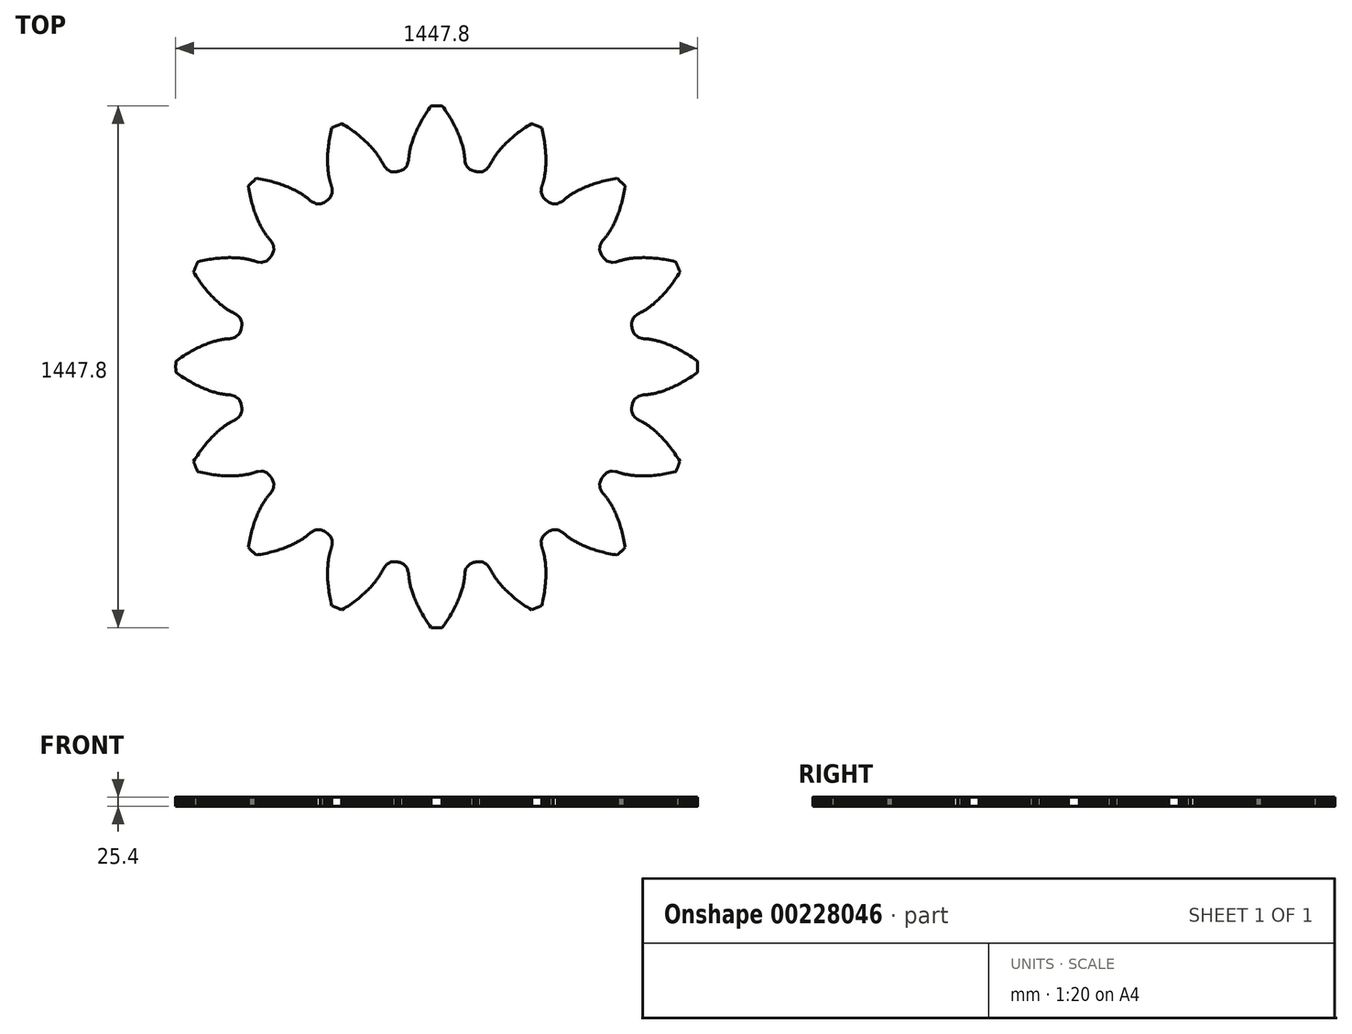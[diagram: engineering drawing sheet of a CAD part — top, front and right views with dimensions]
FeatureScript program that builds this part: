
annotation { "Feature Type Name" : "Feature", "Feature Type Description" : "" }
export const myFeature = defineFeature(function(context is Context, id is Id, definition is map)
    precondition{}
    {
        {
            var Q0;
            Q0=qCreatedBy(makeId("Top.planeOp"),FACE);
            var sketch = newSketch(context, id + "F0", { "sketchPlane" : qUnion([Q0])});
            skLineSegment(sketch, "E0", {"start": v(-103.28, 542.7) * mm, "end": v(-102.33, 543.03) * mm});
            skLineSegment(sketch, "E1", {"start": v(-102.33, 543.03) * mm, "end": v(-92.47, 547.21) * mm});
            skLineSegment(sketch, "E2", {"start": v(-92.47, 547.21) * mm, "end": v(-91.6, 547.71) * mm});
            skLineSegment(sketch, "E3", {"start": v(-91.6, 547.71) * mm, "end": v(-90.77, 548.41) * mm});
            skLineSegment(sketch, "E4", {"start": v(-90.77, 548.41) * mm, "end": v(-83.6, 556.27) * mm});
            skLineSegment(sketch, "E5", {"start": v(-83.6, 556.27) * mm, "end": v(-82.92, 557.1) * mm});
            skLineSegment(sketch, "E6", {"start": v(-82.92, 557.1) * mm, "end": v(-82.3, 558.13) * mm});
            skLineSegment(sketch, "E7", {"start": v(-82.3, 558.13) * mm, "end": v(-81.75, 559.35) * mm});
            skLineSegment(sketch, "E8", {"start": v(-81.75, 559.35) * mm, "end": v(-81.27, 560.76) * mm});
            skLineSegment(sketch, "E9", {"start": v(-81.27, 560.76) * mm, "end": v(-78.74, 569.29) * mm});
            skLineSegment(sketch, "E10", {"start": v(-78.74, 569.29) * mm, "end": v(-78.38, 570.57) * mm});
            skLineSegment(sketch, "E11", {"start": v(-78.38, 570.57) * mm, "end": v(-78.1, 572.03) * mm});
            skLineSegment(sketch, "E12", {"start": v(-78.1, 572.03) * mm, "end": v(-77.89, 573.68) * mm});
            skLineSegment(sketch, "E13", {"start": v(-77.89, 573.68) * mm, "end": v(-77.77, 575.5) * mm});
            skLineSegment(sketch, "E14", {"start": v(-77.77, 575.5) * mm, "end": v(-77.76, 575.78) * mm});
            skLineSegment(sketch, "E15", {"start": v(-77.76, 575.78) * mm, "end": v(-77.7, 577.35) * mm});
            skLineSegment(sketch, "E16", {"start": v(-77.7, 577.35) * mm, "end": v(-77.6, 579.06) * mm});
            skLineSegment(sketch, "E17", {"start": v(-77.6, 579.06) * mm, "end": v(-77.46, 580.9) * mm});
            skLineSegment(sketch, "E18", {"start": v(-77.46, 580.9) * mm, "end": v(-77.29, 582.87) * mm});
            skLineSegment(sketch, "E19", {"start": v(-77.29, 582.87) * mm, "end": v(-77.07, 584.98) * mm});
            skLineSegment(sketch, "E20", {"start": v(-77.07, 584.98) * mm, "end": v(-76.8, 587.21) * mm});
            skLineSegment(sketch, "E21", {"start": v(-76.8, 587.21) * mm, "end": v(-76.48, 589.59) * mm});
            skLineSegment(sketch, "E22", {"start": v(-76.48, 589.59) * mm, "end": v(-76.1, 592.09) * mm});
            skLineSegment(sketch, "E23", {"start": v(-76.1, 592.09) * mm, "end": v(-75.66, 594.72) * mm});
            skLineSegment(sketch, "E24", {"start": v(-75.66, 594.72) * mm, "end": v(-75.16, 597.47) * mm});
            skLineSegment(sketch, "E25", {"start": v(-75.16, 597.47) * mm, "end": v(-74.59, 600.36) * mm});
            skLineSegment(sketch, "E26", {"start": v(-74.59, 600.36) * mm, "end": v(-73.94, 603.37) * mm});
            skLineSegment(sketch, "E27", {"start": v(-73.94, 603.37) * mm, "end": v(-73.22, 606.5) * mm});
            skLineSegment(sketch, "E28", {"start": v(-73.22, 606.5) * mm, "end": v(-72.41, 609.75) * mm});
            skLineSegment(sketch, "E29", {"start": v(-72.41, 609.75) * mm, "end": v(-71.52, 613.12) * mm});
            skLineSegment(sketch, "E30", {"start": v(-71.52, 613.12) * mm, "end": v(-70.54, 616.61) * mm});
            skLineSegment(sketch, "E31", {"start": v(-70.54, 616.61) * mm, "end": v(-69.47, 620.22) * mm});
            skLineSegment(sketch, "E32", {"start": v(-69.47, 620.22) * mm, "end": v(-68.3, 623.94) * mm});
            skLineSegment(sketch, "E33", {"start": v(-68.3, 623.94) * mm, "end": v(-67.03, 627.77) * mm});
            skLineSegment(sketch, "E34", {"start": v(-67.03, 627.77) * mm, "end": v(-65.66, 631.71) * mm});
            skLineSegment(sketch, "E35", {"start": v(-65.66, 631.71) * mm, "end": v(-64.18, 635.76) * mm});
            skLineSegment(sketch, "E36", {"start": v(-64.18, 635.76) * mm, "end": v(-62.59, 639.91) * mm});
            skLineSegment(sketch, "E37", {"start": v(-62.59, 639.91) * mm, "end": v(-60.88, 644.16) * mm});
            skLineSegment(sketch, "E38", {"start": v(-60.88, 644.16) * mm, "end": v(-59.05, 648.52) * mm});
            skLineSegment(sketch, "E39", {"start": v(-59.05, 648.52) * mm, "end": v(-57.1, 652.97) * mm});
            skLineSegment(sketch, "E40", {"start": v(-57.1, 652.97) * mm, "end": v(-55.03, 657.51) * mm});
            skLineSegment(sketch, "E41", {"start": v(-55.03, 657.51) * mm, "end": v(-52.83, 662.15) * mm});
            skLineSegment(sketch, "E42", {"start": v(-52.83, 662.15) * mm, "end": v(-50.5, 666.87) * mm});
            skLineSegment(sketch, "E43", {"start": v(-50.5, 666.87) * mm, "end": v(-48.03, 671.68) * mm});
            skLineSegment(sketch, "E44", {"start": v(-48.03, 671.68) * mm, "end": v(-45.42, 676.57) * mm});
            skLineSegment(sketch, "E45", {"start": v(-45.42, 676.57) * mm, "end": v(-42.67, 681.54) * mm});
            skLineSegment(sketch, "E46", {"start": v(-42.67, 681.54) * mm, "end": v(-39.77, 686.59) * mm});
            skLineSegment(sketch, "E47", {"start": v(-39.77, 686.59) * mm, "end": v(-36.73, 691.7) * mm});
            skLineSegment(sketch, "E48", {"start": v(-36.73, 691.7) * mm, "end": v(-33.54, 696.9) * mm});
            skLineSegment(sketch, "E49", {"start": v(-33.54, 696.9) * mm, "end": v(-30.2, 702.14) * mm});
            skLineSegment(sketch, "E50", {"start": v(-30.2, 702.14) * mm, "end": v(-26.7, 707.46) * mm});
            skLineSegment(sketch, "E51", {"start": v(-26.7, 707.46) * mm, "end": v(-23.03, 712.83) * mm});
            skLineSegment(sketch, "E52", {"start": v(-23.03, 712.83) * mm, "end": v(-19.2, 718.26) * mm});
            skLineSegment(sketch, "E53", {"start": v(-19.2, 718.26) * mm, "end": v(-15.22, 723.74) * mm});
            skLineSegment(sketch, "E54", {"start": v(103.28, 542.7) * mm, "end": v(102.33, 543.03) * mm});
            skLineSegment(sketch, "E55", {"start": v(102.33, 543.03) * mm, "end": v(92.47, 547.21) * mm});
            skLineSegment(sketch, "E56", {"start": v(92.47, 547.21) * mm, "end": v(91.6, 547.71) * mm});
            skLineSegment(sketch, "E57", {"start": v(91.6, 547.71) * mm, "end": v(90.77, 548.41) * mm});
            skLineSegment(sketch, "E58", {"start": v(90.77, 548.41) * mm, "end": v(83.6, 556.27) * mm});
            skLineSegment(sketch, "E59", {"start": v(83.6, 556.27) * mm, "end": v(82.92, 557.1) * mm});
            skLineSegment(sketch, "E60", {"start": v(82.92, 557.1) * mm, "end": v(82.3, 558.13) * mm});
            skLineSegment(sketch, "E61", {"start": v(82.3, 558.13) * mm, "end": v(81.75, 559.35) * mm});
            skLineSegment(sketch, "E62", {"start": v(81.75, 559.35) * mm, "end": v(81.27, 560.76) * mm});
            skLineSegment(sketch, "E63", {"start": v(81.27, 560.76) * mm, "end": v(78.74, 569.29) * mm});
            skLineSegment(sketch, "E64", {"start": v(78.74, 569.29) * mm, "end": v(78.38, 570.57) * mm});
            skLineSegment(sketch, "E65", {"start": v(78.38, 570.57) * mm, "end": v(78.1, 572.03) * mm});
            skLineSegment(sketch, "E66", {"start": v(78.1, 572.03) * mm, "end": v(77.89, 573.68) * mm});
            skLineSegment(sketch, "E67", {"start": v(77.89, 573.68) * mm, "end": v(77.77, 575.5) * mm});
            skLineSegment(sketch, "E68", {"start": v(77.77, 575.5) * mm, "end": v(77.76, 575.78) * mm});
            skLineSegment(sketch, "E69", {"start": v(77.76, 575.78) * mm, "end": v(77.7, 577.35) * mm});
            skLineSegment(sketch, "E70", {"start": v(77.7, 577.35) * mm, "end": v(77.6, 579.06) * mm});
            skLineSegment(sketch, "E71", {"start": v(77.6, 579.06) * mm, "end": v(77.46, 580.9) * mm});
            skLineSegment(sketch, "E72", {"start": v(77.46, 580.9) * mm, "end": v(77.29, 582.87) * mm});
            skLineSegment(sketch, "E73", {"start": v(77.29, 582.87) * mm, "end": v(77.07, 584.98) * mm});
            skLineSegment(sketch, "E74", {"start": v(77.07, 584.98) * mm, "end": v(76.8, 587.21) * mm});
            skLineSegment(sketch, "E75", {"start": v(76.8, 587.21) * mm, "end": v(76.48, 589.59) * mm});
            skLineSegment(sketch, "E76", {"start": v(76.48, 589.59) * mm, "end": v(76.1, 592.09) * mm});
            skLineSegment(sketch, "E77", {"start": v(76.1, 592.09) * mm, "end": v(75.66, 594.72) * mm});
            skLineSegment(sketch, "E78", {"start": v(75.66, 594.72) * mm, "end": v(75.16, 597.47) * mm});
            skLineSegment(sketch, "E79", {"start": v(75.16, 597.47) * mm, "end": v(74.59, 600.36) * mm});
            skLineSegment(sketch, "E80", {"start": v(74.59, 600.36) * mm, "end": v(73.94, 603.37) * mm});
            skLineSegment(sketch, "E81", {"start": v(73.94, 603.37) * mm, "end": v(73.22, 606.5) * mm});
            skLineSegment(sketch, "E82", {"start": v(73.22, 606.5) * mm, "end": v(72.41, 609.75) * mm});
            skLineSegment(sketch, "E83", {"start": v(72.41, 609.75) * mm, "end": v(71.52, 613.12) * mm});
            skLineSegment(sketch, "E84", {"start": v(71.52, 613.12) * mm, "end": v(70.54, 616.61) * mm});
            skLineSegment(sketch, "E85", {"start": v(70.54, 616.61) * mm, "end": v(69.47, 620.22) * mm});
            skLineSegment(sketch, "E86", {"start": v(69.47, 620.22) * mm, "end": v(68.3, 623.94) * mm});
            skLineSegment(sketch, "E87", {"start": v(68.3, 623.94) * mm, "end": v(67.03, 627.77) * mm});
            skLineSegment(sketch, "E88", {"start": v(67.03, 627.77) * mm, "end": v(65.66, 631.71) * mm});
            skLineSegment(sketch, "E89", {"start": v(65.66, 631.71) * mm, "end": v(64.18, 635.76) * mm});
            skLineSegment(sketch, "E90", {"start": v(64.18, 635.76) * mm, "end": v(62.59, 639.91) * mm});
            skLineSegment(sketch, "E91", {"start": v(62.59, 639.91) * mm, "end": v(60.88, 644.16) * mm});
            skLineSegment(sketch, "E92", {"start": v(60.88, 644.16) * mm, "end": v(59.05, 648.52) * mm});
            skLineSegment(sketch, "E93", {"start": v(59.05, 648.52) * mm, "end": v(57.1, 652.97) * mm});
            skLineSegment(sketch, "E94", {"start": v(57.1, 652.97) * mm, "end": v(55.03, 657.51) * mm});
            skLineSegment(sketch, "E95", {"start": v(55.03, 657.51) * mm, "end": v(52.83, 662.15) * mm});
            skLineSegment(sketch, "E96", {"start": v(52.83, 662.15) * mm, "end": v(50.5, 666.87) * mm});
            skLineSegment(sketch, "E97", {"start": v(50.5, 666.87) * mm, "end": v(48.03, 671.68) * mm});
            skLineSegment(sketch, "E98", {"start": v(48.03, 671.68) * mm, "end": v(45.42, 676.57) * mm});
            skLineSegment(sketch, "E99", {"start": v(45.42, 676.57) * mm, "end": v(42.67, 681.54) * mm});
            skLineSegment(sketch, "E100", {"start": v(42.67, 681.54) * mm, "end": v(39.77, 686.59) * mm});
            skLineSegment(sketch, "E101", {"start": v(39.77, 686.59) * mm, "end": v(36.73, 691.7) * mm});
            skLineSegment(sketch, "E102", {"start": v(36.73, 691.7) * mm, "end": v(33.54, 696.9) * mm});
            skLineSegment(sketch, "E103", {"start": v(33.54, 696.9) * mm, "end": v(30.2, 702.14) * mm});
            skLineSegment(sketch, "E104", {"start": v(30.2, 702.14) * mm, "end": v(26.7, 707.46) * mm});
            skLineSegment(sketch, "E105", {"start": v(26.7, 707.46) * mm, "end": v(23.03, 712.83) * mm});
            skLineSegment(sketch, "E106", {"start": v(23.03, 712.83) * mm, "end": v(19.2, 718.26) * mm});
            skLineSegment(sketch, "E107", {"start": v(19.2, 718.26) * mm, "end": v(15.22, 723.74) * mm});
            skArc(sketch, "E108", {"start": v(15.22, 723.74) * mm, "mid": v(0, 723.9) * mm, "end": v(-15.22, 723.74) * mm});
            skLineSegment(sketch, "E109", {"start": v(112.27, 540.92) * mm, "end": v(113.27, 540.85) * mm});
            skLineSegment(sketch, "E110", {"start": v(113.27, 540.85) * mm, "end": v(123.98, 540.94) * mm});
            skLineSegment(sketch, "E111", {"start": v(123.98, 540.94) * mm, "end": v(124.98, 541.07) * mm});
            skLineSegment(sketch, "E112", {"start": v(124.98, 541.07) * mm, "end": v(126, 541.4) * mm});
            skLineSegment(sketch, "E113", {"start": v(126, 541.4) * mm, "end": v(135.64, 545.92) * mm});
            skLineSegment(sketch, "E114", {"start": v(135.64, 545.92) * mm, "end": v(136.59, 546.43) * mm});
            skLineSegment(sketch, "E115", {"start": v(136.59, 546.43) * mm, "end": v(137.55, 547.15) * mm});
            skLineSegment(sketch, "E116", {"start": v(137.55, 547.15) * mm, "end": v(138.53, 548.06) * mm});
            skLineSegment(sketch, "E117", {"start": v(138.53, 548.06) * mm, "end": v(139.5, 549.18) * mm});
            skLineSegment(sketch, "E118", {"start": v(139.5, 549.18) * mm, "end": v(145.11, 556.09) * mm});
            skLineSegment(sketch, "E119", {"start": v(145.11, 556.09) * mm, "end": v(145.93, 557.13) * mm});
            skLineSegment(sketch, "E120", {"start": v(145.93, 557.13) * mm, "end": v(146.76, 558.38) * mm});
            skLineSegment(sketch, "E121", {"start": v(146.76, 558.38) * mm, "end": v(147.58, 559.82) * mm});
            skLineSegment(sketch, "E122", {"start": v(147.58, 559.82) * mm, "end": v(148.4, 561.46) * mm});
            skLineSegment(sketch, "E123", {"start": v(148.4, 561.46) * mm, "end": v(148.5, 561.7) * mm});
            skLineSegment(sketch, "E124", {"start": v(148.5, 561.7) * mm, "end": v(149.17, 563.13) * mm});
            skLineSegment(sketch, "E125", {"start": v(149.17, 563.13) * mm, "end": v(149.9, 564.67) * mm});
            skLineSegment(sketch, "E126", {"start": v(149.9, 564.67) * mm, "end": v(150.74, 566.32) * mm});
            skLineSegment(sketch, "E127", {"start": v(150.74, 566.32) * mm, "end": v(151.65, 568.08) * mm});
            skLineSegment(sketch, "E128", {"start": v(151.65, 568.08) * mm, "end": v(152.66, 569.94) * mm});
            skLineSegment(sketch, "E129", {"start": v(152.66, 569.94) * mm, "end": v(153.76, 571.9) * mm});
            skLineSegment(sketch, "E130", {"start": v(153.76, 571.9) * mm, "end": v(154.97, 573.97) * mm});
            skLineSegment(sketch, "E131", {"start": v(154.97, 573.97) * mm, "end": v(156.27, 576.14) * mm});
            skLineSegment(sketch, "E132", {"start": v(156.27, 576.14) * mm, "end": v(157.68, 578.4) * mm});
            skLineSegment(sketch, "E133", {"start": v(157.68, 578.4) * mm, "end": v(159.2, 580.76) * mm});
            skLineSegment(sketch, "E134", {"start": v(159.2, 580.76) * mm, "end": v(160.84, 583.2) * mm});
            skLineSegment(sketch, "E135", {"start": v(160.84, 583.2) * mm, "end": v(162.59, 585.73) * mm});
            skLineSegment(sketch, "E136", {"start": v(162.59, 585.73) * mm, "end": v(164.45, 588.35) * mm});
            skLineSegment(sketch, "E137", {"start": v(164.45, 588.35) * mm, "end": v(166.44, 591.05) * mm});
            skLineSegment(sketch, "E138", {"start": v(166.44, 591.05) * mm, "end": v(168.55, 593.82) * mm});
            skLineSegment(sketch, "E139", {"start": v(168.55, 593.82) * mm, "end": v(170.8, 596.67) * mm});
            skLineSegment(sketch, "E140", {"start": v(170.8, 596.67) * mm, "end": v(173.16, 599.6) * mm});
            skLineSegment(sketch, "E141", {"start": v(173.16, 599.6) * mm, "end": v(175.67, 602.58) * mm});
            skLineSegment(sketch, "E142", {"start": v(175.67, 602.58) * mm, "end": v(178.3, 605.64) * mm});
            skLineSegment(sketch, "E143", {"start": v(178.3, 605.64) * mm, "end": v(181.08, 608.75) * mm});
            skLineSegment(sketch, "E144", {"start": v(181.08, 608.75) * mm, "end": v(184, 611.92) * mm});
            skLineSegment(sketch, "E145", {"start": v(184, 611.92) * mm, "end": v(187.06, 615.15) * mm});
            skLineSegment(sketch, "E146", {"start": v(187.06, 615.15) * mm, "end": v(190.26, 618.43) * mm});
            skLineSegment(sketch, "E147", {"start": v(190.26, 618.43) * mm, "end": v(193.62, 621.75) * mm});
            skLineSegment(sketch, "E148", {"start": v(193.62, 621.75) * mm, "end": v(197.12, 625.12) * mm});
            skLineSegment(sketch, "E149", {"start": v(197.12, 625.12) * mm, "end": v(200.77, 628.52) * mm});
            skLineSegment(sketch, "E150", {"start": v(200.77, 628.52) * mm, "end": v(204.58, 631.96) * mm});
            skLineSegment(sketch, "E151", {"start": v(204.58, 631.96) * mm, "end": v(208.55, 635.43) * mm});
            skLineSegment(sketch, "E152", {"start": v(208.55, 635.43) * mm, "end": v(212.67, 638.93) * mm});
            skLineSegment(sketch, "E153", {"start": v(212.67, 638.93) * mm, "end": v(216.95, 642.45) * mm});
            skLineSegment(sketch, "E154", {"start": v(216.95, 642.45) * mm, "end": v(221.4, 646) * mm});
            skLineSegment(sketch, "E155", {"start": v(221.4, 646) * mm, "end": v(226, 649.54) * mm});
            skLineSegment(sketch, "E156", {"start": v(226, 649.54) * mm, "end": v(230.77, 653.1) * mm});
            skLineSegment(sketch, "E157", {"start": v(230.77, 653.1) * mm, "end": v(235.7, 656.68) * mm});
            skLineSegment(sketch, "E158", {"start": v(235.7, 656.68) * mm, "end": v(240.8, 660.25) * mm});
            skLineSegment(sketch, "E159", {"start": v(240.8, 660.25) * mm, "end": v(246.07, 663.82) * mm});
            skLineSegment(sketch, "E160", {"start": v(246.07, 663.82) * mm, "end": v(251.51, 667.38) * mm});
            skLineSegment(sketch, "E161", {"start": v(251.51, 667.38) * mm, "end": v(257.12, 670.93) * mm});
            skLineSegment(sketch, "E162", {"start": v(257.12, 670.93) * mm, "end": v(262.9, 674.47) * mm});
            skLineSegment(sketch, "E163", {"start": v(303.1, 461.87) * mm, "end": v(302.34, 462.53) * mm});
            skLineSegment(sketch, "E164", {"start": v(302.34, 462.53) * mm, "end": v(294.84, 470.17) * mm});
            skLineSegment(sketch, "E165", {"start": v(294.84, 470.17) * mm, "end": v(294.22, 470.97) * mm});
            skLineSegment(sketch, "E166", {"start": v(294.22, 470.97) * mm, "end": v(293.73, 471.93) * mm});
            skLineSegment(sketch, "E167", {"start": v(293.73, 471.93) * mm, "end": v(290.1, 481.93) * mm});
            skLineSegment(sketch, "E168", {"start": v(290.1, 481.93) * mm, "end": v(289.8, 482.97) * mm});
            skLineSegment(sketch, "E169", {"start": v(289.8, 482.97) * mm, "end": v(289.63, 484.15) * mm});
            skLineSegment(sketch, "E170", {"start": v(289.63, 484.15) * mm, "end": v(289.59, 485.49) * mm});
            skLineSegment(sketch, "E171", {"start": v(289.59, 485.49) * mm, "end": v(289.68, 486.97) * mm});
            skLineSegment(sketch, "E172", {"start": v(289.68, 486.97) * mm, "end": v(290.6, 495.82) * mm});
            skLineSegment(sketch, "E173", {"start": v(290.6, 495.82) * mm, "end": v(290.76, 497.14) * mm});
            skLineSegment(sketch, "E174", {"start": v(290.76, 497.14) * mm, "end": v(291.06, 498.6) * mm});
            skLineSegment(sketch, "E175", {"start": v(291.06, 498.6) * mm, "end": v(291.5, 500.2) * mm});
            skLineSegment(sketch, "E176", {"start": v(291.5, 500.2) * mm, "end": v(292.08, 501.94) * mm});
            skLineSegment(sketch, "E177", {"start": v(292.08, 501.94) * mm, "end": v(292.18, 502.2) * mm});
            skLineSegment(sketch, "E178", {"start": v(292.18, 502.2) * mm, "end": v(292.72, 503.67) * mm});
            skLineSegment(sketch, "E179", {"start": v(292.72, 503.67) * mm, "end": v(293.28, 505.28) * mm});
            skLineSegment(sketch, "E180", {"start": v(293.28, 505.28) * mm, "end": v(293.86, 507.03) * mm});
            skLineSegment(sketch, "E181", {"start": v(293.86, 507.03) * mm, "end": v(294.46, 508.92) * mm});
            skLineSegment(sketch, "E182", {"start": v(294.46, 508.92) * mm, "end": v(295.06, 510.95) * mm});
            skLineSegment(sketch, "E183", {"start": v(295.06, 510.95) * mm, "end": v(295.67, 513.13) * mm});
            skLineSegment(sketch, "E184", {"start": v(295.67, 513.13) * mm, "end": v(296.28, 515.44) * mm});
            skLineSegment(sketch, "E185", {"start": v(296.28, 515.44) * mm, "end": v(296.9, 517.9) * mm});
            skLineSegment(sketch, "E186", {"start": v(296.9, 517.9) * mm, "end": v(297.5, 520.5) * mm});
            skLineSegment(sketch, "E187", {"start": v(297.5, 520.5) * mm, "end": v(298.08, 523.23) * mm});
            skLineSegment(sketch, "E188", {"start": v(298.08, 523.23) * mm, "end": v(298.66, 526.11) * mm});
            skLineSegment(sketch, "E189", {"start": v(298.66, 526.11) * mm, "end": v(299.21, 529.14) * mm});
            skLineSegment(sketch, "E190", {"start": v(299.21, 529.14) * mm, "end": v(299.74, 532.31) * mm});
            skLineSegment(sketch, "E191", {"start": v(299.74, 532.31) * mm, "end": v(300.24, 535.62) * mm});
            skLineSegment(sketch, "E192", {"start": v(300.24, 535.62) * mm, "end": v(300.71, 539.08) * mm});
            skLineSegment(sketch, "E193", {"start": v(300.71, 539.08) * mm, "end": v(301.14, 542.68) * mm});
            skLineSegment(sketch, "E194", {"start": v(301.14, 542.68) * mm, "end": v(301.53, 546.42) * mm});
            skLineSegment(sketch, "E195", {"start": v(301.53, 546.42) * mm, "end": v(301.88, 550.3) * mm});
            skLineSegment(sketch, "E196", {"start": v(301.88, 550.3) * mm, "end": v(302.17, 554.33) * mm});
            skLineSegment(sketch, "E197", {"start": v(302.17, 554.33) * mm, "end": v(302.4, 558.5) * mm});
            skLineSegment(sketch, "E198", {"start": v(302.4, 558.5) * mm, "end": v(302.59, 562.8) * mm});
            skLineSegment(sketch, "E199", {"start": v(302.59, 562.8) * mm, "end": v(302.7, 567.25) * mm});
            skLineSegment(sketch, "E200", {"start": v(302.7, 567.25) * mm, "end": v(302.76, 571.83) * mm});
            skLineSegment(sketch, "E201", {"start": v(302.76, 571.83) * mm, "end": v(302.74, 576.55) * mm});
            skLineSegment(sketch, "E202", {"start": v(302.74, 576.55) * mm, "end": v(302.64, 581.41) * mm});
            skLineSegment(sketch, "E203", {"start": v(302.64, 581.41) * mm, "end": v(302.46, 586.4) * mm});
            skLineSegment(sketch, "E204", {"start": v(302.46, 586.4) * mm, "end": v(302.2, 591.53) * mm});
            skLineSegment(sketch, "E205", {"start": v(302.2, 591.53) * mm, "end": v(301.85, 596.78) * mm});
            skLineSegment(sketch, "E206", {"start": v(301.85, 596.78) * mm, "end": v(301.41, 602.17) * mm});
            skLineSegment(sketch, "E207", {"start": v(301.41, 602.17) * mm, "end": v(300.87, 607.69) * mm});
            skLineSegment(sketch, "E208", {"start": v(300.87, 607.69) * mm, "end": v(300.24, 613.33) * mm});
            skLineSegment(sketch, "E209", {"start": v(300.24, 613.33) * mm, "end": v(299.5, 619.1) * mm});
            skLineSegment(sketch, "E210", {"start": v(299.5, 619.1) * mm, "end": v(298.64, 625) * mm});
            skLineSegment(sketch, "E211", {"start": v(298.64, 625) * mm, "end": v(297.67, 631) * mm});
            skLineSegment(sketch, "E212", {"start": v(297.67, 631) * mm, "end": v(296.6, 637.14) * mm});
            skLineSegment(sketch, "E213", {"start": v(296.6, 637.14) * mm, "end": v(295.4, 643.4) * mm});
            skLineSegment(sketch, "E214", {"start": v(295.4, 643.4) * mm, "end": v(294.06, 649.76) * mm});
            skLineSegment(sketch, "E215", {"start": v(294.06, 649.76) * mm, "end": v(292.6, 656.23) * mm});
            skLineSegment(sketch, "E216", {"start": v(292.6, 656.23) * mm, "end": v(291.02, 662.82) * mm});
            skArc(sketch, "E217", {"start": v(291.02, 662.82) * mm, "mid": v(277.02, 668.8) * mm, "end": v(262.9, 674.47) * mm});
            skLineSegment(sketch, "E218", {"start": v(310.72, 456.78) * mm, "end": v(311.62, 456.33) * mm});
            skLineSegment(sketch, "E219", {"start": v(311.62, 456.33) * mm, "end": v(321.55, 452.32) * mm});
            skLineSegment(sketch, "E220", {"start": v(321.55, 452.32) * mm, "end": v(322.53, 452.06) * mm});
            skLineSegment(sketch, "E221", {"start": v(322.53, 452.06) * mm, "end": v(323.6, 451.97) * mm});
            skLineSegment(sketch, "E222", {"start": v(323.6, 451.97) * mm, "end": v(334.23, 452.45) * mm});
            skLineSegment(sketch, "E223", {"start": v(334.23, 452.45) * mm, "end": v(335.3, 452.57) * mm});
            skLineSegment(sketch, "E224", {"start": v(335.3, 452.57) * mm, "end": v(336.46, 452.86) * mm});
            skLineSegment(sketch, "E225", {"start": v(336.46, 452.86) * mm, "end": v(337.71, 453.33) * mm});
            skLineSegment(sketch, "E226", {"start": v(337.71, 453.33) * mm, "end": v(339.05, 453.99) * mm});
            skLineSegment(sketch, "E227", {"start": v(339.05, 453.99) * mm, "end": v(346.87, 458.22) * mm});
            skLineSegment(sketch, "E228", {"start": v(346.87, 458.22) * mm, "end": v(348.03, 458.88) * mm});
            skLineSegment(sketch, "E229", {"start": v(348.03, 458.88) * mm, "end": v(349.27, 459.71) * mm});
            skLineSegment(sketch, "E230", {"start": v(349.27, 459.71) * mm, "end": v(350.58, 460.73) * mm});
            skLineSegment(sketch, "E231", {"start": v(350.58, 460.73) * mm, "end": v(351.96, 461.94) * mm});
            skLineSegment(sketch, "E232", {"start": v(351.96, 461.94) * mm, "end": v(352.16, 462.12) * mm});
            skLineSegment(sketch, "E233", {"start": v(352.16, 462.12) * mm, "end": v(353.31, 463.18) * mm});
            skLineSegment(sketch, "E234", {"start": v(353.31, 463.18) * mm, "end": v(354.59, 464.32) * mm});
            skLineSegment(sketch, "E235", {"start": v(354.59, 464.32) * mm, "end": v(355.98, 465.53) * mm});
            skLineSegment(sketch, "E236", {"start": v(355.98, 465.53) * mm, "end": v(357.5, 466.8) * mm});
            skLineSegment(sketch, "E237", {"start": v(357.5, 466.8) * mm, "end": v(359.15, 468.13) * mm});
            skLineSegment(sketch, "E238", {"start": v(359.15, 468.13) * mm, "end": v(360.92, 469.53) * mm});
            skLineSegment(sketch, "E239", {"start": v(360.92, 469.53) * mm, "end": v(362.82, 470.98) * mm});
            skLineSegment(sketch, "E240", {"start": v(362.82, 470.98) * mm, "end": v(364.86, 472.48) * mm});
            skLineSegment(sketch, "E241", {"start": v(364.86, 472.48) * mm, "end": v(367.03, 474.03) * mm});
            skLineSegment(sketch, "E242", {"start": v(367.03, 474.03) * mm, "end": v(369.33, 475.62) * mm});
            skLineSegment(sketch, "E243", {"start": v(369.33, 475.62) * mm, "end": v(371.78, 477.26) * mm});
            skLineSegment(sketch, "E244", {"start": v(371.78, 477.26) * mm, "end": v(374.36, 478.93) * mm});
            skLineSegment(sketch, "E245", {"start": v(374.36, 478.93) * mm, "end": v(377.09, 480.63) * mm});
            skLineSegment(sketch, "E246", {"start": v(377.09, 480.63) * mm, "end": v(379.95, 482.36) * mm});
            skLineSegment(sketch, "E247", {"start": v(379.95, 482.36) * mm, "end": v(382.97, 484.12) * mm});
            skLineSegment(sketch, "E248", {"start": v(382.97, 484.12) * mm, "end": v(386.13, 485.9) * mm});
            skLineSegment(sketch, "E249", {"start": v(386.13, 485.9) * mm, "end": v(389.44, 487.69) * mm});
            skLineSegment(sketch, "E250", {"start": v(389.44, 487.69) * mm, "end": v(392.9, 489.49) * mm});
            skLineSegment(sketch, "E251", {"start": v(392.9, 489.49) * mm, "end": v(396.5, 491.3) * mm});
            skLineSegment(sketch, "E252", {"start": v(396.5, 491.3) * mm, "end": v(400.26, 493.12) * mm});
            skLineSegment(sketch, "E253", {"start": v(400.26, 493.12) * mm, "end": v(404.17, 494.93) * mm});
            skLineSegment(sketch, "E254", {"start": v(404.17, 494.93) * mm, "end": v(408.23, 496.74) * mm});
            skLineSegment(sketch, "E255", {"start": v(408.23, 496.74) * mm, "end": v(412.44, 498.54) * mm});
            skLineSegment(sketch, "E256", {"start": v(412.44, 498.54) * mm, "end": v(416.81, 500.33) * mm});
            skLineSegment(sketch, "E257", {"start": v(416.81, 500.33) * mm, "end": v(421.34, 502.1) * mm});
            skLineSegment(sketch, "E258", {"start": v(421.34, 502.1) * mm, "end": v(426.02, 503.85) * mm});
            skLineSegment(sketch, "E259", {"start": v(426.02, 503.85) * mm, "end": v(430.85, 505.57) * mm});
            skLineSegment(sketch, "E260", {"start": v(430.85, 505.57) * mm, "end": v(435.84, 507.26) * mm});
            skLineSegment(sketch, "E261", {"start": v(435.84, 507.26) * mm, "end": v(440.99, 508.9) * mm});
            skLineSegment(sketch, "E262", {"start": v(440.99, 508.9) * mm, "end": v(446.3, 510.52) * mm});
            skLineSegment(sketch, "E263", {"start": v(446.3, 510.52) * mm, "end": v(451.75, 512.1) * mm});
            skLineSegment(sketch, "E264", {"start": v(451.75, 512.1) * mm, "end": v(457.37, 513.61) * mm});
            skLineSegment(sketch, "E265", {"start": v(457.37, 513.61) * mm, "end": v(463.14, 515.08) * mm});
            skLineSegment(sketch, "E266", {"start": v(463.14, 515.08) * mm, "end": v(469.06, 516.5) * mm});
            skLineSegment(sketch, "E267", {"start": v(469.06, 516.5) * mm, "end": v(475.14, 517.84) * mm});
            skLineSegment(sketch, "E268", {"start": v(475.14, 517.84) * mm, "end": v(481.38, 519.12) * mm});
            skLineSegment(sketch, "E269", {"start": v(481.38, 519.12) * mm, "end": v(487.76, 520.33) * mm});
            skLineSegment(sketch, "E270", {"start": v(487.76, 520.33) * mm, "end": v(494.3, 521.47) * mm});
            skLineSegment(sketch, "E271", {"start": v(494.3, 521.47) * mm, "end": v(501, 522.52) * mm});
            skLineSegment(sketch, "E272", {"start": v(456.78, 310.72) * mm, "end": v(456.33, 311.62) * mm});
            skLineSegment(sketch, "E273", {"start": v(456.33, 311.62) * mm, "end": v(452.32, 321.55) * mm});
            skLineSegment(sketch, "E274", {"start": v(452.32, 321.55) * mm, "end": v(452.06, 322.53) * mm});
            skLineSegment(sketch, "E275", {"start": v(452.06, 322.53) * mm, "end": v(451.97, 323.6) * mm});
            skLineSegment(sketch, "E276", {"start": v(451.97, 323.6) * mm, "end": v(452.45, 334.23) * mm});
            skLineSegment(sketch, "E277", {"start": v(452.45, 334.23) * mm, "end": v(452.57, 335.3) * mm});
            skLineSegment(sketch, "E278", {"start": v(452.57, 335.3) * mm, "end": v(452.86, 336.46) * mm});
            skLineSegment(sketch, "E279", {"start": v(452.86, 336.46) * mm, "end": v(453.33, 337.71) * mm});
            skLineSegment(sketch, "E280", {"start": v(453.33, 337.71) * mm, "end": v(453.99, 339.05) * mm});
            skLineSegment(sketch, "E281", {"start": v(453.99, 339.05) * mm, "end": v(458.22, 346.87) * mm});
            skLineSegment(sketch, "E282", {"start": v(458.22, 346.87) * mm, "end": v(458.88, 348.03) * mm});
            skLineSegment(sketch, "E283", {"start": v(458.88, 348.03) * mm, "end": v(459.71, 349.27) * mm});
            skLineSegment(sketch, "E284", {"start": v(459.71, 349.27) * mm, "end": v(460.73, 350.58) * mm});
            skLineSegment(sketch, "E285", {"start": v(460.73, 350.58) * mm, "end": v(461.94, 351.96) * mm});
            skLineSegment(sketch, "E286", {"start": v(461.94, 351.96) * mm, "end": v(462.12, 352.16) * mm});
            skLineSegment(sketch, "E287", {"start": v(462.12, 352.16) * mm, "end": v(463.18, 353.31) * mm});
            skLineSegment(sketch, "E288", {"start": v(463.18, 353.31) * mm, "end": v(464.32, 354.59) * mm});
            skLineSegment(sketch, "E289", {"start": v(464.32, 354.59) * mm, "end": v(465.53, 355.98) * mm});
            skLineSegment(sketch, "E290", {"start": v(465.53, 355.98) * mm, "end": v(466.8, 357.5) * mm});
            skLineSegment(sketch, "E291", {"start": v(466.8, 357.5) * mm, "end": v(468.13, 359.15) * mm});
            skLineSegment(sketch, "E292", {"start": v(468.13, 359.15) * mm, "end": v(469.53, 360.92) * mm});
            skLineSegment(sketch, "E293", {"start": v(469.53, 360.92) * mm, "end": v(470.98, 362.82) * mm});
            skLineSegment(sketch, "E294", {"start": v(470.98, 362.82) * mm, "end": v(472.48, 364.86) * mm});
            skLineSegment(sketch, "E295", {"start": v(472.48, 364.86) * mm, "end": v(474.03, 367.03) * mm});
            skLineSegment(sketch, "E296", {"start": v(474.03, 367.03) * mm, "end": v(475.62, 369.33) * mm});
            skLineSegment(sketch, "E297", {"start": v(475.62, 369.33) * mm, "end": v(477.26, 371.78) * mm});
            skLineSegment(sketch, "E298", {"start": v(477.26, 371.78) * mm, "end": v(478.93, 374.36) * mm});
            skLineSegment(sketch, "E299", {"start": v(478.93, 374.36) * mm, "end": v(480.63, 377.09) * mm});
            skLineSegment(sketch, "E300", {"start": v(480.63, 377.09) * mm, "end": v(482.36, 379.95) * mm});
            skLineSegment(sketch, "E301", {"start": v(482.36, 379.95) * mm, "end": v(484.12, 382.97) * mm});
            skLineSegment(sketch, "E302", {"start": v(484.12, 382.97) * mm, "end": v(485.9, 386.13) * mm});
            skLineSegment(sketch, "E303", {"start": v(485.9, 386.13) * mm, "end": v(487.69, 389.44) * mm});
            skLineSegment(sketch, "E304", {"start": v(487.69, 389.44) * mm, "end": v(489.49, 392.9) * mm});
            skLineSegment(sketch, "E305", {"start": v(489.49, 392.9) * mm, "end": v(491.3, 396.5) * mm});
            skLineSegment(sketch, "E306", {"start": v(491.3, 396.5) * mm, "end": v(493.12, 400.26) * mm});
            skLineSegment(sketch, "E307", {"start": v(493.12, 400.26) * mm, "end": v(494.93, 404.17) * mm});
            skLineSegment(sketch, "E308", {"start": v(494.93, 404.17) * mm, "end": v(496.74, 408.23) * mm});
            skLineSegment(sketch, "E309", {"start": v(496.74, 408.23) * mm, "end": v(498.54, 412.44) * mm});
            skLineSegment(sketch, "E310", {"start": v(498.54, 412.44) * mm, "end": v(500.33, 416.81) * mm});
            skLineSegment(sketch, "E311", {"start": v(500.33, 416.81) * mm, "end": v(502.1, 421.34) * mm});
            skLineSegment(sketch, "E312", {"start": v(502.1, 421.34) * mm, "end": v(503.85, 426.02) * mm});
            skLineSegment(sketch, "E313", {"start": v(503.85, 426.02) * mm, "end": v(505.57, 430.85) * mm});
            skLineSegment(sketch, "E314", {"start": v(505.57, 430.85) * mm, "end": v(507.26, 435.84) * mm});
            skLineSegment(sketch, "E315", {"start": v(507.26, 435.84) * mm, "end": v(508.9, 440.99) * mm});
            skLineSegment(sketch, "E316", {"start": v(508.9, 440.99) * mm, "end": v(510.52, 446.3) * mm});
            skLineSegment(sketch, "E317", {"start": v(510.52, 446.3) * mm, "end": v(512.1, 451.75) * mm});
            skLineSegment(sketch, "E318", {"start": v(512.1, 451.75) * mm, "end": v(513.61, 457.37) * mm});
            skLineSegment(sketch, "E319", {"start": v(513.61, 457.37) * mm, "end": v(515.08, 463.14) * mm});
            skLineSegment(sketch, "E320", {"start": v(515.08, 463.14) * mm, "end": v(516.5, 469.06) * mm});
            skLineSegment(sketch, "E321", {"start": v(516.5, 469.06) * mm, "end": v(517.84, 475.14) * mm});
            skLineSegment(sketch, "E322", {"start": v(517.84, 475.14) * mm, "end": v(519.12, 481.38) * mm});
            skLineSegment(sketch, "E323", {"start": v(519.12, 481.38) * mm, "end": v(520.33, 487.76) * mm});
            skLineSegment(sketch, "E324", {"start": v(520.33, 487.76) * mm, "end": v(521.47, 494.3) * mm});
            skLineSegment(sketch, "E325", {"start": v(521.47, 494.3) * mm, "end": v(522.52, 501) * mm});
            skArc(sketch, "E326", {"start": v(522.52, 501) * mm, "mid": v(511.87, 511.87) * mm, "end": v(501, 522.52) * mm});
            skLineSegment(sketch, "E327", {"start": v(461.87, 303.1) * mm, "end": v(462.53, 302.34) * mm});
            skLineSegment(sketch, "E328", {"start": v(462.53, 302.34) * mm, "end": v(470.17, 294.84) * mm});
            skLineSegment(sketch, "E329", {"start": v(470.17, 294.84) * mm, "end": v(470.97, 294.22) * mm});
            skLineSegment(sketch, "E330", {"start": v(470.97, 294.22) * mm, "end": v(471.93, 293.73) * mm});
            skLineSegment(sketch, "E331", {"start": v(471.93, 293.73) * mm, "end": v(481.93, 290.1) * mm});
            skLineSegment(sketch, "E332", {"start": v(481.93, 290.1) * mm, "end": v(482.97, 289.8) * mm});
            skLineSegment(sketch, "E333", {"start": v(482.97, 289.8) * mm, "end": v(484.15, 289.63) * mm});
            skLineSegment(sketch, "E334", {"start": v(484.15, 289.63) * mm, "end": v(485.49, 289.59) * mm});
            skLineSegment(sketch, "E335", {"start": v(485.49, 289.59) * mm, "end": v(486.97, 289.68) * mm});
            skLineSegment(sketch, "E336", {"start": v(486.97, 289.68) * mm, "end": v(495.82, 290.6) * mm});
            skLineSegment(sketch, "E337", {"start": v(495.82, 290.6) * mm, "end": v(497.14, 290.76) * mm});
            skLineSegment(sketch, "E338", {"start": v(497.14, 290.76) * mm, "end": v(498.6, 291.06) * mm});
            skLineSegment(sketch, "E339", {"start": v(498.6, 291.06) * mm, "end": v(500.2, 291.5) * mm});
            skLineSegment(sketch, "E340", {"start": v(500.2, 291.5) * mm, "end": v(501.94, 292.08) * mm});
            skLineSegment(sketch, "E341", {"start": v(501.94, 292.08) * mm, "end": v(502.2, 292.18) * mm});
            skLineSegment(sketch, "E342", {"start": v(502.2, 292.18) * mm, "end": v(503.67, 292.72) * mm});
            skLineSegment(sketch, "E343", {"start": v(503.67, 292.72) * mm, "end": v(505.28, 293.28) * mm});
            skLineSegment(sketch, "E344", {"start": v(505.28, 293.28) * mm, "end": v(507.03, 293.86) * mm});
            skLineSegment(sketch, "E345", {"start": v(507.03, 293.86) * mm, "end": v(508.92, 294.46) * mm});
            skLineSegment(sketch, "E346", {"start": v(508.92, 294.46) * mm, "end": v(510.95, 295.06) * mm});
            skLineSegment(sketch, "E347", {"start": v(510.95, 295.06) * mm, "end": v(513.13, 295.67) * mm});
            skLineSegment(sketch, "E348", {"start": v(513.13, 295.67) * mm, "end": v(515.44, 296.28) * mm});
            skLineSegment(sketch, "E349", {"start": v(515.44, 296.28) * mm, "end": v(517.9, 296.9) * mm});
            skLineSegment(sketch, "E350", {"start": v(517.9, 296.9) * mm, "end": v(520.5, 297.5) * mm});
            skLineSegment(sketch, "E351", {"start": v(520.5, 297.5) * mm, "end": v(523.23, 298.08) * mm});
            skLineSegment(sketch, "E352", {"start": v(523.23, 298.08) * mm, "end": v(526.11, 298.66) * mm});
            skLineSegment(sketch, "E353", {"start": v(526.11, 298.66) * mm, "end": v(529.14, 299.21) * mm});
            skLineSegment(sketch, "E354", {"start": v(529.14, 299.21) * mm, "end": v(532.31, 299.74) * mm});
            skLineSegment(sketch, "E355", {"start": v(532.31, 299.74) * mm, "end": v(535.62, 300.24) * mm});
            skLineSegment(sketch, "E356", {"start": v(535.62, 300.24) * mm, "end": v(539.08, 300.71) * mm});
            skLineSegment(sketch, "E357", {"start": v(539.08, 300.71) * mm, "end": v(542.68, 301.14) * mm});
            skLineSegment(sketch, "E358", {"start": v(542.68, 301.14) * mm, "end": v(546.42, 301.53) * mm});
            skLineSegment(sketch, "E359", {"start": v(546.42, 301.53) * mm, "end": v(550.3, 301.88) * mm});
            skLineSegment(sketch, "E360", {"start": v(550.3, 301.88) * mm, "end": v(554.33, 302.17) * mm});
            skLineSegment(sketch, "E361", {"start": v(554.33, 302.17) * mm, "end": v(558.5, 302.4) * mm});
            skLineSegment(sketch, "E362", {"start": v(558.5, 302.4) * mm, "end": v(562.8, 302.59) * mm});
            skLineSegment(sketch, "E363", {"start": v(562.8, 302.59) * mm, "end": v(567.25, 302.7) * mm});
            skLineSegment(sketch, "E364", {"start": v(567.25, 302.7) * mm, "end": v(571.83, 302.76) * mm});
            skLineSegment(sketch, "E365", {"start": v(571.83, 302.76) * mm, "end": v(576.55, 302.74) * mm});
            skLineSegment(sketch, "E366", {"start": v(576.55, 302.74) * mm, "end": v(581.41, 302.64) * mm});
            skLineSegment(sketch, "E367", {"start": v(581.41, 302.64) * mm, "end": v(586.4, 302.46) * mm});
            skLineSegment(sketch, "E368", {"start": v(586.4, 302.46) * mm, "end": v(591.53, 302.2) * mm});
            skLineSegment(sketch, "E369", {"start": v(591.53, 302.2) * mm, "end": v(596.78, 301.85) * mm});
            skLineSegment(sketch, "E370", {"start": v(596.78, 301.85) * mm, "end": v(602.17, 301.41) * mm});
            skLineSegment(sketch, "E371", {"start": v(602.17, 301.41) * mm, "end": v(607.69, 300.87) * mm});
            skLineSegment(sketch, "E372", {"start": v(607.69, 300.87) * mm, "end": v(613.33, 300.24) * mm});
            skLineSegment(sketch, "E373", {"start": v(613.33, 300.24) * mm, "end": v(619.1, 299.5) * mm});
            skLineSegment(sketch, "E374", {"start": v(619.1, 299.5) * mm, "end": v(625, 298.64) * mm});
            skLineSegment(sketch, "E375", {"start": v(625, 298.64) * mm, "end": v(631, 297.67) * mm});
            skLineSegment(sketch, "E376", {"start": v(631, 297.67) * mm, "end": v(637.14, 296.6) * mm});
            skLineSegment(sketch, "E377", {"start": v(637.14, 296.6) * mm, "end": v(643.4, 295.4) * mm});
            skLineSegment(sketch, "E378", {"start": v(643.4, 295.4) * mm, "end": v(649.76, 294.06) * mm});
            skLineSegment(sketch, "E379", {"start": v(649.76, 294.06) * mm, "end": v(656.23, 292.6) * mm});
            skLineSegment(sketch, "E380", {"start": v(656.23, 292.6) * mm, "end": v(662.82, 291.02) * mm});
            skLineSegment(sketch, "E381", {"start": v(540.92, 112.27) * mm, "end": v(540.85, 113.27) * mm});
            skLineSegment(sketch, "E382", {"start": v(540.85, 113.27) * mm, "end": v(540.94, 123.98) * mm});
            skLineSegment(sketch, "E383", {"start": v(540.94, 123.98) * mm, "end": v(541.07, 124.98) * mm});
            skLineSegment(sketch, "E384", {"start": v(541.07, 124.98) * mm, "end": v(541.4, 126) * mm});
            skLineSegment(sketch, "E385", {"start": v(541.4, 126) * mm, "end": v(545.92, 135.64) * mm});
            skLineSegment(sketch, "E386", {"start": v(545.92, 135.64) * mm, "end": v(546.43, 136.59) * mm});
            skLineSegment(sketch, "E387", {"start": v(546.43, 136.59) * mm, "end": v(547.15, 137.55) * mm});
            skLineSegment(sketch, "E388", {"start": v(547.15, 137.55) * mm, "end": v(548.06, 138.53) * mm});
            skLineSegment(sketch, "E389", {"start": v(548.06, 138.53) * mm, "end": v(549.18, 139.5) * mm});
            skLineSegment(sketch, "E390", {"start": v(549.18, 139.5) * mm, "end": v(556.09, 145.11) * mm});
            skLineSegment(sketch, "E391", {"start": v(556.09, 145.11) * mm, "end": v(557.13, 145.93) * mm});
            skLineSegment(sketch, "E392", {"start": v(557.13, 145.93) * mm, "end": v(558.38, 146.76) * mm});
            skLineSegment(sketch, "E393", {"start": v(558.38, 146.76) * mm, "end": v(559.82, 147.58) * mm});
            skLineSegment(sketch, "E394", {"start": v(559.82, 147.58) * mm, "end": v(561.46, 148.4) * mm});
            skLineSegment(sketch, "E395", {"start": v(561.46, 148.4) * mm, "end": v(561.7, 148.5) * mm});
            skLineSegment(sketch, "E396", {"start": v(561.7, 148.5) * mm, "end": v(563.13, 149.17) * mm});
            skLineSegment(sketch, "E397", {"start": v(563.13, 149.17) * mm, "end": v(564.67, 149.9) * mm});
            skLineSegment(sketch, "E398", {"start": v(564.67, 149.9) * mm, "end": v(566.32, 150.74) * mm});
            skLineSegment(sketch, "E399", {"start": v(566.32, 150.74) * mm, "end": v(568.08, 151.65) * mm});
            skLineSegment(sketch, "E400", {"start": v(568.08, 151.65) * mm, "end": v(569.94, 152.66) * mm});
            skLineSegment(sketch, "E401", {"start": v(569.94, 152.66) * mm, "end": v(571.9, 153.76) * mm});
            skLineSegment(sketch, "E402", {"start": v(571.9, 153.76) * mm, "end": v(573.97, 154.97) * mm});
            skLineSegment(sketch, "E403", {"start": v(573.97, 154.97) * mm, "end": v(576.14, 156.27) * mm});
            skLineSegment(sketch, "E404", {"start": v(576.14, 156.27) * mm, "end": v(578.4, 157.68) * mm});
            skLineSegment(sketch, "E405", {"start": v(578.4, 157.68) * mm, "end": v(580.76, 159.2) * mm});
            skLineSegment(sketch, "E406", {"start": v(580.76, 159.2) * mm, "end": v(583.2, 160.84) * mm});
            skLineSegment(sketch, "E407", {"start": v(583.2, 160.84) * mm, "end": v(585.73, 162.59) * mm});
            skLineSegment(sketch, "E408", {"start": v(585.73, 162.59) * mm, "end": v(588.35, 164.45) * mm});
            skLineSegment(sketch, "E409", {"start": v(588.35, 164.45) * mm, "end": v(591.05, 166.44) * mm});
            skLineSegment(sketch, "E410", {"start": v(591.05, 166.44) * mm, "end": v(593.82, 168.55) * mm});
            skLineSegment(sketch, "E411", {"start": v(593.82, 168.55) * mm, "end": v(596.67, 170.8) * mm});
            skLineSegment(sketch, "E412", {"start": v(596.67, 170.8) * mm, "end": v(599.6, 173.16) * mm});
            skLineSegment(sketch, "E413", {"start": v(599.6, 173.16) * mm, "end": v(602.58, 175.67) * mm});
            skLineSegment(sketch, "E414", {"start": v(602.58, 175.67) * mm, "end": v(605.64, 178.3) * mm});
            skLineSegment(sketch, "E415", {"start": v(605.64, 178.3) * mm, "end": v(608.75, 181.08) * mm});
            skLineSegment(sketch, "E416", {"start": v(608.75, 181.08) * mm, "end": v(611.92, 184) * mm});
            skLineSegment(sketch, "E417", {"start": v(611.92, 184) * mm, "end": v(615.15, 187.06) * mm});
            skLineSegment(sketch, "E418", {"start": v(615.15, 187.06) * mm, "end": v(618.43, 190.26) * mm});
            skLineSegment(sketch, "E419", {"start": v(618.43, 190.26) * mm, "end": v(621.75, 193.62) * mm});
            skLineSegment(sketch, "E420", {"start": v(621.75, 193.62) * mm, "end": v(625.12, 197.12) * mm});
            skLineSegment(sketch, "E421", {"start": v(625.12, 197.12) * mm, "end": v(628.52, 200.77) * mm});
            skLineSegment(sketch, "E422", {"start": v(628.52, 200.77) * mm, "end": v(631.96, 204.58) * mm});
            skLineSegment(sketch, "E423", {"start": v(631.96, 204.58) * mm, "end": v(635.43, 208.55) * mm});
            skLineSegment(sketch, "E424", {"start": v(635.43, 208.55) * mm, "end": v(638.93, 212.67) * mm});
            skLineSegment(sketch, "E425", {"start": v(638.93, 212.67) * mm, "end": v(642.45, 216.95) * mm});
            skLineSegment(sketch, "E426", {"start": v(642.45, 216.95) * mm, "end": v(646, 221.4) * mm});
            skLineSegment(sketch, "E427", {"start": v(646, 221.4) * mm, "end": v(649.54, 226) * mm});
            skLineSegment(sketch, "E428", {"start": v(649.54, 226) * mm, "end": v(653.1, 230.77) * mm});
            skLineSegment(sketch, "E429", {"start": v(653.1, 230.77) * mm, "end": v(656.68, 235.7) * mm});
            skLineSegment(sketch, "E430", {"start": v(656.68, 235.7) * mm, "end": v(660.25, 240.8) * mm});
            skLineSegment(sketch, "E431", {"start": v(660.25, 240.8) * mm, "end": v(663.82, 246.07) * mm});
            skLineSegment(sketch, "E432", {"start": v(663.82, 246.07) * mm, "end": v(667.38, 251.51) * mm});
            skLineSegment(sketch, "E433", {"start": v(667.38, 251.51) * mm, "end": v(670.93, 257.12) * mm});
            skLineSegment(sketch, "E434", {"start": v(670.93, 257.12) * mm, "end": v(674.47, 262.9) * mm});
            skArc(sketch, "E435", {"start": v(674.47, 262.9) * mm, "mid": v(668.8, 277.02) * mm, "end": v(662.82, 291.02) * mm});
            skLineSegment(sketch, "E436", {"start": v(542.7, 103.28) * mm, "end": v(543.03, 102.33) * mm});
            skLineSegment(sketch, "E437", {"start": v(543.03, 102.33) * mm, "end": v(547.21, 92.47) * mm});
            skLineSegment(sketch, "E438", {"start": v(547.21, 92.47) * mm, "end": v(547.71, 91.6) * mm});
            skLineSegment(sketch, "E439", {"start": v(547.71, 91.6) * mm, "end": v(548.41, 90.77) * mm});
            skLineSegment(sketch, "E440", {"start": v(548.41, 90.77) * mm, "end": v(556.27, 83.6) * mm});
            skLineSegment(sketch, "E441", {"start": v(556.27, 83.6) * mm, "end": v(557.1, 82.92) * mm});
            skLineSegment(sketch, "E442", {"start": v(557.1, 82.92) * mm, "end": v(558.13, 82.3) * mm});
            skLineSegment(sketch, "E443", {"start": v(558.13, 82.3) * mm, "end": v(559.35, 81.75) * mm});
            skLineSegment(sketch, "E444", {"start": v(559.35, 81.75) * mm, "end": v(560.76, 81.27) * mm});
            skLineSegment(sketch, "E445", {"start": v(560.76, 81.27) * mm, "end": v(569.29, 78.74) * mm});
            skLineSegment(sketch, "E446", {"start": v(569.29, 78.74) * mm, "end": v(570.57, 78.38) * mm});
            skLineSegment(sketch, "E447", {"start": v(570.57, 78.38) * mm, "end": v(572.03, 78.1) * mm});
            skLineSegment(sketch, "E448", {"start": v(572.03, 78.1) * mm, "end": v(573.68, 77.89) * mm});
            skLineSegment(sketch, "E449", {"start": v(573.68, 77.89) * mm, "end": v(575.5, 77.77) * mm});
            skLineSegment(sketch, "E450", {"start": v(575.5, 77.77) * mm, "end": v(575.78, 77.76) * mm});
            skLineSegment(sketch, "E451", {"start": v(575.78, 77.76) * mm, "end": v(577.35, 77.7) * mm});
            skLineSegment(sketch, "E452", {"start": v(577.35, 77.7) * mm, "end": v(579.06, 77.6) * mm});
            skLineSegment(sketch, "E453", {"start": v(579.06, 77.6) * mm, "end": v(580.9, 77.46) * mm});
            skLineSegment(sketch, "E454", {"start": v(580.9, 77.46) * mm, "end": v(582.87, 77.29) * mm});
            skLineSegment(sketch, "E455", {"start": v(582.87, 77.29) * mm, "end": v(584.98, 77.07) * mm});
            skLineSegment(sketch, "E456", {"start": v(584.98, 77.07) * mm, "end": v(587.21, 76.8) * mm});
            skLineSegment(sketch, "E457", {"start": v(587.21, 76.8) * mm, "end": v(589.59, 76.48) * mm});
            skLineSegment(sketch, "E458", {"start": v(589.59, 76.48) * mm, "end": v(592.09, 76.1) * mm});
            skLineSegment(sketch, "E459", {"start": v(592.09, 76.1) * mm, "end": v(594.72, 75.66) * mm});
            skLineSegment(sketch, "E460", {"start": v(594.72, 75.66) * mm, "end": v(597.47, 75.16) * mm});
            skLineSegment(sketch, "E461", {"start": v(597.47, 75.16) * mm, "end": v(600.36, 74.59) * mm});
            skLineSegment(sketch, "E462", {"start": v(600.36, 74.59) * mm, "end": v(603.37, 73.94) * mm});
            skLineSegment(sketch, "E463", {"start": v(603.37, 73.94) * mm, "end": v(606.5, 73.22) * mm});
            skLineSegment(sketch, "E464", {"start": v(606.5, 73.22) * mm, "end": v(609.75, 72.41) * mm});
            skLineSegment(sketch, "E465", {"start": v(609.75, 72.41) * mm, "end": v(613.12, 71.52) * mm});
            skLineSegment(sketch, "E466", {"start": v(613.12, 71.52) * mm, "end": v(616.61, 70.54) * mm});
            skLineSegment(sketch, "E467", {"start": v(616.61, 70.54) * mm, "end": v(620.22, 69.47) * mm});
            skLineSegment(sketch, "E468", {"start": v(620.22, 69.47) * mm, "end": v(623.94, 68.3) * mm});
            skLineSegment(sketch, "E469", {"start": v(623.94, 68.3) * mm, "end": v(627.77, 67.03) * mm});
            skLineSegment(sketch, "E470", {"start": v(627.77, 67.03) * mm, "end": v(631.71, 65.66) * mm});
            skLineSegment(sketch, "E471", {"start": v(631.71, 65.66) * mm, "end": v(635.76, 64.18) * mm});
            skLineSegment(sketch, "E472", {"start": v(635.76, 64.18) * mm, "end": v(639.91, 62.59) * mm});
            skLineSegment(sketch, "E473", {"start": v(639.91, 62.59) * mm, "end": v(644.16, 60.88) * mm});
            skLineSegment(sketch, "E474", {"start": v(644.16, 60.88) * mm, "end": v(648.52, 59.05) * mm});
            skLineSegment(sketch, "E475", {"start": v(648.52, 59.05) * mm, "end": v(652.97, 57.1) * mm});
            skLineSegment(sketch, "E476", {"start": v(652.97, 57.1) * mm, "end": v(657.51, 55.03) * mm});
            skLineSegment(sketch, "E477", {"start": v(657.51, 55.03) * mm, "end": v(662.15, 52.83) * mm});
            skLineSegment(sketch, "E478", {"start": v(662.15, 52.83) * mm, "end": v(666.87, 50.5) * mm});
            skLineSegment(sketch, "E479", {"start": v(666.87, 50.5) * mm, "end": v(671.68, 48.03) * mm});
            skLineSegment(sketch, "E480", {"start": v(671.68, 48.03) * mm, "end": v(676.57, 45.42) * mm});
            skLineSegment(sketch, "E481", {"start": v(676.57, 45.42) * mm, "end": v(681.54, 42.67) * mm});
            skLineSegment(sketch, "E482", {"start": v(681.54, 42.67) * mm, "end": v(686.59, 39.77) * mm});
            skLineSegment(sketch, "E483", {"start": v(686.59, 39.77) * mm, "end": v(691.7, 36.73) * mm});
            skLineSegment(sketch, "E484", {"start": v(691.7, 36.73) * mm, "end": v(696.9, 33.54) * mm});
            skLineSegment(sketch, "E485", {"start": v(696.9, 33.54) * mm, "end": v(702.14, 30.2) * mm});
            skLineSegment(sketch, "E486", {"start": v(702.14, 30.2) * mm, "end": v(707.46, 26.7) * mm});
            skLineSegment(sketch, "E487", {"start": v(707.46, 26.7) * mm, "end": v(712.83, 23.03) * mm});
            skLineSegment(sketch, "E488", {"start": v(712.83, 23.03) * mm, "end": v(718.26, 19.2) * mm});
            skLineSegment(sketch, "E489", {"start": v(718.26, 19.2) * mm, "end": v(723.74, 15.22) * mm});
            skLineSegment(sketch, "E490", {"start": v(542.7, -103.28) * mm, "end": v(543.03, -102.33) * mm});
            skLineSegment(sketch, "E491", {"start": v(543.03, -102.33) * mm, "end": v(547.21, -92.47) * mm});
            skLineSegment(sketch, "E492", {"start": v(547.21, -92.47) * mm, "end": v(547.71, -91.6) * mm});
            skLineSegment(sketch, "E493", {"start": v(547.71, -91.6) * mm, "end": v(548.41, -90.77) * mm});
            skLineSegment(sketch, "E494", {"start": v(548.41, -90.77) * mm, "end": v(556.27, -83.6) * mm});
            skLineSegment(sketch, "E495", {"start": v(556.27, -83.6) * mm, "end": v(557.1, -82.92) * mm});
            skLineSegment(sketch, "E496", {"start": v(557.1, -82.92) * mm, "end": v(558.13, -82.3) * mm});
            skLineSegment(sketch, "E497", {"start": v(558.13, -82.3) * mm, "end": v(559.35, -81.75) * mm});
            skLineSegment(sketch, "E498", {"start": v(559.35, -81.75) * mm, "end": v(560.76, -81.27) * mm});
            skLineSegment(sketch, "E499", {"start": v(560.76, -81.27) * mm, "end": v(569.29, -78.74) * mm});
            skLineSegment(sketch, "E500", {"start": v(569.29, -78.74) * mm, "end": v(570.57, -78.38) * mm});
            skLineSegment(sketch, "E501", {"start": v(570.57, -78.38) * mm, "end": v(572.03, -78.1) * mm});
            skLineSegment(sketch, "E502", {"start": v(572.03, -78.1) * mm, "end": v(573.68, -77.89) * mm});
            skLineSegment(sketch, "E503", {"start": v(573.68, -77.89) * mm, "end": v(575.5, -77.77) * mm});
            skLineSegment(sketch, "E504", {"start": v(575.5, -77.77) * mm, "end": v(575.78, -77.76) * mm});
            skLineSegment(sketch, "E505", {"start": v(575.78, -77.76) * mm, "end": v(577.35, -77.7) * mm});
            skLineSegment(sketch, "E506", {"start": v(577.35, -77.7) * mm, "end": v(579.06, -77.6) * mm});
            skLineSegment(sketch, "E507", {"start": v(579.06, -77.6) * mm, "end": v(580.9, -77.46) * mm});
            skLineSegment(sketch, "E508", {"start": v(580.9, -77.46) * mm, "end": v(582.87, -77.29) * mm});
            skLineSegment(sketch, "E509", {"start": v(582.87, -77.29) * mm, "end": v(584.98, -77.07) * mm});
            skLineSegment(sketch, "E510", {"start": v(584.98, -77.07) * mm, "end": v(587.21, -76.8) * mm});
            skLineSegment(sketch, "E511", {"start": v(587.21, -76.8) * mm, "end": v(589.59, -76.48) * mm});
            skLineSegment(sketch, "E512", {"start": v(589.59, -76.48) * mm, "end": v(592.09, -76.1) * mm});
            skLineSegment(sketch, "E513", {"start": v(592.09, -76.1) * mm, "end": v(594.72, -75.66) * mm});
            skLineSegment(sketch, "E514", {"start": v(594.72, -75.66) * mm, "end": v(597.47, -75.16) * mm});
            skLineSegment(sketch, "E515", {"start": v(597.47, -75.16) * mm, "end": v(600.36, -74.59) * mm});
            skLineSegment(sketch, "E516", {"start": v(600.36, -74.59) * mm, "end": v(603.37, -73.94) * mm});
            skLineSegment(sketch, "E517", {"start": v(603.37, -73.94) * mm, "end": v(606.5, -73.22) * mm});
            skLineSegment(sketch, "E518", {"start": v(606.5, -73.22) * mm, "end": v(609.75, -72.41) * mm});
            skLineSegment(sketch, "E519", {"start": v(609.75, -72.41) * mm, "end": v(613.12, -71.52) * mm});
            skLineSegment(sketch, "E520", {"start": v(613.12, -71.52) * mm, "end": v(616.61, -70.54) * mm});
            skLineSegment(sketch, "E521", {"start": v(616.61, -70.54) * mm, "end": v(620.22, -69.47) * mm});
            skLineSegment(sketch, "E522", {"start": v(620.22, -69.47) * mm, "end": v(623.94, -68.3) * mm});
            skLineSegment(sketch, "E523", {"start": v(623.94, -68.3) * mm, "end": v(627.77, -67.03) * mm});
            skLineSegment(sketch, "E524", {"start": v(627.77, -67.03) * mm, "end": v(631.71, -65.66) * mm});
            skLineSegment(sketch, "E525", {"start": v(631.71, -65.66) * mm, "end": v(635.76, -64.18) * mm});
            skLineSegment(sketch, "E526", {"start": v(635.76, -64.18) * mm, "end": v(639.91, -62.59) * mm});
            skLineSegment(sketch, "E527", {"start": v(639.91, -62.59) * mm, "end": v(644.16, -60.88) * mm});
            skLineSegment(sketch, "E528", {"start": v(644.16, -60.88) * mm, "end": v(648.52, -59.05) * mm});
            skLineSegment(sketch, "E529", {"start": v(648.52, -59.05) * mm, "end": v(652.97, -57.1) * mm});
            skLineSegment(sketch, "E530", {"start": v(652.97, -57.1) * mm, "end": v(657.51, -55.03) * mm});
            skLineSegment(sketch, "E531", {"start": v(657.51, -55.03) * mm, "end": v(662.15, -52.83) * mm});
            skLineSegment(sketch, "E532", {"start": v(662.15, -52.83) * mm, "end": v(666.87, -50.5) * mm});
            skLineSegment(sketch, "E533", {"start": v(666.87, -50.5) * mm, "end": v(671.68, -48.03) * mm});
            skLineSegment(sketch, "E534", {"start": v(671.68, -48.03) * mm, "end": v(676.57, -45.42) * mm});
            skLineSegment(sketch, "E535", {"start": v(676.57, -45.42) * mm, "end": v(681.54, -42.67) * mm});
            skLineSegment(sketch, "E536", {"start": v(681.54, -42.67) * mm, "end": v(686.59, -39.77) * mm});
            skLineSegment(sketch, "E537", {"start": v(686.59, -39.77) * mm, "end": v(691.7, -36.73) * mm});
            skLineSegment(sketch, "E538", {"start": v(691.7, -36.73) * mm, "end": v(696.9, -33.54) * mm});
            skLineSegment(sketch, "E539", {"start": v(696.9, -33.54) * mm, "end": v(702.14, -30.2) * mm});
            skLineSegment(sketch, "E540", {"start": v(702.14, -30.2) * mm, "end": v(707.46, -26.7) * mm});
            skLineSegment(sketch, "E541", {"start": v(707.46, -26.7) * mm, "end": v(712.83, -23.03) * mm});
            skLineSegment(sketch, "E542", {"start": v(712.83, -23.03) * mm, "end": v(718.26, -19.2) * mm});
            skLineSegment(sketch, "E543", {"start": v(718.26, -19.2) * mm, "end": v(723.74, -15.22) * mm});
            skArc(sketch, "E544", {"start": v(723.74, -15.22) * mm, "mid": v(723.9, 0) * mm, "end": v(723.74, 15.22) * mm});
            skLineSegment(sketch, "E545", {"start": v(540.92, -112.27) * mm, "end": v(540.85, -113.27) * mm});
            skLineSegment(sketch, "E546", {"start": v(540.85, -113.27) * mm, "end": v(540.94, -123.98) * mm});
            skLineSegment(sketch, "E547", {"start": v(540.94, -123.98) * mm, "end": v(541.07, -124.98) * mm});
            skLineSegment(sketch, "E548", {"start": v(541.07, -124.98) * mm, "end": v(541.4, -126) * mm});
            skLineSegment(sketch, "E549", {"start": v(541.4, -126) * mm, "end": v(545.92, -135.64) * mm});
            skLineSegment(sketch, "E550", {"start": v(545.92, -135.64) * mm, "end": v(546.43, -136.59) * mm});
            skLineSegment(sketch, "E551", {"start": v(546.43, -136.59) * mm, "end": v(547.15, -137.55) * mm});
            skLineSegment(sketch, "E552", {"start": v(547.15, -137.55) * mm, "end": v(548.06, -138.53) * mm});
            skLineSegment(sketch, "E553", {"start": v(548.06, -138.53) * mm, "end": v(549.18, -139.5) * mm});
            skLineSegment(sketch, "E554", {"start": v(549.18, -139.5) * mm, "end": v(556.09, -145.11) * mm});
            skLineSegment(sketch, "E555", {"start": v(556.09, -145.11) * mm, "end": v(557.13, -145.93) * mm});
            skLineSegment(sketch, "E556", {"start": v(557.13, -145.93) * mm, "end": v(558.38, -146.76) * mm});
            skLineSegment(sketch, "E557", {"start": v(558.38, -146.76) * mm, "end": v(559.82, -147.58) * mm});
            skLineSegment(sketch, "E558", {"start": v(559.82, -147.58) * mm, "end": v(561.46, -148.4) * mm});
            skLineSegment(sketch, "E559", {"start": v(561.46, -148.4) * mm, "end": v(561.7, -148.5) * mm});
            skLineSegment(sketch, "E560", {"start": v(561.7, -148.5) * mm, "end": v(563.13, -149.17) * mm});
            skLineSegment(sketch, "E561", {"start": v(563.13, -149.17) * mm, "end": v(564.67, -149.9) * mm});
            skLineSegment(sketch, "E562", {"start": v(564.67, -149.9) * mm, "end": v(566.32, -150.74) * mm});
            skLineSegment(sketch, "E563", {"start": v(566.32, -150.74) * mm, "end": v(568.08, -151.65) * mm});
            skLineSegment(sketch, "E564", {"start": v(568.08, -151.65) * mm, "end": v(569.94, -152.66) * mm});
            skLineSegment(sketch, "E565", {"start": v(569.94, -152.66) * mm, "end": v(571.9, -153.76) * mm});
            skLineSegment(sketch, "E566", {"start": v(571.9, -153.76) * mm, "end": v(573.97, -154.97) * mm});
            skLineSegment(sketch, "E567", {"start": v(573.97, -154.97) * mm, "end": v(576.14, -156.27) * mm});
            skLineSegment(sketch, "E568", {"start": v(576.14, -156.27) * mm, "end": v(578.4, -157.68) * mm});
            skLineSegment(sketch, "E569", {"start": v(578.4, -157.68) * mm, "end": v(580.76, -159.2) * mm});
            skLineSegment(sketch, "E570", {"start": v(580.76, -159.2) * mm, "end": v(583.2, -160.84) * mm});
            skLineSegment(sketch, "E571", {"start": v(583.2, -160.84) * mm, "end": v(585.73, -162.59) * mm});
            skLineSegment(sketch, "E572", {"start": v(585.73, -162.59) * mm, "end": v(588.35, -164.45) * mm});
            skLineSegment(sketch, "E573", {"start": v(588.35, -164.45) * mm, "end": v(591.05, -166.44) * mm});
            skLineSegment(sketch, "E574", {"start": v(591.05, -166.44) * mm, "end": v(593.82, -168.55) * mm});
            skLineSegment(sketch, "E575", {"start": v(593.82, -168.55) * mm, "end": v(596.67, -170.8) * mm});
            skLineSegment(sketch, "E576", {"start": v(596.67, -170.8) * mm, "end": v(599.6, -173.16) * mm});
            skLineSegment(sketch, "E577", {"start": v(599.6, -173.16) * mm, "end": v(602.58, -175.67) * mm});
            skLineSegment(sketch, "E578", {"start": v(602.58, -175.67) * mm, "end": v(605.64, -178.3) * mm});
            skLineSegment(sketch, "E579", {"start": v(605.64, -178.3) * mm, "end": v(608.75, -181.08) * mm});
            skLineSegment(sketch, "E580", {"start": v(608.75, -181.08) * mm, "end": v(611.92, -184) * mm});
            skLineSegment(sketch, "E581", {"start": v(611.92, -184) * mm, "end": v(615.15, -187.06) * mm});
            skLineSegment(sketch, "E582", {"start": v(615.15, -187.06) * mm, "end": v(618.43, -190.26) * mm});
            skLineSegment(sketch, "E583", {"start": v(618.43, -190.26) * mm, "end": v(621.75, -193.62) * mm});
            skLineSegment(sketch, "E584", {"start": v(621.75, -193.62) * mm, "end": v(625.12, -197.12) * mm});
            skLineSegment(sketch, "E585", {"start": v(625.12, -197.12) * mm, "end": v(628.52, -200.77) * mm});
            skLineSegment(sketch, "E586", {"start": v(628.52, -200.77) * mm, "end": v(631.96, -204.58) * mm});
            skLineSegment(sketch, "E587", {"start": v(631.96, -204.58) * mm, "end": v(635.43, -208.55) * mm});
            skLineSegment(sketch, "E588", {"start": v(635.43, -208.55) * mm, "end": v(638.93, -212.67) * mm});
            skLineSegment(sketch, "E589", {"start": v(638.93, -212.67) * mm, "end": v(642.45, -216.95) * mm});
            skLineSegment(sketch, "E590", {"start": v(642.45, -216.95) * mm, "end": v(646, -221.4) * mm});
            skLineSegment(sketch, "E591", {"start": v(646, -221.4) * mm, "end": v(649.54, -226) * mm});
            skLineSegment(sketch, "E592", {"start": v(649.54, -226) * mm, "end": v(653.1, -230.77) * mm});
            skLineSegment(sketch, "E593", {"start": v(653.1, -230.77) * mm, "end": v(656.68, -235.7) * mm});
            skLineSegment(sketch, "E594", {"start": v(656.68, -235.7) * mm, "end": v(660.25, -240.8) * mm});
            skLineSegment(sketch, "E595", {"start": v(660.25, -240.8) * mm, "end": v(663.82, -246.07) * mm});
            skLineSegment(sketch, "E596", {"start": v(663.82, -246.07) * mm, "end": v(667.38, -251.51) * mm});
            skLineSegment(sketch, "E597", {"start": v(667.38, -251.51) * mm, "end": v(670.93, -257.12) * mm});
            skLineSegment(sketch, "E598", {"start": v(670.93, -257.12) * mm, "end": v(674.47, -262.9) * mm});
            skLineSegment(sketch, "E599", {"start": v(461.87, -303.1) * mm, "end": v(462.53, -302.34) * mm});
            skLineSegment(sketch, "E600", {"start": v(462.53, -302.34) * mm, "end": v(470.17, -294.84) * mm});
            skLineSegment(sketch, "E601", {"start": v(470.17, -294.84) * mm, "end": v(470.97, -294.22) * mm});
            skLineSegment(sketch, "E602", {"start": v(470.97, -294.22) * mm, "end": v(471.93, -293.73) * mm});
            skLineSegment(sketch, "E603", {"start": v(471.93, -293.73) * mm, "end": v(481.93, -290.1) * mm});
            skLineSegment(sketch, "E604", {"start": v(481.93, -290.1) * mm, "end": v(482.97, -289.8) * mm});
            skLineSegment(sketch, "E605", {"start": v(482.97, -289.8) * mm, "end": v(484.15, -289.63) * mm});
            skLineSegment(sketch, "E606", {"start": v(484.15, -289.63) * mm, "end": v(485.49, -289.59) * mm});
            skLineSegment(sketch, "E607", {"start": v(485.49, -289.59) * mm, "end": v(486.97, -289.68) * mm});
            skLineSegment(sketch, "E608", {"start": v(486.97, -289.68) * mm, "end": v(495.82, -290.6) * mm});
            skLineSegment(sketch, "E609", {"start": v(495.82, -290.6) * mm, "end": v(497.14, -290.76) * mm});
            skLineSegment(sketch, "E610", {"start": v(497.14, -290.76) * mm, "end": v(498.6, -291.06) * mm});
            skLineSegment(sketch, "E611", {"start": v(498.6, -291.06) * mm, "end": v(500.2, -291.5) * mm});
            skLineSegment(sketch, "E612", {"start": v(500.2, -291.5) * mm, "end": v(501.94, -292.08) * mm});
            skLineSegment(sketch, "E613", {"start": v(501.94, -292.08) * mm, "end": v(502.2, -292.18) * mm});
            skLineSegment(sketch, "E614", {"start": v(502.2, -292.18) * mm, "end": v(503.67, -292.72) * mm});
            skLineSegment(sketch, "E615", {"start": v(503.67, -292.72) * mm, "end": v(505.28, -293.28) * mm});
            skLineSegment(sketch, "E616", {"start": v(505.28, -293.28) * mm, "end": v(507.03, -293.86) * mm});
            skLineSegment(sketch, "E617", {"start": v(507.03, -293.86) * mm, "end": v(508.92, -294.46) * mm});
            skLineSegment(sketch, "E618", {"start": v(508.92, -294.46) * mm, "end": v(510.95, -295.06) * mm});
            skLineSegment(sketch, "E619", {"start": v(510.95, -295.06) * mm, "end": v(513.13, -295.67) * mm});
            skLineSegment(sketch, "E620", {"start": v(513.13, -295.67) * mm, "end": v(515.44, -296.28) * mm});
            skLineSegment(sketch, "E621", {"start": v(515.44, -296.28) * mm, "end": v(517.9, -296.9) * mm});
            skLineSegment(sketch, "E622", {"start": v(517.9, -296.9) * mm, "end": v(520.5, -297.5) * mm});
            skLineSegment(sketch, "E623", {"start": v(520.5, -297.5) * mm, "end": v(523.23, -298.08) * mm});
            skLineSegment(sketch, "E624", {"start": v(523.23, -298.08) * mm, "end": v(526.11, -298.66) * mm});
            skLineSegment(sketch, "E625", {"start": v(526.11, -298.66) * mm, "end": v(529.14, -299.21) * mm});
            skLineSegment(sketch, "E626", {"start": v(529.14, -299.21) * mm, "end": v(532.31, -299.74) * mm});
            skLineSegment(sketch, "E627", {"start": v(532.31, -299.74) * mm, "end": v(535.62, -300.24) * mm});
            skLineSegment(sketch, "E628", {"start": v(535.62, -300.24) * mm, "end": v(539.08, -300.71) * mm});
            skLineSegment(sketch, "E629", {"start": v(539.08, -300.71) * mm, "end": v(542.68, -301.14) * mm});
            skLineSegment(sketch, "E630", {"start": v(542.68, -301.14) * mm, "end": v(546.42, -301.53) * mm});
            skLineSegment(sketch, "E631", {"start": v(546.42, -301.53) * mm, "end": v(550.3, -301.88) * mm});
            skLineSegment(sketch, "E632", {"start": v(550.3, -301.88) * mm, "end": v(554.33, -302.17) * mm});
            skLineSegment(sketch, "E633", {"start": v(554.33, -302.17) * mm, "end": v(558.5, -302.4) * mm});
            skLineSegment(sketch, "E634", {"start": v(558.5, -302.4) * mm, "end": v(562.8, -302.59) * mm});
            skLineSegment(sketch, "E635", {"start": v(562.8, -302.59) * mm, "end": v(567.25, -302.7) * mm});
            skLineSegment(sketch, "E636", {"start": v(567.25, -302.7) * mm, "end": v(571.83, -302.76) * mm});
            skLineSegment(sketch, "E637", {"start": v(571.83, -302.76) * mm, "end": v(576.55, -302.74) * mm});
            skLineSegment(sketch, "E638", {"start": v(576.55, -302.74) * mm, "end": v(581.41, -302.64) * mm});
            skLineSegment(sketch, "E639", {"start": v(581.41, -302.64) * mm, "end": v(586.4, -302.46) * mm});
            skLineSegment(sketch, "E640", {"start": v(586.4, -302.46) * mm, "end": v(591.53, -302.2) * mm});
            skLineSegment(sketch, "E641", {"start": v(591.53, -302.2) * mm, "end": v(596.78, -301.85) * mm});
            skLineSegment(sketch, "E642", {"start": v(596.78, -301.85) * mm, "end": v(602.17, -301.41) * mm});
            skLineSegment(sketch, "E643", {"start": v(602.17, -301.41) * mm, "end": v(607.69, -300.87) * mm});
            skLineSegment(sketch, "E644", {"start": v(607.69, -300.87) * mm, "end": v(613.33, -300.24) * mm});
            skLineSegment(sketch, "E645", {"start": v(613.33, -300.24) * mm, "end": v(619.1, -299.5) * mm});
            skLineSegment(sketch, "E646", {"start": v(619.1, -299.5) * mm, "end": v(625, -298.64) * mm});
            skLineSegment(sketch, "E647", {"start": v(625, -298.64) * mm, "end": v(631, -297.67) * mm});
            skLineSegment(sketch, "E648", {"start": v(631, -297.67) * mm, "end": v(637.14, -296.6) * mm});
            skLineSegment(sketch, "E649", {"start": v(637.14, -296.6) * mm, "end": v(643.4, -295.4) * mm});
            skLineSegment(sketch, "E650", {"start": v(643.4, -295.4) * mm, "end": v(649.76, -294.06) * mm});
            skLineSegment(sketch, "E651", {"start": v(649.76, -294.06) * mm, "end": v(656.23, -292.6) * mm});
            skLineSegment(sketch, "E652", {"start": v(656.23, -292.6) * mm, "end": v(662.82, -291.02) * mm});
            skArc(sketch, "E653", {"start": v(662.82, -291.02) * mm, "mid": v(668.8, -277.02) * mm, "end": v(674.47, -262.9) * mm});
            skLineSegment(sketch, "E654", {"start": v(456.78, -310.72) * mm, "end": v(456.33, -311.62) * mm});
            skLineSegment(sketch, "E655", {"start": v(456.33, -311.62) * mm, "end": v(452.32, -321.55) * mm});
            skLineSegment(sketch, "E656", {"start": v(452.32, -321.55) * mm, "end": v(452.06, -322.53) * mm});
            skLineSegment(sketch, "E657", {"start": v(452.06, -322.53) * mm, "end": v(451.97, -323.6) * mm});
            skLineSegment(sketch, "E658", {"start": v(451.97, -323.6) * mm, "end": v(452.45, -334.23) * mm});
            skLineSegment(sketch, "E659", {"start": v(452.45, -334.23) * mm, "end": v(452.57, -335.3) * mm});
            skLineSegment(sketch, "E660", {"start": v(452.57, -335.3) * mm, "end": v(452.86, -336.46) * mm});
            skLineSegment(sketch, "E661", {"start": v(452.86, -336.46) * mm, "end": v(453.33, -337.71) * mm});
            skLineSegment(sketch, "E662", {"start": v(453.33, -337.71) * mm, "end": v(453.99, -339.05) * mm});
            skLineSegment(sketch, "E663", {"start": v(453.99, -339.05) * mm, "end": v(458.22, -346.87) * mm});
            skLineSegment(sketch, "E664", {"start": v(458.22, -346.87) * mm, "end": v(458.88, -348.03) * mm});
            skLineSegment(sketch, "E665", {"start": v(458.88, -348.03) * mm, "end": v(459.71, -349.27) * mm});
            skLineSegment(sketch, "E666", {"start": v(459.71, -349.27) * mm, "end": v(460.73, -350.58) * mm});
            skLineSegment(sketch, "E667", {"start": v(460.73, -350.58) * mm, "end": v(461.94, -351.96) * mm});
            skLineSegment(sketch, "E668", {"start": v(461.94, -351.96) * mm, "end": v(462.12, -352.16) * mm});
            skLineSegment(sketch, "E669", {"start": v(462.12, -352.16) * mm, "end": v(463.18, -353.31) * mm});
            skLineSegment(sketch, "E670", {"start": v(463.18, -353.31) * mm, "end": v(464.32, -354.59) * mm});
            skLineSegment(sketch, "E671", {"start": v(464.32, -354.59) * mm, "end": v(465.53, -355.98) * mm});
            skLineSegment(sketch, "E672", {"start": v(465.53, -355.98) * mm, "end": v(466.8, -357.5) * mm});
            skLineSegment(sketch, "E673", {"start": v(466.8, -357.5) * mm, "end": v(468.13, -359.15) * mm});
            skLineSegment(sketch, "E674", {"start": v(468.13, -359.15) * mm, "end": v(469.53, -360.92) * mm});
            skLineSegment(sketch, "E675", {"start": v(469.53, -360.92) * mm, "end": v(470.98, -362.82) * mm});
            skLineSegment(sketch, "E676", {"start": v(470.98, -362.82) * mm, "end": v(472.48, -364.86) * mm});
            skLineSegment(sketch, "E677", {"start": v(472.48, -364.86) * mm, "end": v(474.03, -367.03) * mm});
            skLineSegment(sketch, "E678", {"start": v(474.03, -367.03) * mm, "end": v(475.62, -369.33) * mm});
            skLineSegment(sketch, "E679", {"start": v(475.62, -369.33) * mm, "end": v(477.26, -371.78) * mm});
            skLineSegment(sketch, "E680", {"start": v(477.26, -371.78) * mm, "end": v(478.93, -374.36) * mm});
            skLineSegment(sketch, "E681", {"start": v(478.93, -374.36) * mm, "end": v(480.63, -377.09) * mm});
            skLineSegment(sketch, "E682", {"start": v(480.63, -377.09) * mm, "end": v(482.36, -379.95) * mm});
            skLineSegment(sketch, "E683", {"start": v(482.36, -379.95) * mm, "end": v(484.12, -382.97) * mm});
            skLineSegment(sketch, "E684", {"start": v(484.12, -382.97) * mm, "end": v(485.9, -386.13) * mm});
            skLineSegment(sketch, "E685", {"start": v(485.9, -386.13) * mm, "end": v(487.69, -389.44) * mm});
            skLineSegment(sketch, "E686", {"start": v(487.69, -389.44) * mm, "end": v(489.49, -392.9) * mm});
            skLineSegment(sketch, "E687", {"start": v(489.49, -392.9) * mm, "end": v(491.3, -396.5) * mm});
            skLineSegment(sketch, "E688", {"start": v(491.3, -396.5) * mm, "end": v(493.12, -400.26) * mm});
            skLineSegment(sketch, "E689", {"start": v(493.12, -400.26) * mm, "end": v(494.93, -404.17) * mm});
            skLineSegment(sketch, "E690", {"start": v(494.93, -404.17) * mm, "end": v(496.74, -408.23) * mm});
            skLineSegment(sketch, "E691", {"start": v(496.74, -408.23) * mm, "end": v(498.54, -412.44) * mm});
            skLineSegment(sketch, "E692", {"start": v(498.54, -412.44) * mm, "end": v(500.33, -416.81) * mm});
            skLineSegment(sketch, "E693", {"start": v(500.33, -416.81) * mm, "end": v(502.1, -421.34) * mm});
            skLineSegment(sketch, "E694", {"start": v(502.1, -421.34) * mm, "end": v(503.85, -426.02) * mm});
            skLineSegment(sketch, "E695", {"start": v(503.85, -426.02) * mm, "end": v(505.57, -430.85) * mm});
            skLineSegment(sketch, "E696", {"start": v(505.57, -430.85) * mm, "end": v(507.26, -435.84) * mm});
            skLineSegment(sketch, "E697", {"start": v(507.26, -435.84) * mm, "end": v(508.9, -440.99) * mm});
            skLineSegment(sketch, "E698", {"start": v(508.9, -440.99) * mm, "end": v(510.52, -446.3) * mm});
            skLineSegment(sketch, "E699", {"start": v(510.52, -446.3) * mm, "end": v(512.1, -451.75) * mm});
            skLineSegment(sketch, "E700", {"start": v(512.1, -451.75) * mm, "end": v(513.61, -457.37) * mm});
            skLineSegment(sketch, "E701", {"start": v(513.61, -457.37) * mm, "end": v(515.08, -463.14) * mm});
            skLineSegment(sketch, "E702", {"start": v(515.08, -463.14) * mm, "end": v(516.5, -469.06) * mm});
            skLineSegment(sketch, "E703", {"start": v(516.5, -469.06) * mm, "end": v(517.84, -475.14) * mm});
            skLineSegment(sketch, "E704", {"start": v(517.84, -475.14) * mm, "end": v(519.12, -481.38) * mm});
            skLineSegment(sketch, "E705", {"start": v(519.12, -481.38) * mm, "end": v(520.33, -487.76) * mm});
            skLineSegment(sketch, "E706", {"start": v(520.33, -487.76) * mm, "end": v(521.47, -494.3) * mm});
            skLineSegment(sketch, "E707", {"start": v(521.47, -494.3) * mm, "end": v(522.52, -501) * mm});
            skLineSegment(sketch, "E708", {"start": v(310.72, -456.78) * mm, "end": v(311.62, -456.33) * mm});
            skLineSegment(sketch, "E709", {"start": v(311.62, -456.33) * mm, "end": v(321.55, -452.32) * mm});
            skLineSegment(sketch, "E710", {"start": v(321.55, -452.32) * mm, "end": v(322.53, -452.06) * mm});
            skLineSegment(sketch, "E711", {"start": v(322.53, -452.06) * mm, "end": v(323.6, -451.97) * mm});
            skLineSegment(sketch, "E712", {"start": v(323.6, -451.97) * mm, "end": v(334.23, -452.45) * mm});
            skLineSegment(sketch, "E713", {"start": v(334.23, -452.45) * mm, "end": v(335.3, -452.57) * mm});
            skLineSegment(sketch, "E714", {"start": v(335.3, -452.57) * mm, "end": v(336.46, -452.86) * mm});
            skLineSegment(sketch, "E715", {"start": v(336.46, -452.86) * mm, "end": v(337.71, -453.33) * mm});
            skLineSegment(sketch, "E716", {"start": v(337.71, -453.33) * mm, "end": v(339.05, -453.99) * mm});
            skLineSegment(sketch, "E717", {"start": v(339.05, -453.99) * mm, "end": v(346.87, -458.22) * mm});
            skLineSegment(sketch, "E718", {"start": v(346.87, -458.22) * mm, "end": v(348.03, -458.88) * mm});
            skLineSegment(sketch, "E719", {"start": v(348.03, -458.88) * mm, "end": v(349.27, -459.71) * mm});
            skLineSegment(sketch, "E720", {"start": v(349.27, -459.71) * mm, "end": v(350.58, -460.73) * mm});
            skLineSegment(sketch, "E721", {"start": v(350.58, -460.73) * mm, "end": v(351.96, -461.94) * mm});
            skLineSegment(sketch, "E722", {"start": v(351.96, -461.94) * mm, "end": v(352.16, -462.12) * mm});
            skLineSegment(sketch, "E723", {"start": v(352.16, -462.12) * mm, "end": v(353.31, -463.18) * mm});
            skLineSegment(sketch, "E724", {"start": v(353.31, -463.18) * mm, "end": v(354.59, -464.32) * mm});
            skLineSegment(sketch, "E725", {"start": v(354.59, -464.32) * mm, "end": v(355.98, -465.53) * mm});
            skLineSegment(sketch, "E726", {"start": v(355.98, -465.53) * mm, "end": v(357.5, -466.8) * mm});
            skLineSegment(sketch, "E727", {"start": v(357.5, -466.8) * mm, "end": v(359.15, -468.13) * mm});
            skLineSegment(sketch, "E728", {"start": v(359.15, -468.13) * mm, "end": v(360.92, -469.53) * mm});
            skLineSegment(sketch, "E729", {"start": v(360.92, -469.53) * mm, "end": v(362.82, -470.98) * mm});
            skLineSegment(sketch, "E730", {"start": v(362.82, -470.98) * mm, "end": v(364.86, -472.48) * mm});
            skLineSegment(sketch, "E731", {"start": v(364.86, -472.48) * mm, "end": v(367.03, -474.03) * mm});
            skLineSegment(sketch, "E732", {"start": v(367.03, -474.03) * mm, "end": v(369.33, -475.62) * mm});
            skLineSegment(sketch, "E733", {"start": v(369.33, -475.62) * mm, "end": v(371.78, -477.26) * mm});
            skLineSegment(sketch, "E734", {"start": v(371.78, -477.26) * mm, "end": v(374.36, -478.93) * mm});
            skLineSegment(sketch, "E735", {"start": v(374.36, -478.93) * mm, "end": v(377.09, -480.63) * mm});
            skLineSegment(sketch, "E736", {"start": v(377.09, -480.63) * mm, "end": v(379.95, -482.36) * mm});
            skLineSegment(sketch, "E737", {"start": v(379.95, -482.36) * mm, "end": v(382.97, -484.12) * mm});
            skLineSegment(sketch, "E738", {"start": v(382.97, -484.12) * mm, "end": v(386.13, -485.9) * mm});
            skLineSegment(sketch, "E739", {"start": v(386.13, -485.9) * mm, "end": v(389.44, -487.69) * mm});
            skLineSegment(sketch, "E740", {"start": v(389.44, -487.69) * mm, "end": v(392.9, -489.49) * mm});
            skLineSegment(sketch, "E741", {"start": v(392.9, -489.49) * mm, "end": v(396.5, -491.3) * mm});
            skLineSegment(sketch, "E742", {"start": v(396.5, -491.3) * mm, "end": v(400.26, -493.12) * mm});
            skLineSegment(sketch, "E743", {"start": v(400.26, -493.12) * mm, "end": v(404.17, -494.93) * mm});
            skLineSegment(sketch, "E744", {"start": v(404.17, -494.93) * mm, "end": v(408.23, -496.74) * mm});
            skLineSegment(sketch, "E745", {"start": v(408.23, -496.74) * mm, "end": v(412.44, -498.54) * mm});
            skLineSegment(sketch, "E746", {"start": v(412.44, -498.54) * mm, "end": v(416.81, -500.33) * mm});
            skLineSegment(sketch, "E747", {"start": v(416.81, -500.33) * mm, "end": v(421.34, -502.1) * mm});
            skLineSegment(sketch, "E748", {"start": v(421.34, -502.1) * mm, "end": v(426.02, -503.85) * mm});
            skLineSegment(sketch, "E749", {"start": v(426.02, -503.85) * mm, "end": v(430.85, -505.57) * mm});
            skLineSegment(sketch, "E750", {"start": v(430.85, -505.57) * mm, "end": v(435.84, -507.26) * mm});
            skLineSegment(sketch, "E751", {"start": v(435.84, -507.26) * mm, "end": v(440.99, -508.9) * mm});
            skLineSegment(sketch, "E752", {"start": v(440.99, -508.9) * mm, "end": v(446.3, -510.52) * mm});
            skLineSegment(sketch, "E753", {"start": v(446.3, -510.52) * mm, "end": v(451.75, -512.1) * mm});
            skLineSegment(sketch, "E754", {"start": v(451.75, -512.1) * mm, "end": v(457.37, -513.61) * mm});
            skLineSegment(sketch, "E755", {"start": v(457.37, -513.61) * mm, "end": v(463.14, -515.08) * mm});
            skLineSegment(sketch, "E756", {"start": v(463.14, -515.08) * mm, "end": v(469.06, -516.5) * mm});
            skLineSegment(sketch, "E757", {"start": v(469.06, -516.5) * mm, "end": v(475.14, -517.84) * mm});
            skLineSegment(sketch, "E758", {"start": v(475.14, -517.84) * mm, "end": v(481.38, -519.12) * mm});
            skLineSegment(sketch, "E759", {"start": v(481.38, -519.12) * mm, "end": v(487.76, -520.33) * mm});
            skLineSegment(sketch, "E760", {"start": v(487.76, -520.33) * mm, "end": v(494.3, -521.47) * mm});
            skLineSegment(sketch, "E761", {"start": v(494.3, -521.47) * mm, "end": v(501, -522.52) * mm});
            skArc(sketch, "E762", {"start": v(501, -522.52) * mm, "mid": v(511.87, -511.87) * mm, "end": v(522.52, -501) * mm});
            skLineSegment(sketch, "E763", {"start": v(303.1, -461.87) * mm, "end": v(302.34, -462.53) * mm});
            skLineSegment(sketch, "E764", {"start": v(302.34, -462.53) * mm, "end": v(294.84, -470.17) * mm});
            skLineSegment(sketch, "E765", {"start": v(294.84, -470.17) * mm, "end": v(294.22, -470.97) * mm});
            skLineSegment(sketch, "E766", {"start": v(294.22, -470.97) * mm, "end": v(293.73, -471.93) * mm});
            skLineSegment(sketch, "E767", {"start": v(293.73, -471.93) * mm, "end": v(290.1, -481.93) * mm});
            skLineSegment(sketch, "E768", {"start": v(290.1, -481.93) * mm, "end": v(289.8, -482.97) * mm});
            skLineSegment(sketch, "E769", {"start": v(289.8, -482.97) * mm, "end": v(289.63, -484.15) * mm});
            skLineSegment(sketch, "E770", {"start": v(289.63, -484.15) * mm, "end": v(289.59, -485.49) * mm});
            skLineSegment(sketch, "E771", {"start": v(289.59, -485.49) * mm, "end": v(289.68, -486.97) * mm});
            skLineSegment(sketch, "E772", {"start": v(289.68, -486.97) * mm, "end": v(290.6, -495.82) * mm});
            skLineSegment(sketch, "E773", {"start": v(290.6, -495.82) * mm, "end": v(290.76, -497.14) * mm});
            skLineSegment(sketch, "E774", {"start": v(290.76, -497.14) * mm, "end": v(291.06, -498.6) * mm});
            skLineSegment(sketch, "E775", {"start": v(291.06, -498.6) * mm, "end": v(291.5, -500.2) * mm});
            skLineSegment(sketch, "E776", {"start": v(291.5, -500.2) * mm, "end": v(292.08, -501.94) * mm});
            skLineSegment(sketch, "E777", {"start": v(292.08, -501.94) * mm, "end": v(292.18, -502.2) * mm});
            skLineSegment(sketch, "E778", {"start": v(292.18, -502.2) * mm, "end": v(292.72, -503.67) * mm});
            skLineSegment(sketch, "E779", {"start": v(292.72, -503.67) * mm, "end": v(293.28, -505.28) * mm});
            skLineSegment(sketch, "E780", {"start": v(293.28, -505.28) * mm, "end": v(293.86, -507.03) * mm});
            skLineSegment(sketch, "E781", {"start": v(293.86, -507.03) * mm, "end": v(294.46, -508.92) * mm});
            skLineSegment(sketch, "E782", {"start": v(294.46, -508.92) * mm, "end": v(295.06, -510.95) * mm});
            skLineSegment(sketch, "E783", {"start": v(295.06, -510.95) * mm, "end": v(295.67, -513.13) * mm});
            skLineSegment(sketch, "E784", {"start": v(295.67, -513.13) * mm, "end": v(296.28, -515.44) * mm});
            skLineSegment(sketch, "E785", {"start": v(296.28, -515.44) * mm, "end": v(296.9, -517.9) * mm});
            skLineSegment(sketch, "E786", {"start": v(296.9, -517.9) * mm, "end": v(297.5, -520.5) * mm});
            skLineSegment(sketch, "E787", {"start": v(297.5, -520.5) * mm, "end": v(298.08, -523.23) * mm});
            skLineSegment(sketch, "E788", {"start": v(298.08, -523.23) * mm, "end": v(298.66, -526.11) * mm});
            skLineSegment(sketch, "E789", {"start": v(298.66, -526.11) * mm, "end": v(299.21, -529.14) * mm});
            skLineSegment(sketch, "E790", {"start": v(299.21, -529.14) * mm, "end": v(299.74, -532.31) * mm});
            skLineSegment(sketch, "E791", {"start": v(299.74, -532.31) * mm, "end": v(300.24, -535.62) * mm});
            skLineSegment(sketch, "E792", {"start": v(300.24, -535.62) * mm, "end": v(300.71, -539.08) * mm});
            skLineSegment(sketch, "E793", {"start": v(300.71, -539.08) * mm, "end": v(301.14, -542.68) * mm});
            skLineSegment(sketch, "E794", {"start": v(301.14, -542.68) * mm, "end": v(301.53, -546.42) * mm});
            skLineSegment(sketch, "E795", {"start": v(301.53, -546.42) * mm, "end": v(301.88, -550.3) * mm});
            skLineSegment(sketch, "E796", {"start": v(301.88, -550.3) * mm, "end": v(302.17, -554.33) * mm});
            skLineSegment(sketch, "E797", {"start": v(302.17, -554.33) * mm, "end": v(302.4, -558.5) * mm});
            skLineSegment(sketch, "E798", {"start": v(302.4, -558.5) * mm, "end": v(302.59, -562.8) * mm});
            skLineSegment(sketch, "E799", {"start": v(302.59, -562.8) * mm, "end": v(302.7, -567.25) * mm});
            skLineSegment(sketch, "E800", {"start": v(302.7, -567.25) * mm, "end": v(302.76, -571.83) * mm});
            skLineSegment(sketch, "E801", {"start": v(302.76, -571.83) * mm, "end": v(302.74, -576.55) * mm});
            skLineSegment(sketch, "E802", {"start": v(302.74, -576.55) * mm, "end": v(302.64, -581.41) * mm});
            skLineSegment(sketch, "E803", {"start": v(302.64, -581.41) * mm, "end": v(302.46, -586.4) * mm});
            skLineSegment(sketch, "E804", {"start": v(302.46, -586.4) * mm, "end": v(302.2, -591.53) * mm});
            skLineSegment(sketch, "E805", {"start": v(302.2, -591.53) * mm, "end": v(301.85, -596.78) * mm});
            skLineSegment(sketch, "E806", {"start": v(301.85, -596.78) * mm, "end": v(301.41, -602.17) * mm});
            skLineSegment(sketch, "E807", {"start": v(301.41, -602.17) * mm, "end": v(300.87, -607.69) * mm});
            skLineSegment(sketch, "E808", {"start": v(300.87, -607.69) * mm, "end": v(300.24, -613.33) * mm});
            skLineSegment(sketch, "E809", {"start": v(300.24, -613.33) * mm, "end": v(299.5, -619.1) * mm});
            skLineSegment(sketch, "E810", {"start": v(299.5, -619.1) * mm, "end": v(298.64, -625) * mm});
            skLineSegment(sketch, "E811", {"start": v(298.64, -625) * mm, "end": v(297.67, -631) * mm});
            skLineSegment(sketch, "E812", {"start": v(297.67, -631) * mm, "end": v(296.6, -637.14) * mm});
            skLineSegment(sketch, "E813", {"start": v(296.6, -637.14) * mm, "end": v(295.4, -643.4) * mm});
            skLineSegment(sketch, "E814", {"start": v(295.4, -643.4) * mm, "end": v(294.06, -649.76) * mm});
            skLineSegment(sketch, "E815", {"start": v(294.06, -649.76) * mm, "end": v(292.6, -656.23) * mm});
            skLineSegment(sketch, "E816", {"start": v(292.6, -656.23) * mm, "end": v(291.02, -662.82) * mm});
            skLineSegment(sketch, "E817", {"start": v(112.27, -540.92) * mm, "end": v(113.27, -540.85) * mm});
            skLineSegment(sketch, "E818", {"start": v(113.27, -540.85) * mm, "end": v(123.98, -540.94) * mm});
            skLineSegment(sketch, "E819", {"start": v(123.98, -540.94) * mm, "end": v(124.98, -541.07) * mm});
            skLineSegment(sketch, "E820", {"start": v(124.98, -541.07) * mm, "end": v(126, -541.4) * mm});
            skLineSegment(sketch, "E821", {"start": v(126, -541.4) * mm, "end": v(135.64, -545.92) * mm});
            skLineSegment(sketch, "E822", {"start": v(135.64, -545.92) * mm, "end": v(136.59, -546.43) * mm});
            skLineSegment(sketch, "E823", {"start": v(136.59, -546.43) * mm, "end": v(137.55, -547.15) * mm});
            skLineSegment(sketch, "E824", {"start": v(137.55, -547.15) * mm, "end": v(138.53, -548.06) * mm});
            skLineSegment(sketch, "E825", {"start": v(138.53, -548.06) * mm, "end": v(139.5, -549.18) * mm});
            skLineSegment(sketch, "E826", {"start": v(139.5, -549.18) * mm, "end": v(145.11, -556.09) * mm});
            skLineSegment(sketch, "E827", {"start": v(145.11, -556.09) * mm, "end": v(145.93, -557.13) * mm});
            skLineSegment(sketch, "E828", {"start": v(145.93, -557.13) * mm, "end": v(146.76, -558.38) * mm});
            skLineSegment(sketch, "E829", {"start": v(146.76, -558.38) * mm, "end": v(147.58, -559.82) * mm});
            skLineSegment(sketch, "E830", {"start": v(147.58, -559.82) * mm, "end": v(148.4, -561.46) * mm});
            skLineSegment(sketch, "E831", {"start": v(148.4, -561.46) * mm, "end": v(148.5, -561.7) * mm});
            skLineSegment(sketch, "E832", {"start": v(148.5, -561.7) * mm, "end": v(149.17, -563.13) * mm});
            skLineSegment(sketch, "E833", {"start": v(149.17, -563.13) * mm, "end": v(149.9, -564.67) * mm});
            skLineSegment(sketch, "E834", {"start": v(149.9, -564.67) * mm, "end": v(150.74, -566.32) * mm});
            skLineSegment(sketch, "E835", {"start": v(150.74, -566.32) * mm, "end": v(151.65, -568.08) * mm});
            skLineSegment(sketch, "E836", {"start": v(151.65, -568.08) * mm, "end": v(152.66, -569.94) * mm});
            skLineSegment(sketch, "E837", {"start": v(152.66, -569.94) * mm, "end": v(153.76, -571.9) * mm});
            skLineSegment(sketch, "E838", {"start": v(153.76, -571.9) * mm, "end": v(154.97, -573.97) * mm});
            skLineSegment(sketch, "E839", {"start": v(154.97, -573.97) * mm, "end": v(156.27, -576.14) * mm});
            skLineSegment(sketch, "E840", {"start": v(156.27, -576.14) * mm, "end": v(157.68, -578.4) * mm});
            skLineSegment(sketch, "E841", {"start": v(157.68, -578.4) * mm, "end": v(159.2, -580.76) * mm});
            skLineSegment(sketch, "E842", {"start": v(159.2, -580.76) * mm, "end": v(160.84, -583.2) * mm});
            skLineSegment(sketch, "E843", {"start": v(160.84, -583.2) * mm, "end": v(162.59, -585.73) * mm});
            skLineSegment(sketch, "E844", {"start": v(162.59, -585.73) * mm, "end": v(164.45, -588.35) * mm});
            skLineSegment(sketch, "E845", {"start": v(164.45, -588.35) * mm, "end": v(166.44, -591.05) * mm});
            skLineSegment(sketch, "E846", {"start": v(166.44, -591.05) * mm, "end": v(168.55, -593.82) * mm});
            skLineSegment(sketch, "E847", {"start": v(168.55, -593.82) * mm, "end": v(170.8, -596.67) * mm});
            skLineSegment(sketch, "E848", {"start": v(170.8, -596.67) * mm, "end": v(173.16, -599.6) * mm});
            skLineSegment(sketch, "E849", {"start": v(173.16, -599.6) * mm, "end": v(175.67, -602.58) * mm});
            skLineSegment(sketch, "E850", {"start": v(175.67, -602.58) * mm, "end": v(178.3, -605.64) * mm});
            skLineSegment(sketch, "E851", {"start": v(178.3, -605.64) * mm, "end": v(181.08, -608.75) * mm});
            skLineSegment(sketch, "E852", {"start": v(181.08, -608.75) * mm, "end": v(184, -611.92) * mm});
            skLineSegment(sketch, "E853", {"start": v(184, -611.92) * mm, "end": v(187.06, -615.15) * mm});
            skLineSegment(sketch, "E854", {"start": v(187.06, -615.15) * mm, "end": v(190.26, -618.43) * mm});
            skLineSegment(sketch, "E855", {"start": v(190.26, -618.43) * mm, "end": v(193.62, -621.75) * mm});
            skLineSegment(sketch, "E856", {"start": v(193.62, -621.75) * mm, "end": v(197.12, -625.12) * mm});
            skLineSegment(sketch, "E857", {"start": v(197.12, -625.12) * mm, "end": v(200.77, -628.52) * mm});
            skLineSegment(sketch, "E858", {"start": v(200.77, -628.52) * mm, "end": v(204.58, -631.96) * mm});
            skLineSegment(sketch, "E859", {"start": v(204.58, -631.96) * mm, "end": v(208.55, -635.43) * mm});
            skLineSegment(sketch, "E860", {"start": v(208.55, -635.43) * mm, "end": v(212.67, -638.93) * mm});
            skLineSegment(sketch, "E861", {"start": v(212.67, -638.93) * mm, "end": v(216.95, -642.45) * mm});
            skLineSegment(sketch, "E862", {"start": v(216.95, -642.45) * mm, "end": v(221.4, -646) * mm});
            skLineSegment(sketch, "E863", {"start": v(221.4, -646) * mm, "end": v(226, -649.54) * mm});
            skLineSegment(sketch, "E864", {"start": v(226, -649.54) * mm, "end": v(230.77, -653.1) * mm});
            skLineSegment(sketch, "E865", {"start": v(230.77, -653.1) * mm, "end": v(235.7, -656.68) * mm});
            skLineSegment(sketch, "E866", {"start": v(235.7, -656.68) * mm, "end": v(240.8, -660.25) * mm});
            skLineSegment(sketch, "E867", {"start": v(240.8, -660.25) * mm, "end": v(246.07, -663.82) * mm});
            skLineSegment(sketch, "E868", {"start": v(246.07, -663.82) * mm, "end": v(251.51, -667.38) * mm});
            skLineSegment(sketch, "E869", {"start": v(251.51, -667.38) * mm, "end": v(257.12, -670.93) * mm});
            skLineSegment(sketch, "E870", {"start": v(257.12, -670.93) * mm, "end": v(262.9, -674.47) * mm});
            skArc(sketch, "E871", {"start": v(262.9, -674.47) * mm, "mid": v(277.02, -668.8) * mm, "end": v(291.02, -662.82) * mm});
            skLineSegment(sketch, "E872", {"start": v(103.28, -542.7) * mm, "end": v(102.33, -543.03) * mm});
            skLineSegment(sketch, "E873", {"start": v(102.33, -543.03) * mm, "end": v(92.47, -547.21) * mm});
            skLineSegment(sketch, "E874", {"start": v(92.47, -547.21) * mm, "end": v(91.6, -547.71) * mm});
            skLineSegment(sketch, "E875", {"start": v(91.6, -547.71) * mm, "end": v(90.77, -548.41) * mm});
            skLineSegment(sketch, "E876", {"start": v(90.77, -548.41) * mm, "end": v(83.6, -556.27) * mm});
            skLineSegment(sketch, "E877", {"start": v(83.6, -556.27) * mm, "end": v(82.92, -557.1) * mm});
            skLineSegment(sketch, "E878", {"start": v(82.92, -557.1) * mm, "end": v(82.3, -558.13) * mm});
            skLineSegment(sketch, "E879", {"start": v(82.3, -558.13) * mm, "end": v(81.75, -559.35) * mm});
            skLineSegment(sketch, "E880", {"start": v(81.75, -559.35) * mm, "end": v(81.27, -560.76) * mm});
            skLineSegment(sketch, "E881", {"start": v(81.27, -560.76) * mm, "end": v(78.74, -569.29) * mm});
            skLineSegment(sketch, "E882", {"start": v(78.74, -569.29) * mm, "end": v(78.38, -570.57) * mm});
            skLineSegment(sketch, "E883", {"start": v(78.38, -570.57) * mm, "end": v(78.1, -572.03) * mm});
            skLineSegment(sketch, "E884", {"start": v(78.1, -572.03) * mm, "end": v(77.89, -573.68) * mm});
            skLineSegment(sketch, "E885", {"start": v(77.89, -573.68) * mm, "end": v(77.77, -575.5) * mm});
            skLineSegment(sketch, "E886", {"start": v(77.77, -575.5) * mm, "end": v(77.76, -575.78) * mm});
            skLineSegment(sketch, "E887", {"start": v(77.76, -575.78) * mm, "end": v(77.7, -577.35) * mm});
            skLineSegment(sketch, "E888", {"start": v(77.7, -577.35) * mm, "end": v(77.6, -579.06) * mm});
            skLineSegment(sketch, "E889", {"start": v(77.6, -579.06) * mm, "end": v(77.46, -580.9) * mm});
            skLineSegment(sketch, "E890", {"start": v(77.46, -580.9) * mm, "end": v(77.29, -582.87) * mm});
            skLineSegment(sketch, "E891", {"start": v(77.29, -582.87) * mm, "end": v(77.07, -584.98) * mm});
            skLineSegment(sketch, "E892", {"start": v(77.07, -584.98) * mm, "end": v(76.8, -587.21) * mm});
            skLineSegment(sketch, "E893", {"start": v(76.8, -587.21) * mm, "end": v(76.48, -589.59) * mm});
            skLineSegment(sketch, "E894", {"start": v(76.48, -589.59) * mm, "end": v(76.1, -592.09) * mm});
            skLineSegment(sketch, "E895", {"start": v(76.1, -592.09) * mm, "end": v(75.66, -594.72) * mm});
            skLineSegment(sketch, "E896", {"start": v(75.66, -594.72) * mm, "end": v(75.16, -597.47) * mm});
            skLineSegment(sketch, "E897", {"start": v(75.16, -597.47) * mm, "end": v(74.59, -600.36) * mm});
            skLineSegment(sketch, "E898", {"start": v(74.59, -600.36) * mm, "end": v(73.94, -603.37) * mm});
            skLineSegment(sketch, "E899", {"start": v(73.94, -603.37) * mm, "end": v(73.22, -606.5) * mm});
            skLineSegment(sketch, "E900", {"start": v(73.22, -606.5) * mm, "end": v(72.41, -609.75) * mm});
            skLineSegment(sketch, "E901", {"start": v(72.41, -609.75) * mm, "end": v(71.52, -613.12) * mm});
            skLineSegment(sketch, "E902", {"start": v(71.52, -613.12) * mm, "end": v(70.54, -616.61) * mm});
            skLineSegment(sketch, "E903", {"start": v(70.54, -616.61) * mm, "end": v(69.47, -620.22) * mm});
            skLineSegment(sketch, "E904", {"start": v(69.47, -620.22) * mm, "end": v(68.3, -623.94) * mm});
            skLineSegment(sketch, "E905", {"start": v(68.3, -623.94) * mm, "end": v(67.03, -627.77) * mm});
            skLineSegment(sketch, "E906", {"start": v(67.03, -627.77) * mm, "end": v(65.66, -631.71) * mm});
            skLineSegment(sketch, "E907", {"start": v(65.66, -631.71) * mm, "end": v(64.18, -635.76) * mm});
            skLineSegment(sketch, "E908", {"start": v(64.18, -635.76) * mm, "end": v(62.59, -639.91) * mm});
            skLineSegment(sketch, "E909", {"start": v(62.59, -639.91) * mm, "end": v(60.88, -644.16) * mm});
            skLineSegment(sketch, "E910", {"start": v(60.88, -644.16) * mm, "end": v(59.05, -648.52) * mm});
            skLineSegment(sketch, "E911", {"start": v(59.05, -648.52) * mm, "end": v(57.1, -652.97) * mm});
            skLineSegment(sketch, "E912", {"start": v(57.1, -652.97) * mm, "end": v(55.03, -657.51) * mm});
            skLineSegment(sketch, "E913", {"start": v(55.03, -657.51) * mm, "end": v(52.83, -662.15) * mm});
            skLineSegment(sketch, "E914", {"start": v(52.83, -662.15) * mm, "end": v(50.5, -666.87) * mm});
            skLineSegment(sketch, "E915", {"start": v(50.5, -666.87) * mm, "end": v(48.03, -671.68) * mm});
            skLineSegment(sketch, "E916", {"start": v(48.03, -671.68) * mm, "end": v(45.42, -676.57) * mm});
            skLineSegment(sketch, "E917", {"start": v(45.42, -676.57) * mm, "end": v(42.67, -681.54) * mm});
            skLineSegment(sketch, "E918", {"start": v(42.67, -681.54) * mm, "end": v(39.77, -686.59) * mm});
            skLineSegment(sketch, "E919", {"start": v(39.77, -686.59) * mm, "end": v(36.73, -691.7) * mm});
            skLineSegment(sketch, "E920", {"start": v(36.73, -691.7) * mm, "end": v(33.54, -696.9) * mm});
            skLineSegment(sketch, "E921", {"start": v(33.54, -696.9) * mm, "end": v(30.2, -702.14) * mm});
            skLineSegment(sketch, "E922", {"start": v(30.2, -702.14) * mm, "end": v(26.7, -707.46) * mm});
            skLineSegment(sketch, "E923", {"start": v(26.7, -707.46) * mm, "end": v(23.03, -712.83) * mm});
            skLineSegment(sketch, "E924", {"start": v(23.03, -712.83) * mm, "end": v(19.2, -718.26) * mm});
            skLineSegment(sketch, "E925", {"start": v(19.2, -718.26) * mm, "end": v(15.22, -723.74) * mm});
            skLineSegment(sketch, "E926", {"start": v(-103.28, -542.7) * mm, "end": v(-102.33, -543.03) * mm});
            skLineSegment(sketch, "E927", {"start": v(-102.33, -543.03) * mm, "end": v(-92.47, -547.21) * mm});
            skLineSegment(sketch, "E928", {"start": v(-92.47, -547.21) * mm, "end": v(-91.6, -547.71) * mm});
            skLineSegment(sketch, "E929", {"start": v(-91.6, -547.71) * mm, "end": v(-90.77, -548.41) * mm});
            skLineSegment(sketch, "E930", {"start": v(-90.77, -548.41) * mm, "end": v(-83.6, -556.27) * mm});
            skLineSegment(sketch, "E931", {"start": v(-83.6, -556.27) * mm, "end": v(-82.92, -557.1) * mm});
            skLineSegment(sketch, "E932", {"start": v(-82.92, -557.1) * mm, "end": v(-82.3, -558.13) * mm});
            skLineSegment(sketch, "E933", {"start": v(-82.3, -558.13) * mm, "end": v(-81.75, -559.35) * mm});
            skLineSegment(sketch, "E934", {"start": v(-81.75, -559.35) * mm, "end": v(-81.27, -560.76) * mm});
            skLineSegment(sketch, "E935", {"start": v(-81.27, -560.76) * mm, "end": v(-78.74, -569.29) * mm});
            skLineSegment(sketch, "E936", {"start": v(-78.74, -569.29) * mm, "end": v(-78.38, -570.57) * mm});
            skLineSegment(sketch, "E937", {"start": v(-78.38, -570.57) * mm, "end": v(-78.1, -572.03) * mm});
            skLineSegment(sketch, "E938", {"start": v(-78.1, -572.03) * mm, "end": v(-77.89, -573.68) * mm});
            skLineSegment(sketch, "E939", {"start": v(-77.89, -573.68) * mm, "end": v(-77.77, -575.5) * mm});
            skLineSegment(sketch, "E940", {"start": v(-77.77, -575.5) * mm, "end": v(-77.76, -575.78) * mm});
            skLineSegment(sketch, "E941", {"start": v(-77.76, -575.78) * mm, "end": v(-77.7, -577.35) * mm});
            skLineSegment(sketch, "E942", {"start": v(-77.7, -577.35) * mm, "end": v(-77.6, -579.06) * mm});
            skLineSegment(sketch, "E943", {"start": v(-77.6, -579.06) * mm, "end": v(-77.46, -580.9) * mm});
            skLineSegment(sketch, "E944", {"start": v(-77.46, -580.9) * mm, "end": v(-77.29, -582.87) * mm});
            skLineSegment(sketch, "E945", {"start": v(-77.29, -582.87) * mm, "end": v(-77.07, -584.98) * mm});
            skLineSegment(sketch, "E946", {"start": v(-77.07, -584.98) * mm, "end": v(-76.8, -587.21) * mm});
            skLineSegment(sketch, "E947", {"start": v(-76.8, -587.21) * mm, "end": v(-76.48, -589.59) * mm});
            skLineSegment(sketch, "E948", {"start": v(-76.48, -589.59) * mm, "end": v(-76.1, -592.09) * mm});
            skLineSegment(sketch, "E949", {"start": v(-76.1, -592.09) * mm, "end": v(-75.66, -594.72) * mm});
            skLineSegment(sketch, "E950", {"start": v(-75.66, -594.72) * mm, "end": v(-75.16, -597.47) * mm});
            skLineSegment(sketch, "E951", {"start": v(-75.16, -597.47) * mm, "end": v(-74.59, -600.36) * mm});
            skLineSegment(sketch, "E952", {"start": v(-74.59, -600.36) * mm, "end": v(-73.94, -603.37) * mm});
            skLineSegment(sketch, "E953", {"start": v(-73.94, -603.37) * mm, "end": v(-73.22, -606.5) * mm});
            skLineSegment(sketch, "E954", {"start": v(-73.22, -606.5) * mm, "end": v(-72.41, -609.75) * mm});
            skLineSegment(sketch, "E955", {"start": v(-72.41, -609.75) * mm, "end": v(-71.52, -613.12) * mm});
            skLineSegment(sketch, "E956", {"start": v(-71.52, -613.12) * mm, "end": v(-70.54, -616.61) * mm});
            skLineSegment(sketch, "E957", {"start": v(-70.54, -616.61) * mm, "end": v(-69.47, -620.22) * mm});
            skLineSegment(sketch, "E958", {"start": v(-69.47, -620.22) * mm, "end": v(-68.3, -623.94) * mm});
            skLineSegment(sketch, "E959", {"start": v(-68.3, -623.94) * mm, "end": v(-67.03, -627.77) * mm});
            skLineSegment(sketch, "E960", {"start": v(-67.03, -627.77) * mm, "end": v(-65.66, -631.71) * mm});
            skLineSegment(sketch, "E961", {"start": v(-65.66, -631.71) * mm, "end": v(-64.18, -635.76) * mm});
            skLineSegment(sketch, "E962", {"start": v(-64.18, -635.76) * mm, "end": v(-62.59, -639.91) * mm});
            skLineSegment(sketch, "E963", {"start": v(-62.59, -639.91) * mm, "end": v(-60.88, -644.16) * mm});
            skLineSegment(sketch, "E964", {"start": v(-60.88, -644.16) * mm, "end": v(-59.05, -648.52) * mm});
            skLineSegment(sketch, "E965", {"start": v(-59.05, -648.52) * mm, "end": v(-57.1, -652.97) * mm});
            skLineSegment(sketch, "E966", {"start": v(-57.1, -652.97) * mm, "end": v(-55.03, -657.51) * mm});
            skLineSegment(sketch, "E967", {"start": v(-55.03, -657.51) * mm, "end": v(-52.83, -662.15) * mm});
            skLineSegment(sketch, "E968", {"start": v(-52.83, -662.15) * mm, "end": v(-50.5, -666.87) * mm});
            skLineSegment(sketch, "E969", {"start": v(-50.5, -666.87) * mm, "end": v(-48.03, -671.68) * mm});
            skLineSegment(sketch, "E970", {"start": v(-48.03, -671.68) * mm, "end": v(-45.42, -676.57) * mm});
            skLineSegment(sketch, "E971", {"start": v(-45.42, -676.57) * mm, "end": v(-42.67, -681.54) * mm});
            skLineSegment(sketch, "E972", {"start": v(-42.67, -681.54) * mm, "end": v(-39.77, -686.59) * mm});
            skLineSegment(sketch, "E973", {"start": v(-39.77, -686.59) * mm, "end": v(-36.73, -691.7) * mm});
            skLineSegment(sketch, "E974", {"start": v(-36.73, -691.7) * mm, "end": v(-33.54, -696.9) * mm});
            skLineSegment(sketch, "E975", {"start": v(-33.54, -696.9) * mm, "end": v(-30.2, -702.14) * mm});
            skLineSegment(sketch, "E976", {"start": v(-30.2, -702.14) * mm, "end": v(-26.7, -707.46) * mm});
            skLineSegment(sketch, "E977", {"start": v(-26.7, -707.46) * mm, "end": v(-23.03, -712.83) * mm});
            skLineSegment(sketch, "E978", {"start": v(-23.03, -712.83) * mm, "end": v(-19.2, -718.26) * mm});
            skLineSegment(sketch, "E979", {"start": v(-19.2, -718.26) * mm, "end": v(-15.22, -723.74) * mm});
            skArc(sketch, "E980", {"start": v(-15.22, -723.74) * mm, "mid": v(0, -723.9) * mm, "end": v(15.22, -723.74) * mm});
            skLineSegment(sketch, "E981", {"start": v(-112.27, -540.92) * mm, "end": v(-113.27, -540.85) * mm});
            skLineSegment(sketch, "E982", {"start": v(-113.27, -540.85) * mm, "end": v(-123.98, -540.94) * mm});
            skLineSegment(sketch, "E983", {"start": v(-123.98, -540.94) * mm, "end": v(-124.98, -541.07) * mm});
            skLineSegment(sketch, "E984", {"start": v(-124.98, -541.07) * mm, "end": v(-126, -541.4) * mm});
            skLineSegment(sketch, "E985", {"start": v(-126, -541.4) * mm, "end": v(-135.64, -545.92) * mm});
            skLineSegment(sketch, "E986", {"start": v(-135.64, -545.92) * mm, "end": v(-136.59, -546.43) * mm});
            skLineSegment(sketch, "E987", {"start": v(-136.59, -546.43) * mm, "end": v(-137.55, -547.15) * mm});
            skLineSegment(sketch, "E988", {"start": v(-137.55, -547.15) * mm, "end": v(-138.53, -548.06) * mm});
            skLineSegment(sketch, "E989", {"start": v(-138.53, -548.06) * mm, "end": v(-139.5, -549.18) * mm});
            skLineSegment(sketch, "E990", {"start": v(-139.5, -549.18) * mm, "end": v(-145.11, -556.09) * mm});
            skLineSegment(sketch, "E991", {"start": v(-145.11, -556.09) * mm, "end": v(-145.93, -557.13) * mm});
            skLineSegment(sketch, "E992", {"start": v(-145.93, -557.13) * mm, "end": v(-146.76, -558.38) * mm});
            skLineSegment(sketch, "E993", {"start": v(-146.76, -558.38) * mm, "end": v(-147.58, -559.82) * mm});
            skLineSegment(sketch, "E994", {"start": v(-147.58, -559.82) * mm, "end": v(-148.4, -561.46) * mm});
            skLineSegment(sketch, "E995", {"start": v(-148.4, -561.46) * mm, "end": v(-148.5, -561.7) * mm});
            skLineSegment(sketch, "E996", {"start": v(-148.5, -561.7) * mm, "end": v(-149.17, -563.13) * mm});
            skLineSegment(sketch, "E997", {"start": v(-149.17, -563.13) * mm, "end": v(-149.9, -564.67) * mm});
            skLineSegment(sketch, "E998", {"start": v(-149.9, -564.67) * mm, "end": v(-150.74, -566.32) * mm});
            skLineSegment(sketch, "E999", {"start": v(-150.74, -566.32) * mm, "end": v(-151.65, -568.08) * mm});
            skLineSegment(sketch, "E1000", {"start": v(-151.65, -568.08) * mm, "end": v(-152.66, -569.94) * mm});
            skLineSegment(sketch, "E1001", {"start": v(-152.66, -569.94) * mm, "end": v(-153.76, -571.9) * mm});
            skLineSegment(sketch, "E1002", {"start": v(-153.76, -571.9) * mm, "end": v(-154.97, -573.97) * mm});
            skLineSegment(sketch, "E1003", {"start": v(-154.97, -573.97) * mm, "end": v(-156.27, -576.14) * mm});
            skLineSegment(sketch, "E1004", {"start": v(-156.27, -576.14) * mm, "end": v(-157.68, -578.4) * mm});
            skLineSegment(sketch, "E1005", {"start": v(-157.68, -578.4) * mm, "end": v(-159.2, -580.76) * mm});
            skLineSegment(sketch, "E1006", {"start": v(-159.2, -580.76) * mm, "end": v(-160.84, -583.2) * mm});
            skLineSegment(sketch, "E1007", {"start": v(-160.84, -583.2) * mm, "end": v(-162.59, -585.73) * mm});
            skLineSegment(sketch, "E1008", {"start": v(-162.59, -585.73) * mm, "end": v(-164.45, -588.35) * mm});
            skLineSegment(sketch, "E1009", {"start": v(-164.45, -588.35) * mm, "end": v(-166.44, -591.05) * mm});
            skLineSegment(sketch, "E1010", {"start": v(-166.44, -591.05) * mm, "end": v(-168.55, -593.82) * mm});
            skLineSegment(sketch, "E1011", {"start": v(-168.55, -593.82) * mm, "end": v(-170.8, -596.67) * mm});
            skLineSegment(sketch, "E1012", {"start": v(-170.8, -596.67) * mm, "end": v(-173.16, -599.6) * mm});
            skLineSegment(sketch, "E1013", {"start": v(-173.16, -599.6) * mm, "end": v(-175.67, -602.58) * mm});
            skLineSegment(sketch, "E1014", {"start": v(-175.67, -602.58) * mm, "end": v(-178.3, -605.64) * mm});
            skLineSegment(sketch, "E1015", {"start": v(-178.3, -605.64) * mm, "end": v(-181.08, -608.75) * mm});
            skLineSegment(sketch, "E1016", {"start": v(-181.08, -608.75) * mm, "end": v(-184, -611.92) * mm});
            skLineSegment(sketch, "E1017", {"start": v(-184, -611.92) * mm, "end": v(-187.06, -615.15) * mm});
            skLineSegment(sketch, "E1018", {"start": v(-187.06, -615.15) * mm, "end": v(-190.26, -618.43) * mm});
            skLineSegment(sketch, "E1019", {"start": v(-190.26, -618.43) * mm, "end": v(-193.62, -621.75) * mm});
            skLineSegment(sketch, "E1020", {"start": v(-193.62, -621.75) * mm, "end": v(-197.12, -625.12) * mm});
            skLineSegment(sketch, "E1021", {"start": v(-197.12, -625.12) * mm, "end": v(-200.77, -628.52) * mm});
            skLineSegment(sketch, "E1022", {"start": v(-200.77, -628.52) * mm, "end": v(-204.58, -631.96) * mm});
            skLineSegment(sketch, "E1023", {"start": v(-204.58, -631.96) * mm, "end": v(-208.55, -635.43) * mm});
            skLineSegment(sketch, "E1024", {"start": v(-208.55, -635.43) * mm, "end": v(-212.67, -638.93) * mm});
            skLineSegment(sketch, "E1025", {"start": v(-212.67, -638.93) * mm, "end": v(-216.95, -642.45) * mm});
            skLineSegment(sketch, "E1026", {"start": v(-216.95, -642.45) * mm, "end": v(-221.4, -646) * mm});
            skLineSegment(sketch, "E1027", {"start": v(-221.4, -646) * mm, "end": v(-226, -649.54) * mm});
            skLineSegment(sketch, "E1028", {"start": v(-226, -649.54) * mm, "end": v(-230.77, -653.1) * mm});
            skLineSegment(sketch, "E1029", {"start": v(-230.77, -653.1) * mm, "end": v(-235.7, -656.68) * mm});
            skLineSegment(sketch, "E1030", {"start": v(-235.7, -656.68) * mm, "end": v(-240.8, -660.25) * mm});
            skLineSegment(sketch, "E1031", {"start": v(-240.8, -660.25) * mm, "end": v(-246.07, -663.82) * mm});
            skLineSegment(sketch, "E1032", {"start": v(-246.07, -663.82) * mm, "end": v(-251.51, -667.38) * mm});
            skLineSegment(sketch, "E1033", {"start": v(-251.51, -667.38) * mm, "end": v(-257.12, -670.93) * mm});
            skLineSegment(sketch, "E1034", {"start": v(-257.12, -670.93) * mm, "end": v(-262.9, -674.47) * mm});
            skLineSegment(sketch, "E1035", {"start": v(-303.1, -461.87) * mm, "end": v(-302.34, -462.53) * mm});
            skLineSegment(sketch, "E1036", {"start": v(-302.34, -462.53) * mm, "end": v(-294.84, -470.17) * mm});
            skLineSegment(sketch, "E1037", {"start": v(-294.84, -470.17) * mm, "end": v(-294.22, -470.97) * mm});
            skLineSegment(sketch, "E1038", {"start": v(-294.22, -470.97) * mm, "end": v(-293.73, -471.93) * mm});
            skLineSegment(sketch, "E1039", {"start": v(-293.73, -471.93) * mm, "end": v(-290.1, -481.93) * mm});
            skLineSegment(sketch, "E1040", {"start": v(-290.1, -481.93) * mm, "end": v(-289.8, -482.97) * mm});
            skLineSegment(sketch, "E1041", {"start": v(-289.8, -482.97) * mm, "end": v(-289.63, -484.15) * mm});
            skLineSegment(sketch, "E1042", {"start": v(-289.63, -484.15) * mm, "end": v(-289.59, -485.49) * mm});
            skLineSegment(sketch, "E1043", {"start": v(-289.59, -485.49) * mm, "end": v(-289.68, -486.97) * mm});
            skLineSegment(sketch, "E1044", {"start": v(-289.68, -486.97) * mm, "end": v(-290.6, -495.82) * mm});
            skLineSegment(sketch, "E1045", {"start": v(-290.6, -495.82) * mm, "end": v(-290.76, -497.14) * mm});
            skLineSegment(sketch, "E1046", {"start": v(-290.76, -497.14) * mm, "end": v(-291.06, -498.6) * mm});
            skLineSegment(sketch, "E1047", {"start": v(-291.06, -498.6) * mm, "end": v(-291.5, -500.2) * mm});
            skLineSegment(sketch, "E1048", {"start": v(-291.5, -500.2) * mm, "end": v(-292.08, -501.94) * mm});
            skLineSegment(sketch, "E1049", {"start": v(-292.08, -501.94) * mm, "end": v(-292.18, -502.2) * mm});
            skLineSegment(sketch, "E1050", {"start": v(-292.18, -502.2) * mm, "end": v(-292.72, -503.67) * mm});
            skLineSegment(sketch, "E1051", {"start": v(-292.72, -503.67) * mm, "end": v(-293.28, -505.28) * mm});
            skLineSegment(sketch, "E1052", {"start": v(-293.28, -505.28) * mm, "end": v(-293.86, -507.03) * mm});
            skLineSegment(sketch, "E1053", {"start": v(-293.86, -507.03) * mm, "end": v(-294.46, -508.92) * mm});
            skLineSegment(sketch, "E1054", {"start": v(-294.46, -508.92) * mm, "end": v(-295.06, -510.95) * mm});
            skLineSegment(sketch, "E1055", {"start": v(-295.06, -510.95) * mm, "end": v(-295.67, -513.13) * mm});
            skLineSegment(sketch, "E1056", {"start": v(-295.67, -513.13) * mm, "end": v(-296.28, -515.44) * mm});
            skLineSegment(sketch, "E1057", {"start": v(-296.28, -515.44) * mm, "end": v(-296.9, -517.9) * mm});
            skLineSegment(sketch, "E1058", {"start": v(-296.9, -517.9) * mm, "end": v(-297.5, -520.5) * mm});
            skLineSegment(sketch, "E1059", {"start": v(-297.5, -520.5) * mm, "end": v(-298.08, -523.23) * mm});
            skLineSegment(sketch, "E1060", {"start": v(-298.08, -523.23) * mm, "end": v(-298.66, -526.11) * mm});
            skLineSegment(sketch, "E1061", {"start": v(-298.66, -526.11) * mm, "end": v(-299.21, -529.14) * mm});
            skLineSegment(sketch, "E1062", {"start": v(-299.21, -529.14) * mm, "end": v(-299.74, -532.31) * mm});
            skLineSegment(sketch, "E1063", {"start": v(-299.74, -532.31) * mm, "end": v(-300.24, -535.62) * mm});
            skLineSegment(sketch, "E1064", {"start": v(-300.24, -535.62) * mm, "end": v(-300.71, -539.08) * mm});
            skLineSegment(sketch, "E1065", {"start": v(-300.71, -539.08) * mm, "end": v(-301.14, -542.68) * mm});
            skLineSegment(sketch, "E1066", {"start": v(-301.14, -542.68) * mm, "end": v(-301.53, -546.42) * mm});
            skLineSegment(sketch, "E1067", {"start": v(-301.53, -546.42) * mm, "end": v(-301.88, -550.3) * mm});
            skLineSegment(sketch, "E1068", {"start": v(-301.88, -550.3) * mm, "end": v(-302.17, -554.33) * mm});
            skLineSegment(sketch, "E1069", {"start": v(-302.17, -554.33) * mm, "end": v(-302.4, -558.5) * mm});
            skLineSegment(sketch, "E1070", {"start": v(-302.4, -558.5) * mm, "end": v(-302.59, -562.8) * mm});
            skLineSegment(sketch, "E1071", {"start": v(-302.59, -562.8) * mm, "end": v(-302.7, -567.25) * mm});
            skLineSegment(sketch, "E1072", {"start": v(-302.7, -567.25) * mm, "end": v(-302.76, -571.83) * mm});
            skLineSegment(sketch, "E1073", {"start": v(-302.76, -571.83) * mm, "end": v(-302.74, -576.55) * mm});
            skLineSegment(sketch, "E1074", {"start": v(-302.74, -576.55) * mm, "end": v(-302.64, -581.41) * mm});
            skLineSegment(sketch, "E1075", {"start": v(-302.64, -581.41) * mm, "end": v(-302.46, -586.4) * mm});
            skLineSegment(sketch, "E1076", {"start": v(-302.46, -586.4) * mm, "end": v(-302.2, -591.53) * mm});
            skLineSegment(sketch, "E1077", {"start": v(-302.2, -591.53) * mm, "end": v(-301.85, -596.78) * mm});
            skLineSegment(sketch, "E1078", {"start": v(-301.85, -596.78) * mm, "end": v(-301.41, -602.17) * mm});
            skLineSegment(sketch, "E1079", {"start": v(-301.41, -602.17) * mm, "end": v(-300.87, -607.69) * mm});
            skLineSegment(sketch, "E1080", {"start": v(-300.87, -607.69) * mm, "end": v(-300.24, -613.33) * mm});
            skLineSegment(sketch, "E1081", {"start": v(-300.24, -613.33) * mm, "end": v(-299.5, -619.1) * mm});
            skLineSegment(sketch, "E1082", {"start": v(-299.5, -619.1) * mm, "end": v(-298.64, -625) * mm});
            skLineSegment(sketch, "E1083", {"start": v(-298.64, -625) * mm, "end": v(-297.67, -631) * mm});
            skLineSegment(sketch, "E1084", {"start": v(-297.67, -631) * mm, "end": v(-296.6, -637.14) * mm});
            skLineSegment(sketch, "E1085", {"start": v(-296.6, -637.14) * mm, "end": v(-295.4, -643.4) * mm});
            skLineSegment(sketch, "E1086", {"start": v(-295.4, -643.4) * mm, "end": v(-294.06, -649.76) * mm});
            skLineSegment(sketch, "E1087", {"start": v(-294.06, -649.76) * mm, "end": v(-292.6, -656.23) * mm});
            skLineSegment(sketch, "E1088", {"start": v(-292.6, -656.23) * mm, "end": v(-291.02, -662.82) * mm});
            skArc(sketch, "E1089", {"start": v(-291.02, -662.82) * mm, "mid": v(-277.02, -668.8) * mm, "end": v(-262.9, -674.47) * mm});
            skLineSegment(sketch, "E1090", {"start": v(-310.72, -456.78) * mm, "end": v(-311.62, -456.33) * mm});
            skLineSegment(sketch, "E1091", {"start": v(-311.62, -456.33) * mm, "end": v(-321.55, -452.32) * mm});
            skLineSegment(sketch, "E1092", {"start": v(-321.55, -452.32) * mm, "end": v(-322.53, -452.06) * mm});
            skLineSegment(sketch, "E1093", {"start": v(-322.53, -452.06) * mm, "end": v(-323.6, -451.97) * mm});
            skLineSegment(sketch, "E1094", {"start": v(-323.6, -451.97) * mm, "end": v(-334.23, -452.45) * mm});
            skLineSegment(sketch, "E1095", {"start": v(-334.23, -452.45) * mm, "end": v(-335.3, -452.57) * mm});
            skLineSegment(sketch, "E1096", {"start": v(-335.3, -452.57) * mm, "end": v(-336.46, -452.86) * mm});
            skLineSegment(sketch, "E1097", {"start": v(-336.46, -452.86) * mm, "end": v(-337.71, -453.33) * mm});
            skLineSegment(sketch, "E1098", {"start": v(-337.71, -453.33) * mm, "end": v(-339.05, -453.99) * mm});
            skLineSegment(sketch, "E1099", {"start": v(-339.05, -453.99) * mm, "end": v(-346.87, -458.22) * mm});
            skLineSegment(sketch, "E1100", {"start": v(-346.87, -458.22) * mm, "end": v(-348.03, -458.88) * mm});
            skLineSegment(sketch, "E1101", {"start": v(-348.03, -458.88) * mm, "end": v(-349.27, -459.71) * mm});
            skLineSegment(sketch, "E1102", {"start": v(-349.27, -459.71) * mm, "end": v(-350.58, -460.73) * mm});
            skLineSegment(sketch, "E1103", {"start": v(-350.58, -460.73) * mm, "end": v(-351.96, -461.94) * mm});
            skLineSegment(sketch, "E1104", {"start": v(-351.96, -461.94) * mm, "end": v(-352.16, -462.12) * mm});
            skLineSegment(sketch, "E1105", {"start": v(-352.16, -462.12) * mm, "end": v(-353.31, -463.18) * mm});
            skLineSegment(sketch, "E1106", {"start": v(-353.31, -463.18) * mm, "end": v(-354.59, -464.32) * mm});
            skLineSegment(sketch, "E1107", {"start": v(-354.59, -464.32) * mm, "end": v(-355.98, -465.53) * mm});
            skLineSegment(sketch, "E1108", {"start": v(-355.98, -465.53) * mm, "end": v(-357.5, -466.8) * mm});
            skLineSegment(sketch, "E1109", {"start": v(-357.5, -466.8) * mm, "end": v(-359.15, -468.13) * mm});
            skLineSegment(sketch, "E1110", {"start": v(-359.15, -468.13) * mm, "end": v(-360.92, -469.53) * mm});
            skLineSegment(sketch, "E1111", {"start": v(-360.92, -469.53) * mm, "end": v(-362.82, -470.98) * mm});
            skLineSegment(sketch, "E1112", {"start": v(-362.82, -470.98) * mm, "end": v(-364.86, -472.48) * mm});
            skLineSegment(sketch, "E1113", {"start": v(-364.86, -472.48) * mm, "end": v(-367.03, -474.03) * mm});
            skLineSegment(sketch, "E1114", {"start": v(-367.03, -474.03) * mm, "end": v(-369.33, -475.62) * mm});
            skLineSegment(sketch, "E1115", {"start": v(-369.33, -475.62) * mm, "end": v(-371.78, -477.26) * mm});
            skLineSegment(sketch, "E1116", {"start": v(-371.78, -477.26) * mm, "end": v(-374.36, -478.93) * mm});
            skLineSegment(sketch, "E1117", {"start": v(-374.36, -478.93) * mm, "end": v(-377.09, -480.63) * mm});
            skLineSegment(sketch, "E1118", {"start": v(-377.09, -480.63) * mm, "end": v(-379.95, -482.36) * mm});
            skLineSegment(sketch, "E1119", {"start": v(-379.95, -482.36) * mm, "end": v(-382.97, -484.12) * mm});
            skLineSegment(sketch, "E1120", {"start": v(-382.97, -484.12) * mm, "end": v(-386.13, -485.9) * mm});
            skLineSegment(sketch, "E1121", {"start": v(-386.13, -485.9) * mm, "end": v(-389.44, -487.69) * mm});
            skLineSegment(sketch, "E1122", {"start": v(-389.44, -487.69) * mm, "end": v(-392.9, -489.49) * mm});
            skLineSegment(sketch, "E1123", {"start": v(-392.9, -489.49) * mm, "end": v(-396.5, -491.3) * mm});
            skLineSegment(sketch, "E1124", {"start": v(-396.5, -491.3) * mm, "end": v(-400.26, -493.12) * mm});
            skLineSegment(sketch, "E1125", {"start": v(-400.26, -493.12) * mm, "end": v(-404.17, -494.93) * mm});
            skLineSegment(sketch, "E1126", {"start": v(-404.17, -494.93) * mm, "end": v(-408.23, -496.74) * mm});
            skLineSegment(sketch, "E1127", {"start": v(-408.23, -496.74) * mm, "end": v(-412.44, -498.54) * mm});
            skLineSegment(sketch, "E1128", {"start": v(-412.44, -498.54) * mm, "end": v(-416.81, -500.33) * mm});
            skLineSegment(sketch, "E1129", {"start": v(-416.81, -500.33) * mm, "end": v(-421.34, -502.1) * mm});
            skLineSegment(sketch, "E1130", {"start": v(-421.34, -502.1) * mm, "end": v(-426.02, -503.85) * mm});
            skLineSegment(sketch, "E1131", {"start": v(-426.02, -503.85) * mm, "end": v(-430.85, -505.57) * mm});
            skLineSegment(sketch, "E1132", {"start": v(-430.85, -505.57) * mm, "end": v(-435.84, -507.26) * mm});
            skLineSegment(sketch, "E1133", {"start": v(-435.84, -507.26) * mm, "end": v(-440.99, -508.9) * mm});
            skLineSegment(sketch, "E1134", {"start": v(-440.99, -508.9) * mm, "end": v(-446.3, -510.52) * mm});
            skLineSegment(sketch, "E1135", {"start": v(-446.3, -510.52) * mm, "end": v(-451.75, -512.1) * mm});
            skLineSegment(sketch, "E1136", {"start": v(-451.75, -512.1) * mm, "end": v(-457.37, -513.61) * mm});
            skLineSegment(sketch, "E1137", {"start": v(-457.37, -513.61) * mm, "end": v(-463.14, -515.08) * mm});
            skLineSegment(sketch, "E1138", {"start": v(-463.14, -515.08) * mm, "end": v(-469.06, -516.5) * mm});
            skLineSegment(sketch, "E1139", {"start": v(-469.06, -516.5) * mm, "end": v(-475.14, -517.84) * mm});
            skLineSegment(sketch, "E1140", {"start": v(-475.14, -517.84) * mm, "end": v(-481.38, -519.12) * mm});
            skLineSegment(sketch, "E1141", {"start": v(-481.38, -519.12) * mm, "end": v(-487.76, -520.33) * mm});
            skLineSegment(sketch, "E1142", {"start": v(-487.76, -520.33) * mm, "end": v(-494.3, -521.47) * mm});
            skLineSegment(sketch, "E1143", {"start": v(-494.3, -521.47) * mm, "end": v(-501, -522.52) * mm});
            skLineSegment(sketch, "E1144", {"start": v(-456.78, -310.72) * mm, "end": v(-456.33, -311.62) * mm});
            skLineSegment(sketch, "E1145", {"start": v(-456.33, -311.62) * mm, "end": v(-452.32, -321.55) * mm});
            skLineSegment(sketch, "E1146", {"start": v(-452.32, -321.55) * mm, "end": v(-452.06, -322.53) * mm});
            skLineSegment(sketch, "E1147", {"start": v(-452.06, -322.53) * mm, "end": v(-451.97, -323.6) * mm});
            skLineSegment(sketch, "E1148", {"start": v(-451.97, -323.6) * mm, "end": v(-452.45, -334.23) * mm});
            skLineSegment(sketch, "E1149", {"start": v(-452.45, -334.23) * mm, "end": v(-452.57, -335.3) * mm});
            skLineSegment(sketch, "E1150", {"start": v(-452.57, -335.3) * mm, "end": v(-452.86, -336.46) * mm});
            skLineSegment(sketch, "E1151", {"start": v(-452.86, -336.46) * mm, "end": v(-453.33, -337.71) * mm});
            skLineSegment(sketch, "E1152", {"start": v(-453.33, -337.71) * mm, "end": v(-453.99, -339.05) * mm});
            skLineSegment(sketch, "E1153", {"start": v(-453.99, -339.05) * mm, "end": v(-458.22, -346.87) * mm});
            skLineSegment(sketch, "E1154", {"start": v(-458.22, -346.87) * mm, "end": v(-458.88, -348.03) * mm});
            skLineSegment(sketch, "E1155", {"start": v(-458.88, -348.03) * mm, "end": v(-459.71, -349.27) * mm});
            skLineSegment(sketch, "E1156", {"start": v(-459.71, -349.27) * mm, "end": v(-460.73, -350.58) * mm});
            skLineSegment(sketch, "E1157", {"start": v(-460.73, -350.58) * mm, "end": v(-461.94, -351.96) * mm});
            skLineSegment(sketch, "E1158", {"start": v(-461.94, -351.96) * mm, "end": v(-462.12, -352.16) * mm});
            skLineSegment(sketch, "E1159", {"start": v(-462.12, -352.16) * mm, "end": v(-463.18, -353.31) * mm});
            skLineSegment(sketch, "E1160", {"start": v(-463.18, -353.31) * mm, "end": v(-464.32, -354.59) * mm});
            skLineSegment(sketch, "E1161", {"start": v(-464.32, -354.59) * mm, "end": v(-465.53, -355.98) * mm});
            skLineSegment(sketch, "E1162", {"start": v(-465.53, -355.98) * mm, "end": v(-466.8, -357.5) * mm});
            skLineSegment(sketch, "E1163", {"start": v(-466.8, -357.5) * mm, "end": v(-468.13, -359.15) * mm});
            skLineSegment(sketch, "E1164", {"start": v(-468.13, -359.15) * mm, "end": v(-469.53, -360.92) * mm});
            skLineSegment(sketch, "E1165", {"start": v(-469.53, -360.92) * mm, "end": v(-470.98, -362.82) * mm});
            skLineSegment(sketch, "E1166", {"start": v(-470.98, -362.82) * mm, "end": v(-472.48, -364.86) * mm});
            skLineSegment(sketch, "E1167", {"start": v(-472.48, -364.86) * mm, "end": v(-474.03, -367.03) * mm});
            skLineSegment(sketch, "E1168", {"start": v(-474.03, -367.03) * mm, "end": v(-475.62, -369.33) * mm});
            skLineSegment(sketch, "E1169", {"start": v(-475.62, -369.33) * mm, "end": v(-477.26, -371.78) * mm});
            skLineSegment(sketch, "E1170", {"start": v(-477.26, -371.78) * mm, "end": v(-478.93, -374.36) * mm});
            skLineSegment(sketch, "E1171", {"start": v(-478.93, -374.36) * mm, "end": v(-480.63, -377.09) * mm});
            skLineSegment(sketch, "E1172", {"start": v(-480.63, -377.09) * mm, "end": v(-482.36, -379.95) * mm});
            skLineSegment(sketch, "E1173", {"start": v(-482.36, -379.95) * mm, "end": v(-484.12, -382.97) * mm});
            skLineSegment(sketch, "E1174", {"start": v(-484.12, -382.97) * mm, "end": v(-485.9, -386.13) * mm});
            skLineSegment(sketch, "E1175", {"start": v(-485.9, -386.13) * mm, "end": v(-487.69, -389.44) * mm});
            skLineSegment(sketch, "E1176", {"start": v(-487.69, -389.44) * mm, "end": v(-489.49, -392.9) * mm});
            skLineSegment(sketch, "E1177", {"start": v(-489.49, -392.9) * mm, "end": v(-491.3, -396.5) * mm});
            skLineSegment(sketch, "E1178", {"start": v(-491.3, -396.5) * mm, "end": v(-493.12, -400.26) * mm});
            skLineSegment(sketch, "E1179", {"start": v(-493.12, -400.26) * mm, "end": v(-494.93, -404.17) * mm});
            skLineSegment(sketch, "E1180", {"start": v(-494.93, -404.17) * mm, "end": v(-496.74, -408.23) * mm});
            skLineSegment(sketch, "E1181", {"start": v(-496.74, -408.23) * mm, "end": v(-498.54, -412.44) * mm});
            skLineSegment(sketch, "E1182", {"start": v(-498.54, -412.44) * mm, "end": v(-500.33, -416.81) * mm});
            skLineSegment(sketch, "E1183", {"start": v(-500.33, -416.81) * mm, "end": v(-502.1, -421.34) * mm});
            skLineSegment(sketch, "E1184", {"start": v(-502.1, -421.34) * mm, "end": v(-503.85, -426.02) * mm});
            skLineSegment(sketch, "E1185", {"start": v(-503.85, -426.02) * mm, "end": v(-505.57, -430.85) * mm});
            skLineSegment(sketch, "E1186", {"start": v(-505.57, -430.85) * mm, "end": v(-507.26, -435.84) * mm});
            skLineSegment(sketch, "E1187", {"start": v(-507.26, -435.84) * mm, "end": v(-508.9, -440.99) * mm});
            skLineSegment(sketch, "E1188", {"start": v(-508.9, -440.99) * mm, "end": v(-510.52, -446.3) * mm});
            skLineSegment(sketch, "E1189", {"start": v(-510.52, -446.3) * mm, "end": v(-512.1, -451.75) * mm});
            skLineSegment(sketch, "E1190", {"start": v(-512.1, -451.75) * mm, "end": v(-513.61, -457.37) * mm});
            skLineSegment(sketch, "E1191", {"start": v(-513.61, -457.37) * mm, "end": v(-515.08, -463.14) * mm});
            skLineSegment(sketch, "E1192", {"start": v(-515.08, -463.14) * mm, "end": v(-516.5, -469.06) * mm});
            skLineSegment(sketch, "E1193", {"start": v(-516.5, -469.06) * mm, "end": v(-517.84, -475.14) * mm});
            skLineSegment(sketch, "E1194", {"start": v(-517.84, -475.14) * mm, "end": v(-519.12, -481.38) * mm});
            skLineSegment(sketch, "E1195", {"start": v(-519.12, -481.38) * mm, "end": v(-520.33, -487.76) * mm});
            skLineSegment(sketch, "E1196", {"start": v(-520.33, -487.76) * mm, "end": v(-521.47, -494.3) * mm});
            skLineSegment(sketch, "E1197", {"start": v(-521.47, -494.3) * mm, "end": v(-522.52, -501) * mm});
            skArc(sketch, "E1198", {"start": v(-522.52, -501) * mm, "mid": v(-511.87, -511.87) * mm, "end": v(-501, -522.52) * mm});
            skLineSegment(sketch, "E1199", {"start": v(-461.87, -303.1) * mm, "end": v(-462.53, -302.34) * mm});
            skLineSegment(sketch, "E1200", {"start": v(-462.53, -302.34) * mm, "end": v(-470.17, -294.84) * mm});
            skLineSegment(sketch, "E1201", {"start": v(-470.17, -294.84) * mm, "end": v(-470.97, -294.22) * mm});
            skLineSegment(sketch, "E1202", {"start": v(-470.97, -294.22) * mm, "end": v(-471.93, -293.73) * mm});
            skLineSegment(sketch, "E1203", {"start": v(-471.93, -293.73) * mm, "end": v(-481.93, -290.1) * mm});
            skLineSegment(sketch, "E1204", {"start": v(-481.93, -290.1) * mm, "end": v(-482.97, -289.8) * mm});
            skLineSegment(sketch, "E1205", {"start": v(-482.97, -289.8) * mm, "end": v(-484.15, -289.63) * mm});
            skLineSegment(sketch, "E1206", {"start": v(-484.15, -289.63) * mm, "end": v(-485.49, -289.59) * mm});
            skLineSegment(sketch, "E1207", {"start": v(-485.49, -289.59) * mm, "end": v(-486.97, -289.68) * mm});
            skLineSegment(sketch, "E1208", {"start": v(-486.97, -289.68) * mm, "end": v(-495.82, -290.6) * mm});
            skLineSegment(sketch, "E1209", {"start": v(-495.82, -290.6) * mm, "end": v(-497.14, -290.76) * mm});
            skLineSegment(sketch, "E1210", {"start": v(-497.14, -290.76) * mm, "end": v(-498.6, -291.06) * mm});
            skLineSegment(sketch, "E1211", {"start": v(-498.6, -291.06) * mm, "end": v(-500.2, -291.5) * mm});
            skLineSegment(sketch, "E1212", {"start": v(-500.2, -291.5) * mm, "end": v(-501.94, -292.08) * mm});
            skLineSegment(sketch, "E1213", {"start": v(-501.94, -292.08) * mm, "end": v(-502.2, -292.18) * mm});
            skLineSegment(sketch, "E1214", {"start": v(-502.2, -292.18) * mm, "end": v(-503.67, -292.72) * mm});
            skLineSegment(sketch, "E1215", {"start": v(-503.67, -292.72) * mm, "end": v(-505.28, -293.28) * mm});
            skLineSegment(sketch, "E1216", {"start": v(-505.28, -293.28) * mm, "end": v(-507.03, -293.86) * mm});
            skLineSegment(sketch, "E1217", {"start": v(-507.03, -293.86) * mm, "end": v(-508.92, -294.46) * mm});
            skLineSegment(sketch, "E1218", {"start": v(-508.92, -294.46) * mm, "end": v(-510.95, -295.06) * mm});
            skLineSegment(sketch, "E1219", {"start": v(-510.95, -295.06) * mm, "end": v(-513.13, -295.67) * mm});
            skLineSegment(sketch, "E1220", {"start": v(-513.13, -295.67) * mm, "end": v(-515.44, -296.28) * mm});
            skLineSegment(sketch, "E1221", {"start": v(-515.44, -296.28) * mm, "end": v(-517.9, -296.9) * mm});
            skLineSegment(sketch, "E1222", {"start": v(-517.9, -296.9) * mm, "end": v(-520.5, -297.5) * mm});
            skLineSegment(sketch, "E1223", {"start": v(-520.5, -297.5) * mm, "end": v(-523.23, -298.08) * mm});
            skLineSegment(sketch, "E1224", {"start": v(-523.23, -298.08) * mm, "end": v(-526.11, -298.66) * mm});
            skLineSegment(sketch, "E1225", {"start": v(-526.11, -298.66) * mm, "end": v(-529.14, -299.21) * mm});
            skLineSegment(sketch, "E1226", {"start": v(-529.14, -299.21) * mm, "end": v(-532.31, -299.74) * mm});
            skLineSegment(sketch, "E1227", {"start": v(-532.31, -299.74) * mm, "end": v(-535.62, -300.24) * mm});
            skLineSegment(sketch, "E1228", {"start": v(-535.62, -300.24) * mm, "end": v(-539.08, -300.71) * mm});
            skLineSegment(sketch, "E1229", {"start": v(-539.08, -300.71) * mm, "end": v(-542.68, -301.14) * mm});
            skLineSegment(sketch, "E1230", {"start": v(-542.68, -301.14) * mm, "end": v(-546.42, -301.53) * mm});
            skLineSegment(sketch, "E1231", {"start": v(-546.42, -301.53) * mm, "end": v(-550.3, -301.88) * mm});
            skLineSegment(sketch, "E1232", {"start": v(-550.3, -301.88) * mm, "end": v(-554.33, -302.17) * mm});
            skLineSegment(sketch, "E1233", {"start": v(-554.33, -302.17) * mm, "end": v(-558.5, -302.4) * mm});
            skLineSegment(sketch, "E1234", {"start": v(-558.5, -302.4) * mm, "end": v(-562.8, -302.59) * mm});
            skLineSegment(sketch, "E1235", {"start": v(-562.8, -302.59) * mm, "end": v(-567.25, -302.7) * mm});
            skLineSegment(sketch, "E1236", {"start": v(-567.25, -302.7) * mm, "end": v(-571.83, -302.76) * mm});
            skLineSegment(sketch, "E1237", {"start": v(-571.83, -302.76) * mm, "end": v(-576.55, -302.74) * mm});
            skLineSegment(sketch, "E1238", {"start": v(-576.55, -302.74) * mm, "end": v(-581.41, -302.64) * mm});
            skLineSegment(sketch, "E1239", {"start": v(-581.41, -302.64) * mm, "end": v(-586.4, -302.46) * mm});
            skLineSegment(sketch, "E1240", {"start": v(-586.4, -302.46) * mm, "end": v(-591.53, -302.2) * mm});
            skLineSegment(sketch, "E1241", {"start": v(-591.53, -302.2) * mm, "end": v(-596.78, -301.85) * mm});
            skLineSegment(sketch, "E1242", {"start": v(-596.78, -301.85) * mm, "end": v(-602.17, -301.41) * mm});
            skLineSegment(sketch, "E1243", {"start": v(-602.17, -301.41) * mm, "end": v(-607.69, -300.87) * mm});
            skLineSegment(sketch, "E1244", {"start": v(-607.69, -300.87) * mm, "end": v(-613.33, -300.24) * mm});
            skLineSegment(sketch, "E1245", {"start": v(-613.33, -300.24) * mm, "end": v(-619.1, -299.5) * mm});
            skLineSegment(sketch, "E1246", {"start": v(-619.1, -299.5) * mm, "end": v(-625, -298.64) * mm});
            skLineSegment(sketch, "E1247", {"start": v(-625, -298.64) * mm, "end": v(-631, -297.67) * mm});
            skLineSegment(sketch, "E1248", {"start": v(-631, -297.67) * mm, "end": v(-637.14, -296.6) * mm});
            skLineSegment(sketch, "E1249", {"start": v(-637.14, -296.6) * mm, "end": v(-643.4, -295.4) * mm});
            skLineSegment(sketch, "E1250", {"start": v(-643.4, -295.4) * mm, "end": v(-649.76, -294.06) * mm});
            skLineSegment(sketch, "E1251", {"start": v(-649.76, -294.06) * mm, "end": v(-656.23, -292.6) * mm});
            skLineSegment(sketch, "E1252", {"start": v(-656.23, -292.6) * mm, "end": v(-662.82, -291.02) * mm});
            skLineSegment(sketch, "E1253", {"start": v(-540.92, -112.27) * mm, "end": v(-540.85, -113.27) * mm});
            skLineSegment(sketch, "E1254", {"start": v(-540.85, -113.27) * mm, "end": v(-540.94, -123.98) * mm});
            skLineSegment(sketch, "E1255", {"start": v(-540.94, -123.98) * mm, "end": v(-541.07, -124.98) * mm});
            skLineSegment(sketch, "E1256", {"start": v(-541.07, -124.98) * mm, "end": v(-541.4, -126) * mm});
            skLineSegment(sketch, "E1257", {"start": v(-541.4, -126) * mm, "end": v(-545.92, -135.64) * mm});
            skLineSegment(sketch, "E1258", {"start": v(-545.92, -135.64) * mm, "end": v(-546.43, -136.59) * mm});
            skLineSegment(sketch, "E1259", {"start": v(-546.43, -136.59) * mm, "end": v(-547.15, -137.55) * mm});
            skLineSegment(sketch, "E1260", {"start": v(-547.15, -137.55) * mm, "end": v(-548.06, -138.53) * mm});
            skLineSegment(sketch, "E1261", {"start": v(-548.06, -138.53) * mm, "end": v(-549.18, -139.5) * mm});
            skLineSegment(sketch, "E1262", {"start": v(-549.18, -139.5) * mm, "end": v(-556.09, -145.11) * mm});
            skLineSegment(sketch, "E1263", {"start": v(-556.09, -145.11) * mm, "end": v(-557.13, -145.93) * mm});
            skLineSegment(sketch, "E1264", {"start": v(-557.13, -145.93) * mm, "end": v(-558.38, -146.76) * mm});
            skLineSegment(sketch, "E1265", {"start": v(-558.38, -146.76) * mm, "end": v(-559.82, -147.58) * mm});
            skLineSegment(sketch, "E1266", {"start": v(-559.82, -147.58) * mm, "end": v(-561.46, -148.4) * mm});
            skLineSegment(sketch, "E1267", {"start": v(-561.46, -148.4) * mm, "end": v(-561.7, -148.5) * mm});
            skLineSegment(sketch, "E1268", {"start": v(-561.7, -148.5) * mm, "end": v(-563.13, -149.17) * mm});
            skLineSegment(sketch, "E1269", {"start": v(-563.13, -149.17) * mm, "end": v(-564.67, -149.9) * mm});
            skLineSegment(sketch, "E1270", {"start": v(-564.67, -149.9) * mm, "end": v(-566.32, -150.74) * mm});
            skLineSegment(sketch, "E1271", {"start": v(-566.32, -150.74) * mm, "end": v(-568.08, -151.65) * mm});
            skLineSegment(sketch, "E1272", {"start": v(-568.08, -151.65) * mm, "end": v(-569.94, -152.66) * mm});
            skLineSegment(sketch, "E1273", {"start": v(-569.94, -152.66) * mm, "end": v(-571.9, -153.76) * mm});
            skLineSegment(sketch, "E1274", {"start": v(-571.9, -153.76) * mm, "end": v(-573.97, -154.97) * mm});
            skLineSegment(sketch, "E1275", {"start": v(-573.97, -154.97) * mm, "end": v(-576.14, -156.27) * mm});
            skLineSegment(sketch, "E1276", {"start": v(-576.14, -156.27) * mm, "end": v(-578.4, -157.68) * mm});
            skLineSegment(sketch, "E1277", {"start": v(-578.4, -157.68) * mm, "end": v(-580.76, -159.2) * mm});
            skLineSegment(sketch, "E1278", {"start": v(-580.76, -159.2) * mm, "end": v(-583.2, -160.84) * mm});
            skLineSegment(sketch, "E1279", {"start": v(-583.2, -160.84) * mm, "end": v(-585.73, -162.59) * mm});
            skLineSegment(sketch, "E1280", {"start": v(-585.73, -162.59) * mm, "end": v(-588.35, -164.45) * mm});
            skLineSegment(sketch, "E1281", {"start": v(-588.35, -164.45) * mm, "end": v(-591.05, -166.44) * mm});
            skLineSegment(sketch, "E1282", {"start": v(-591.05, -166.44) * mm, "end": v(-593.82, -168.55) * mm});
            skLineSegment(sketch, "E1283", {"start": v(-593.82, -168.55) * mm, "end": v(-596.67, -170.8) * mm});
            skLineSegment(sketch, "E1284", {"start": v(-596.67, -170.8) * mm, "end": v(-599.6, -173.16) * mm});
            skLineSegment(sketch, "E1285", {"start": v(-599.6, -173.16) * mm, "end": v(-602.58, -175.67) * mm});
            skLineSegment(sketch, "E1286", {"start": v(-602.58, -175.67) * mm, "end": v(-605.64, -178.3) * mm});
            skLineSegment(sketch, "E1287", {"start": v(-605.64, -178.3) * mm, "end": v(-608.75, -181.08) * mm});
            skLineSegment(sketch, "E1288", {"start": v(-608.75, -181.08) * mm, "end": v(-611.92, -184) * mm});
            skLineSegment(sketch, "E1289", {"start": v(-611.92, -184) * mm, "end": v(-615.15, -187.06) * mm});
            skLineSegment(sketch, "E1290", {"start": v(-615.15, -187.06) * mm, "end": v(-618.43, -190.26) * mm});
            skLineSegment(sketch, "E1291", {"start": v(-618.43, -190.26) * mm, "end": v(-621.75, -193.62) * mm});
            skLineSegment(sketch, "E1292", {"start": v(-621.75, -193.62) * mm, "end": v(-625.12, -197.12) * mm});
            skLineSegment(sketch, "E1293", {"start": v(-625.12, -197.12) * mm, "end": v(-628.52, -200.77) * mm});
            skLineSegment(sketch, "E1294", {"start": v(-628.52, -200.77) * mm, "end": v(-631.96, -204.58) * mm});
            skLineSegment(sketch, "E1295", {"start": v(-631.96, -204.58) * mm, "end": v(-635.43, -208.55) * mm});
            skLineSegment(sketch, "E1296", {"start": v(-635.43, -208.55) * mm, "end": v(-638.93, -212.67) * mm});
            skLineSegment(sketch, "E1297", {"start": v(-638.93, -212.67) * mm, "end": v(-642.45, -216.95) * mm});
            skLineSegment(sketch, "E1298", {"start": v(-642.45, -216.95) * mm, "end": v(-646, -221.4) * mm});
            skLineSegment(sketch, "E1299", {"start": v(-646, -221.4) * mm, "end": v(-649.54, -226) * mm});
            skLineSegment(sketch, "E1300", {"start": v(-649.54, -226) * mm, "end": v(-653.1, -230.77) * mm});
            skLineSegment(sketch, "E1301", {"start": v(-653.1, -230.77) * mm, "end": v(-656.68, -235.7) * mm});
            skLineSegment(sketch, "E1302", {"start": v(-656.68, -235.7) * mm, "end": v(-660.25, -240.8) * mm});
            skLineSegment(sketch, "E1303", {"start": v(-660.25, -240.8) * mm, "end": v(-663.82, -246.07) * mm});
            skLineSegment(sketch, "E1304", {"start": v(-663.82, -246.07) * mm, "end": v(-667.38, -251.51) * mm});
            skLineSegment(sketch, "E1305", {"start": v(-667.38, -251.51) * mm, "end": v(-670.93, -257.12) * mm});
            skLineSegment(sketch, "E1306", {"start": v(-670.93, -257.12) * mm, "end": v(-674.47, -262.9) * mm});
            skArc(sketch, "E1307", {"start": v(-674.47, -262.9) * mm, "mid": v(-668.8, -277.02) * mm, "end": v(-662.82, -291.02) * mm});
            skLineSegment(sketch, "E1308", {"start": v(-542.7, -103.28) * mm, "end": v(-543.03, -102.33) * mm});
            skLineSegment(sketch, "E1309", {"start": v(-543.03, -102.33) * mm, "end": v(-547.21, -92.47) * mm});
            skLineSegment(sketch, "E1310", {"start": v(-547.21, -92.47) * mm, "end": v(-547.71, -91.6) * mm});
            skLineSegment(sketch, "E1311", {"start": v(-547.71, -91.6) * mm, "end": v(-548.41, -90.77) * mm});
            skLineSegment(sketch, "E1312", {"start": v(-548.41, -90.77) * mm, "end": v(-556.27, -83.6) * mm});
            skLineSegment(sketch, "E1313", {"start": v(-556.27, -83.6) * mm, "end": v(-557.1, -82.92) * mm});
            skLineSegment(sketch, "E1314", {"start": v(-557.1, -82.92) * mm, "end": v(-558.13, -82.3) * mm});
            skLineSegment(sketch, "E1315", {"start": v(-558.13, -82.3) * mm, "end": v(-559.35, -81.75) * mm});
            skLineSegment(sketch, "E1316", {"start": v(-559.35, -81.75) * mm, "end": v(-560.76, -81.27) * mm});
            skLineSegment(sketch, "E1317", {"start": v(-560.76, -81.27) * mm, "end": v(-569.29, -78.74) * mm});
            skLineSegment(sketch, "E1318", {"start": v(-569.29, -78.74) * mm, "end": v(-570.57, -78.38) * mm});
            skLineSegment(sketch, "E1319", {"start": v(-570.57, -78.38) * mm, "end": v(-572.03, -78.1) * mm});
            skLineSegment(sketch, "E1320", {"start": v(-572.03, -78.1) * mm, "end": v(-573.68, -77.89) * mm});
            skLineSegment(sketch, "E1321", {"start": v(-573.68, -77.89) * mm, "end": v(-575.5, -77.77) * mm});
            skLineSegment(sketch, "E1322", {"start": v(-575.5, -77.77) * mm, "end": v(-575.78, -77.76) * mm});
            skLineSegment(sketch, "E1323", {"start": v(-575.78, -77.76) * mm, "end": v(-577.35, -77.7) * mm});
            skLineSegment(sketch, "E1324", {"start": v(-577.35, -77.7) * mm, "end": v(-579.06, -77.6) * mm});
            skLineSegment(sketch, "E1325", {"start": v(-579.06, -77.6) * mm, "end": v(-580.9, -77.46) * mm});
            skLineSegment(sketch, "E1326", {"start": v(-580.9, -77.46) * mm, "end": v(-582.87, -77.29) * mm});
            skLineSegment(sketch, "E1327", {"start": v(-582.87, -77.29) * mm, "end": v(-584.98, -77.07) * mm});
            skLineSegment(sketch, "E1328", {"start": v(-584.98, -77.07) * mm, "end": v(-587.21, -76.8) * mm});
            skLineSegment(sketch, "E1329", {"start": v(-587.21, -76.8) * mm, "end": v(-589.59, -76.48) * mm});
            skLineSegment(sketch, "E1330", {"start": v(-589.59, -76.48) * mm, "end": v(-592.09, -76.1) * mm});
            skLineSegment(sketch, "E1331", {"start": v(-592.09, -76.1) * mm, "end": v(-594.72, -75.66) * mm});
            skLineSegment(sketch, "E1332", {"start": v(-594.72, -75.66) * mm, "end": v(-597.47, -75.16) * mm});
            skLineSegment(sketch, "E1333", {"start": v(-597.47, -75.16) * mm, "end": v(-600.36, -74.59) * mm});
            skLineSegment(sketch, "E1334", {"start": v(-600.36, -74.59) * mm, "end": v(-603.37, -73.94) * mm});
            skLineSegment(sketch, "E1335", {"start": v(-603.37, -73.94) * mm, "end": v(-606.5, -73.22) * mm});
            skLineSegment(sketch, "E1336", {"start": v(-606.5, -73.22) * mm, "end": v(-609.75, -72.41) * mm});
            skLineSegment(sketch, "E1337", {"start": v(-609.75, -72.41) * mm, "end": v(-613.12, -71.52) * mm});
            skLineSegment(sketch, "E1338", {"start": v(-613.12, -71.52) * mm, "end": v(-616.61, -70.54) * mm});
            skLineSegment(sketch, "E1339", {"start": v(-616.61, -70.54) * mm, "end": v(-620.22, -69.47) * mm});
            skLineSegment(sketch, "E1340", {"start": v(-620.22, -69.47) * mm, "end": v(-623.94, -68.3) * mm});
            skLineSegment(sketch, "E1341", {"start": v(-623.94, -68.3) * mm, "end": v(-627.77, -67.03) * mm});
            skLineSegment(sketch, "E1342", {"start": v(-627.77, -67.03) * mm, "end": v(-631.71, -65.66) * mm});
            skLineSegment(sketch, "E1343", {"start": v(-631.71, -65.66) * mm, "end": v(-635.76, -64.18) * mm});
            skLineSegment(sketch, "E1344", {"start": v(-635.76, -64.18) * mm, "end": v(-639.91, -62.59) * mm});
            skLineSegment(sketch, "E1345", {"start": v(-639.91, -62.59) * mm, "end": v(-644.16, -60.88) * mm});
            skLineSegment(sketch, "E1346", {"start": v(-644.16, -60.88) * mm, "end": v(-648.52, -59.05) * mm});
            skLineSegment(sketch, "E1347", {"start": v(-648.52, -59.05) * mm, "end": v(-652.97, -57.1) * mm});
            skLineSegment(sketch, "E1348", {"start": v(-652.97, -57.1) * mm, "end": v(-657.51, -55.03) * mm});
            skLineSegment(sketch, "E1349", {"start": v(-657.51, -55.03) * mm, "end": v(-662.15, -52.83) * mm});
            skLineSegment(sketch, "E1350", {"start": v(-662.15, -52.83) * mm, "end": v(-666.87, -50.5) * mm});
            skLineSegment(sketch, "E1351", {"start": v(-666.87, -50.5) * mm, "end": v(-671.68, -48.03) * mm});
            skLineSegment(sketch, "E1352", {"start": v(-671.68, -48.03) * mm, "end": v(-676.57, -45.42) * mm});
            skLineSegment(sketch, "E1353", {"start": v(-676.57, -45.42) * mm, "end": v(-681.54, -42.67) * mm});
            skLineSegment(sketch, "E1354", {"start": v(-681.54, -42.67) * mm, "end": v(-686.59, -39.77) * mm});
            skLineSegment(sketch, "E1355", {"start": v(-686.59, -39.77) * mm, "end": v(-691.7, -36.73) * mm});
            skLineSegment(sketch, "E1356", {"start": v(-691.7, -36.73) * mm, "end": v(-696.9, -33.54) * mm});
            skLineSegment(sketch, "E1357", {"start": v(-696.9, -33.54) * mm, "end": v(-702.14, -30.2) * mm});
            skLineSegment(sketch, "E1358", {"start": v(-702.14, -30.2) * mm, "end": v(-707.46, -26.7) * mm});
            skLineSegment(sketch, "E1359", {"start": v(-707.46, -26.7) * mm, "end": v(-712.83, -23.03) * mm});
            skLineSegment(sketch, "E1360", {"start": v(-712.83, -23.03) * mm, "end": v(-718.26, -19.2) * mm});
            skLineSegment(sketch, "E1361", {"start": v(-718.26, -19.2) * mm, "end": v(-723.74, -15.22) * mm});
            skLineSegment(sketch, "E1362", {"start": v(-542.7, 103.28) * mm, "end": v(-543.03, 102.33) * mm});
            skLineSegment(sketch, "E1363", {"start": v(-543.03, 102.33) * mm, "end": v(-547.21, 92.47) * mm});
            skLineSegment(sketch, "E1364", {"start": v(-547.21, 92.47) * mm, "end": v(-547.71, 91.6) * mm});
            skLineSegment(sketch, "E1365", {"start": v(-547.71, 91.6) * mm, "end": v(-548.41, 90.77) * mm});
            skLineSegment(sketch, "E1366", {"start": v(-548.41, 90.77) * mm, "end": v(-556.27, 83.6) * mm});
            skLineSegment(sketch, "E1367", {"start": v(-556.27, 83.6) * mm, "end": v(-557.1, 82.92) * mm});
            skLineSegment(sketch, "E1368", {"start": v(-557.1, 82.92) * mm, "end": v(-558.13, 82.3) * mm});
            skLineSegment(sketch, "E1369", {"start": v(-558.13, 82.3) * mm, "end": v(-559.35, 81.75) * mm});
            skLineSegment(sketch, "E1370", {"start": v(-559.35, 81.75) * mm, "end": v(-560.76, 81.27) * mm});
            skLineSegment(sketch, "E1371", {"start": v(-560.76, 81.27) * mm, "end": v(-569.29, 78.74) * mm});
            skLineSegment(sketch, "E1372", {"start": v(-569.29, 78.74) * mm, "end": v(-570.57, 78.38) * mm});
            skLineSegment(sketch, "E1373", {"start": v(-570.57, 78.38) * mm, "end": v(-572.03, 78.1) * mm});
            skLineSegment(sketch, "E1374", {"start": v(-572.03, 78.1) * mm, "end": v(-573.68, 77.89) * mm});
            skLineSegment(sketch, "E1375", {"start": v(-573.68, 77.89) * mm, "end": v(-575.5, 77.77) * mm});
            skLineSegment(sketch, "E1376", {"start": v(-575.5, 77.77) * mm, "end": v(-575.78, 77.76) * mm});
            skLineSegment(sketch, "E1377", {"start": v(-575.78, 77.76) * mm, "end": v(-577.35, 77.7) * mm});
            skLineSegment(sketch, "E1378", {"start": v(-577.35, 77.7) * mm, "end": v(-579.06, 77.6) * mm});
            skLineSegment(sketch, "E1379", {"start": v(-579.06, 77.6) * mm, "end": v(-580.9, 77.46) * mm});
            skLineSegment(sketch, "E1380", {"start": v(-580.9, 77.46) * mm, "end": v(-582.87, 77.29) * mm});
            skLineSegment(sketch, "E1381", {"start": v(-582.87, 77.29) * mm, "end": v(-584.98, 77.07) * mm});
            skLineSegment(sketch, "E1382", {"start": v(-584.98, 77.07) * mm, "end": v(-587.21, 76.8) * mm});
            skLineSegment(sketch, "E1383", {"start": v(-587.21, 76.8) * mm, "end": v(-589.59, 76.48) * mm});
            skLineSegment(sketch, "E1384", {"start": v(-589.59, 76.48) * mm, "end": v(-592.09, 76.1) * mm});
            skLineSegment(sketch, "E1385", {"start": v(-592.09, 76.1) * mm, "end": v(-594.72, 75.66) * mm});
            skLineSegment(sketch, "E1386", {"start": v(-594.72, 75.66) * mm, "end": v(-597.47, 75.16) * mm});
            skLineSegment(sketch, "E1387", {"start": v(-597.47, 75.16) * mm, "end": v(-600.36, 74.59) * mm});
            skLineSegment(sketch, "E1388", {"start": v(-600.36, 74.59) * mm, "end": v(-603.37, 73.94) * mm});
            skLineSegment(sketch, "E1389", {"start": v(-603.37, 73.94) * mm, "end": v(-606.5, 73.22) * mm});
            skLineSegment(sketch, "E1390", {"start": v(-606.5, 73.22) * mm, "end": v(-609.75, 72.41) * mm});
            skLineSegment(sketch, "E1391", {"start": v(-609.75, 72.41) * mm, "end": v(-613.12, 71.52) * mm});
            skLineSegment(sketch, "E1392", {"start": v(-613.12, 71.52) * mm, "end": v(-616.61, 70.54) * mm});
            skLineSegment(sketch, "E1393", {"start": v(-616.61, 70.54) * mm, "end": v(-620.22, 69.47) * mm});
            skLineSegment(sketch, "E1394", {"start": v(-620.22, 69.47) * mm, "end": v(-623.94, 68.3) * mm});
            skLineSegment(sketch, "E1395", {"start": v(-623.94, 68.3) * mm, "end": v(-627.77, 67.03) * mm});
            skLineSegment(sketch, "E1396", {"start": v(-627.77, 67.03) * mm, "end": v(-631.71, 65.66) * mm});
            skLineSegment(sketch, "E1397", {"start": v(-631.71, 65.66) * mm, "end": v(-635.76, 64.18) * mm});
            skLineSegment(sketch, "E1398", {"start": v(-635.76, 64.18) * mm, "end": v(-639.91, 62.59) * mm});
            skLineSegment(sketch, "E1399", {"start": v(-639.91, 62.59) * mm, "end": v(-644.16, 60.88) * mm});
            skLineSegment(sketch, "E1400", {"start": v(-644.16, 60.88) * mm, "end": v(-648.52, 59.05) * mm});
            skLineSegment(sketch, "E1401", {"start": v(-648.52, 59.05) * mm, "end": v(-652.97, 57.1) * mm});
            skLineSegment(sketch, "E1402", {"start": v(-652.97, 57.1) * mm, "end": v(-657.51, 55.03) * mm});
            skLineSegment(sketch, "E1403", {"start": v(-657.51, 55.03) * mm, "end": v(-662.15, 52.83) * mm});
            skLineSegment(sketch, "E1404", {"start": v(-662.15, 52.83) * mm, "end": v(-666.87, 50.5) * mm});
            skLineSegment(sketch, "E1405", {"start": v(-666.87, 50.5) * mm, "end": v(-671.68, 48.03) * mm});
            skLineSegment(sketch, "E1406", {"start": v(-671.68, 48.03) * mm, "end": v(-676.57, 45.42) * mm});
            skLineSegment(sketch, "E1407", {"start": v(-676.57, 45.42) * mm, "end": v(-681.54, 42.67) * mm});
            skLineSegment(sketch, "E1408", {"start": v(-681.54, 42.67) * mm, "end": v(-686.59, 39.77) * mm});
            skLineSegment(sketch, "E1409", {"start": v(-686.59, 39.77) * mm, "end": v(-691.7, 36.73) * mm});
            skLineSegment(sketch, "E1410", {"start": v(-691.7, 36.73) * mm, "end": v(-696.9, 33.54) * mm});
            skLineSegment(sketch, "E1411", {"start": v(-696.9, 33.54) * mm, "end": v(-702.14, 30.2) * mm});
            skLineSegment(sketch, "E1412", {"start": v(-702.14, 30.2) * mm, "end": v(-707.46, 26.7) * mm});
            skLineSegment(sketch, "E1413", {"start": v(-707.46, 26.7) * mm, "end": v(-712.83, 23.03) * mm});
            skLineSegment(sketch, "E1414", {"start": v(-712.83, 23.03) * mm, "end": v(-718.26, 19.2) * mm});
            skLineSegment(sketch, "E1415", {"start": v(-718.26, 19.2) * mm, "end": v(-723.74, 15.22) * mm});
            skArc(sketch, "E1416", {"start": v(-723.74, 15.22) * mm, "mid": v(-723.9, 0) * mm, "end": v(-723.74, -15.22) * mm});
            skLineSegment(sketch, "E1417", {"start": v(-540.92, 112.27) * mm, "end": v(-540.85, 113.27) * mm});
            skLineSegment(sketch, "E1418", {"start": v(-540.85, 113.27) * mm, "end": v(-540.94, 123.98) * mm});
            skLineSegment(sketch, "E1419", {"start": v(-540.94, 123.98) * mm, "end": v(-541.07, 124.98) * mm});
            skLineSegment(sketch, "E1420", {"start": v(-541.07, 124.98) * mm, "end": v(-541.4, 126) * mm});
            skLineSegment(sketch, "E1421", {"start": v(-541.4, 126) * mm, "end": v(-545.92, 135.64) * mm});
            skLineSegment(sketch, "E1422", {"start": v(-545.92, 135.64) * mm, "end": v(-546.43, 136.59) * mm});
            skLineSegment(sketch, "E1423", {"start": v(-546.43, 136.59) * mm, "end": v(-547.15, 137.55) * mm});
            skLineSegment(sketch, "E1424", {"start": v(-547.15, 137.55) * mm, "end": v(-548.06, 138.53) * mm});
            skLineSegment(sketch, "E1425", {"start": v(-548.06, 138.53) * mm, "end": v(-549.18, 139.5) * mm});
            skLineSegment(sketch, "E1426", {"start": v(-549.18, 139.5) * mm, "end": v(-556.09, 145.11) * mm});
            skLineSegment(sketch, "E1427", {"start": v(-556.09, 145.11) * mm, "end": v(-557.13, 145.93) * mm});
            skLineSegment(sketch, "E1428", {"start": v(-557.13, 145.93) * mm, "end": v(-558.38, 146.76) * mm});
            skLineSegment(sketch, "E1429", {"start": v(-558.38, 146.76) * mm, "end": v(-559.82, 147.58) * mm});
            skLineSegment(sketch, "E1430", {"start": v(-559.82, 147.58) * mm, "end": v(-561.46, 148.4) * mm});
            skLineSegment(sketch, "E1431", {"start": v(-561.46, 148.4) * mm, "end": v(-561.7, 148.5) * mm});
            skLineSegment(sketch, "E1432", {"start": v(-561.7, 148.5) * mm, "end": v(-563.13, 149.17) * mm});
            skLineSegment(sketch, "E1433", {"start": v(-563.13, 149.17) * mm, "end": v(-564.67, 149.9) * mm});
            skLineSegment(sketch, "E1434", {"start": v(-564.67, 149.9) * mm, "end": v(-566.32, 150.74) * mm});
            skLineSegment(sketch, "E1435", {"start": v(-566.32, 150.74) * mm, "end": v(-568.08, 151.65) * mm});
            skLineSegment(sketch, "E1436", {"start": v(-568.08, 151.65) * mm, "end": v(-569.94, 152.66) * mm});
            skLineSegment(sketch, "E1437", {"start": v(-569.94, 152.66) * mm, "end": v(-571.9, 153.76) * mm});
            skLineSegment(sketch, "E1438", {"start": v(-571.9, 153.76) * mm, "end": v(-573.97, 154.97) * mm});
            skLineSegment(sketch, "E1439", {"start": v(-573.97, 154.97) * mm, "end": v(-576.14, 156.27) * mm});
            skLineSegment(sketch, "E1440", {"start": v(-576.14, 156.27) * mm, "end": v(-578.4, 157.68) * mm});
            skLineSegment(sketch, "E1441", {"start": v(-578.4, 157.68) * mm, "end": v(-580.76, 159.2) * mm});
            skLineSegment(sketch, "E1442", {"start": v(-580.76, 159.2) * mm, "end": v(-583.2, 160.84) * mm});
            skLineSegment(sketch, "E1443", {"start": v(-583.2, 160.84) * mm, "end": v(-585.73, 162.59) * mm});
            skLineSegment(sketch, "E1444", {"start": v(-585.73, 162.59) * mm, "end": v(-588.35, 164.45) * mm});
            skLineSegment(sketch, "E1445", {"start": v(-588.35, 164.45) * mm, "end": v(-591.05, 166.44) * mm});
            skLineSegment(sketch, "E1446", {"start": v(-591.05, 166.44) * mm, "end": v(-593.82, 168.55) * mm});
            skLineSegment(sketch, "E1447", {"start": v(-593.82, 168.55) * mm, "end": v(-596.67, 170.8) * mm});
            skLineSegment(sketch, "E1448", {"start": v(-596.67, 170.8) * mm, "end": v(-599.6, 173.16) * mm});
            skLineSegment(sketch, "E1449", {"start": v(-599.6, 173.16) * mm, "end": v(-602.58, 175.67) * mm});
            skLineSegment(sketch, "E1450", {"start": v(-602.58, 175.67) * mm, "end": v(-605.64, 178.3) * mm});
            skLineSegment(sketch, "E1451", {"start": v(-605.64, 178.3) * mm, "end": v(-608.75, 181.08) * mm});
            skLineSegment(sketch, "E1452", {"start": v(-608.75, 181.08) * mm, "end": v(-611.92, 184) * mm});
            skLineSegment(sketch, "E1453", {"start": v(-611.92, 184) * mm, "end": v(-615.15, 187.06) * mm});
            skLineSegment(sketch, "E1454", {"start": v(-615.15, 187.06) * mm, "end": v(-618.43, 190.26) * mm});
            skLineSegment(sketch, "E1455", {"start": v(-618.43, 190.26) * mm, "end": v(-621.75, 193.62) * mm});
            skLineSegment(sketch, "E1456", {"start": v(-621.75, 193.62) * mm, "end": v(-625.12, 197.12) * mm});
            skLineSegment(sketch, "E1457", {"start": v(-625.12, 197.12) * mm, "end": v(-628.52, 200.77) * mm});
            skLineSegment(sketch, "E1458", {"start": v(-628.52, 200.77) * mm, "end": v(-631.96, 204.58) * mm});
            skLineSegment(sketch, "E1459", {"start": v(-631.96, 204.58) * mm, "end": v(-635.43, 208.55) * mm});
            skLineSegment(sketch, "E1460", {"start": v(-635.43, 208.55) * mm, "end": v(-638.93, 212.67) * mm});
            skLineSegment(sketch, "E1461", {"start": v(-638.93, 212.67) * mm, "end": v(-642.45, 216.95) * mm});
            skLineSegment(sketch, "E1462", {"start": v(-642.45, 216.95) * mm, "end": v(-646, 221.4) * mm});
            skLineSegment(sketch, "E1463", {"start": v(-646, 221.4) * mm, "end": v(-649.54, 226) * mm});
            skLineSegment(sketch, "E1464", {"start": v(-649.54, 226) * mm, "end": v(-653.1, 230.77) * mm});
            skLineSegment(sketch, "E1465", {"start": v(-653.1, 230.77) * mm, "end": v(-656.68, 235.7) * mm});
            skLineSegment(sketch, "E1466", {"start": v(-656.68, 235.7) * mm, "end": v(-660.25, 240.8) * mm});
            skLineSegment(sketch, "E1467", {"start": v(-660.25, 240.8) * mm, "end": v(-663.82, 246.07) * mm});
            skLineSegment(sketch, "E1468", {"start": v(-663.82, 246.07) * mm, "end": v(-667.38, 251.51) * mm});
            skLineSegment(sketch, "E1469", {"start": v(-667.38, 251.51) * mm, "end": v(-670.93, 257.12) * mm});
            skLineSegment(sketch, "E1470", {"start": v(-670.93, 257.12) * mm, "end": v(-674.47, 262.9) * mm});
            skLineSegment(sketch, "E1471", {"start": v(-461.87, 303.1) * mm, "end": v(-462.53, 302.34) * mm});
            skLineSegment(sketch, "E1472", {"start": v(-462.53, 302.34) * mm, "end": v(-470.17, 294.84) * mm});
            skLineSegment(sketch, "E1473", {"start": v(-470.17, 294.84) * mm, "end": v(-470.97, 294.22) * mm});
            skLineSegment(sketch, "E1474", {"start": v(-470.97, 294.22) * mm, "end": v(-471.93, 293.73) * mm});
            skLineSegment(sketch, "E1475", {"start": v(-471.93, 293.73) * mm, "end": v(-481.93, 290.1) * mm});
            skLineSegment(sketch, "E1476", {"start": v(-481.93, 290.1) * mm, "end": v(-482.97, 289.8) * mm});
            skLineSegment(sketch, "E1477", {"start": v(-482.97, 289.8) * mm, "end": v(-484.15, 289.63) * mm});
            skLineSegment(sketch, "E1478", {"start": v(-484.15, 289.63) * mm, "end": v(-485.49, 289.59) * mm});
            skLineSegment(sketch, "E1479", {"start": v(-485.49, 289.59) * mm, "end": v(-486.97, 289.68) * mm});
            skLineSegment(sketch, "E1480", {"start": v(-486.97, 289.68) * mm, "end": v(-495.82, 290.6) * mm});
            skLineSegment(sketch, "E1481", {"start": v(-495.82, 290.6) * mm, "end": v(-497.14, 290.76) * mm});
            skLineSegment(sketch, "E1482", {"start": v(-497.14, 290.76) * mm, "end": v(-498.6, 291.06) * mm});
            skLineSegment(sketch, "E1483", {"start": v(-498.6, 291.06) * mm, "end": v(-500.2, 291.5) * mm});
            skLineSegment(sketch, "E1484", {"start": v(-500.2, 291.5) * mm, "end": v(-501.94, 292.08) * mm});
            skLineSegment(sketch, "E1485", {"start": v(-501.94, 292.08) * mm, "end": v(-502.2, 292.18) * mm});
            skLineSegment(sketch, "E1486", {"start": v(-502.2, 292.18) * mm, "end": v(-503.67, 292.72) * mm});
            skLineSegment(sketch, "E1487", {"start": v(-503.67, 292.72) * mm, "end": v(-505.28, 293.28) * mm});
            skLineSegment(sketch, "E1488", {"start": v(-505.28, 293.28) * mm, "end": v(-507.03, 293.86) * mm});
            skLineSegment(sketch, "E1489", {"start": v(-507.03, 293.86) * mm, "end": v(-508.92, 294.46) * mm});
            skLineSegment(sketch, "E1490", {"start": v(-508.92, 294.46) * mm, "end": v(-510.95, 295.06) * mm});
            skLineSegment(sketch, "E1491", {"start": v(-510.95, 295.06) * mm, "end": v(-513.13, 295.67) * mm});
            skLineSegment(sketch, "E1492", {"start": v(-513.13, 295.67) * mm, "end": v(-515.44, 296.28) * mm});
            skLineSegment(sketch, "E1493", {"start": v(-515.44, 296.28) * mm, "end": v(-517.9, 296.9) * mm});
            skLineSegment(sketch, "E1494", {"start": v(-517.9, 296.9) * mm, "end": v(-520.5, 297.5) * mm});
            skLineSegment(sketch, "E1495", {"start": v(-520.5, 297.5) * mm, "end": v(-523.23, 298.08) * mm});
            skLineSegment(sketch, "E1496", {"start": v(-523.23, 298.08) * mm, "end": v(-526.11, 298.66) * mm});
            skLineSegment(sketch, "E1497", {"start": v(-526.11, 298.66) * mm, "end": v(-529.14, 299.21) * mm});
            skLineSegment(sketch, "E1498", {"start": v(-529.14, 299.21) * mm, "end": v(-532.31, 299.74) * mm});
            skLineSegment(sketch, "E1499", {"start": v(-532.31, 299.74) * mm, "end": v(-535.62, 300.24) * mm});
            skLineSegment(sketch, "E1500", {"start": v(-535.62, 300.24) * mm, "end": v(-539.08, 300.71) * mm});
            skLineSegment(sketch, "E1501", {"start": v(-539.08, 300.71) * mm, "end": v(-542.68, 301.14) * mm});
            skLineSegment(sketch, "E1502", {"start": v(-542.68, 301.14) * mm, "end": v(-546.42, 301.53) * mm});
            skLineSegment(sketch, "E1503", {"start": v(-546.42, 301.53) * mm, "end": v(-550.3, 301.88) * mm});
            skLineSegment(sketch, "E1504", {"start": v(-550.3, 301.88) * mm, "end": v(-554.33, 302.17) * mm});
            skLineSegment(sketch, "E1505", {"start": v(-554.33, 302.17) * mm, "end": v(-558.5, 302.4) * mm});
            skLineSegment(sketch, "E1506", {"start": v(-558.5, 302.4) * mm, "end": v(-562.8, 302.59) * mm});
            skLineSegment(sketch, "E1507", {"start": v(-562.8, 302.59) * mm, "end": v(-567.25, 302.7) * mm});
            skLineSegment(sketch, "E1508", {"start": v(-567.25, 302.7) * mm, "end": v(-571.83, 302.76) * mm});
            skLineSegment(sketch, "E1509", {"start": v(-571.83, 302.76) * mm, "end": v(-576.55, 302.74) * mm});
            skLineSegment(sketch, "E1510", {"start": v(-576.55, 302.74) * mm, "end": v(-581.41, 302.64) * mm});
            skLineSegment(sketch, "E1511", {"start": v(-581.41, 302.64) * mm, "end": v(-586.4, 302.46) * mm});
            skLineSegment(sketch, "E1512", {"start": v(-586.4, 302.46) * mm, "end": v(-591.53, 302.2) * mm});
            skLineSegment(sketch, "E1513", {"start": v(-591.53, 302.2) * mm, "end": v(-596.78, 301.85) * mm});
            skLineSegment(sketch, "E1514", {"start": v(-596.78, 301.85) * mm, "end": v(-602.17, 301.41) * mm});
            skLineSegment(sketch, "E1515", {"start": v(-602.17, 301.41) * mm, "end": v(-607.69, 300.87) * mm});
            skLineSegment(sketch, "E1516", {"start": v(-607.69, 300.87) * mm, "end": v(-613.33, 300.24) * mm});
            skLineSegment(sketch, "E1517", {"start": v(-613.33, 300.24) * mm, "end": v(-619.1, 299.5) * mm});
            skLineSegment(sketch, "E1518", {"start": v(-619.1, 299.5) * mm, "end": v(-625, 298.64) * mm});
            skLineSegment(sketch, "E1519", {"start": v(-625, 298.64) * mm, "end": v(-631, 297.67) * mm});
            skLineSegment(sketch, "E1520", {"start": v(-631, 297.67) * mm, "end": v(-637.14, 296.6) * mm});
            skLineSegment(sketch, "E1521", {"start": v(-637.14, 296.6) * mm, "end": v(-643.4, 295.4) * mm});
            skLineSegment(sketch, "E1522", {"start": v(-643.4, 295.4) * mm, "end": v(-649.76, 294.06) * mm});
            skLineSegment(sketch, "E1523", {"start": v(-649.76, 294.06) * mm, "end": v(-656.23, 292.6) * mm});
            skLineSegment(sketch, "E1524", {"start": v(-656.23, 292.6) * mm, "end": v(-662.82, 291.02) * mm});
            skArc(sketch, "E1525", {"start": v(-662.82, 291.02) * mm, "mid": v(-668.8, 277.02) * mm, "end": v(-674.47, 262.9) * mm});
            skLineSegment(sketch, "E1526", {"start": v(-456.78, 310.72) * mm, "end": v(-456.33, 311.62) * mm});
            skLineSegment(sketch, "E1527", {"start": v(-456.33, 311.62) * mm, "end": v(-452.32, 321.55) * mm});
            skLineSegment(sketch, "E1528", {"start": v(-452.32, 321.55) * mm, "end": v(-452.06, 322.53) * mm});
            skLineSegment(sketch, "E1529", {"start": v(-452.06, 322.53) * mm, "end": v(-451.97, 323.6) * mm});
            skLineSegment(sketch, "E1530", {"start": v(-451.97, 323.6) * mm, "end": v(-452.45, 334.23) * mm});
            skLineSegment(sketch, "E1531", {"start": v(-452.45, 334.23) * mm, "end": v(-452.57, 335.3) * mm});
            skLineSegment(sketch, "E1532", {"start": v(-452.57, 335.3) * mm, "end": v(-452.86, 336.46) * mm});
            skLineSegment(sketch, "E1533", {"start": v(-452.86, 336.46) * mm, "end": v(-453.33, 337.71) * mm});
            skLineSegment(sketch, "E1534", {"start": v(-453.33, 337.71) * mm, "end": v(-453.99, 339.05) * mm});
            skLineSegment(sketch, "E1535", {"start": v(-453.99, 339.05) * mm, "end": v(-458.22, 346.87) * mm});
            skLineSegment(sketch, "E1536", {"start": v(-458.22, 346.87) * mm, "end": v(-458.88, 348.03) * mm});
            skLineSegment(sketch, "E1537", {"start": v(-458.88, 348.03) * mm, "end": v(-459.71, 349.27) * mm});
            skLineSegment(sketch, "E1538", {"start": v(-459.71, 349.27) * mm, "end": v(-460.73, 350.58) * mm});
            skLineSegment(sketch, "E1539", {"start": v(-460.73, 350.58) * mm, "end": v(-461.94, 351.96) * mm});
            skLineSegment(sketch, "E1540", {"start": v(-461.94, 351.96) * mm, "end": v(-462.12, 352.16) * mm});
            skLineSegment(sketch, "E1541", {"start": v(-462.12, 352.16) * mm, "end": v(-463.18, 353.31) * mm});
            skLineSegment(sketch, "E1542", {"start": v(-463.18, 353.31) * mm, "end": v(-464.32, 354.59) * mm});
            skLineSegment(sketch, "E1543", {"start": v(-464.32, 354.59) * mm, "end": v(-465.53, 355.98) * mm});
            skLineSegment(sketch, "E1544", {"start": v(-465.53, 355.98) * mm, "end": v(-466.8, 357.5) * mm});
            skLineSegment(sketch, "E1545", {"start": v(-466.8, 357.5) * mm, "end": v(-468.13, 359.15) * mm});
            skLineSegment(sketch, "E1546", {"start": v(-468.13, 359.15) * mm, "end": v(-469.53, 360.92) * mm});
            skLineSegment(sketch, "E1547", {"start": v(-469.53, 360.92) * mm, "end": v(-470.98, 362.82) * mm});
            skLineSegment(sketch, "E1548", {"start": v(-470.98, 362.82) * mm, "end": v(-472.48, 364.86) * mm});
            skLineSegment(sketch, "E1549", {"start": v(-472.48, 364.86) * mm, "end": v(-474.03, 367.03) * mm});
            skLineSegment(sketch, "E1550", {"start": v(-474.03, 367.03) * mm, "end": v(-475.62, 369.33) * mm});
            skLineSegment(sketch, "E1551", {"start": v(-475.62, 369.33) * mm, "end": v(-477.26, 371.78) * mm});
            skLineSegment(sketch, "E1552", {"start": v(-477.26, 371.78) * mm, "end": v(-478.93, 374.36) * mm});
            skLineSegment(sketch, "E1553", {"start": v(-478.93, 374.36) * mm, "end": v(-480.63, 377.09) * mm});
            skLineSegment(sketch, "E1554", {"start": v(-480.63, 377.09) * mm, "end": v(-482.36, 379.95) * mm});
            skLineSegment(sketch, "E1555", {"start": v(-482.36, 379.95) * mm, "end": v(-484.12, 382.97) * mm});
            skLineSegment(sketch, "E1556", {"start": v(-484.12, 382.97) * mm, "end": v(-485.9, 386.13) * mm});
            skLineSegment(sketch, "E1557", {"start": v(-485.9, 386.13) * mm, "end": v(-487.69, 389.44) * mm});
            skLineSegment(sketch, "E1558", {"start": v(-487.69, 389.44) * mm, "end": v(-489.49, 392.9) * mm});
            skLineSegment(sketch, "E1559", {"start": v(-489.49, 392.9) * mm, "end": v(-491.3, 396.5) * mm});
            skLineSegment(sketch, "E1560", {"start": v(-491.3, 396.5) * mm, "end": v(-493.12, 400.26) * mm});
            skLineSegment(sketch, "E1561", {"start": v(-493.12, 400.26) * mm, "end": v(-494.93, 404.17) * mm});
            skLineSegment(sketch, "E1562", {"start": v(-494.93, 404.17) * mm, "end": v(-496.74, 408.23) * mm});
            skLineSegment(sketch, "E1563", {"start": v(-496.74, 408.23) * mm, "end": v(-498.54, 412.44) * mm});
            skLineSegment(sketch, "E1564", {"start": v(-498.54, 412.44) * mm, "end": v(-500.33, 416.81) * mm});
            skLineSegment(sketch, "E1565", {"start": v(-500.33, 416.81) * mm, "end": v(-502.1, 421.34) * mm});
            skLineSegment(sketch, "E1566", {"start": v(-502.1, 421.34) * mm, "end": v(-503.85, 426.02) * mm});
            skLineSegment(sketch, "E1567", {"start": v(-503.85, 426.02) * mm, "end": v(-505.57, 430.85) * mm});
            skLineSegment(sketch, "E1568", {"start": v(-505.57, 430.85) * mm, "end": v(-507.26, 435.84) * mm});
            skLineSegment(sketch, "E1569", {"start": v(-507.26, 435.84) * mm, "end": v(-508.9, 440.99) * mm});
            skLineSegment(sketch, "E1570", {"start": v(-508.9, 440.99) * mm, "end": v(-510.52, 446.3) * mm});
            skLineSegment(sketch, "E1571", {"start": v(-510.52, 446.3) * mm, "end": v(-512.1, 451.75) * mm});
            skLineSegment(sketch, "E1572", {"start": v(-512.1, 451.75) * mm, "end": v(-513.61, 457.37) * mm});
            skLineSegment(sketch, "E1573", {"start": v(-513.61, 457.37) * mm, "end": v(-515.08, 463.14) * mm});
            skLineSegment(sketch, "E1574", {"start": v(-515.08, 463.14) * mm, "end": v(-516.5, 469.06) * mm});
            skLineSegment(sketch, "E1575", {"start": v(-516.5, 469.06) * mm, "end": v(-517.84, 475.14) * mm});
            skLineSegment(sketch, "E1576", {"start": v(-517.84, 475.14) * mm, "end": v(-519.12, 481.38) * mm});
            skLineSegment(sketch, "E1577", {"start": v(-519.12, 481.38) * mm, "end": v(-520.33, 487.76) * mm});
            skLineSegment(sketch, "E1578", {"start": v(-520.33, 487.76) * mm, "end": v(-521.47, 494.3) * mm});
            skLineSegment(sketch, "E1579", {"start": v(-521.47, 494.3) * mm, "end": v(-522.52, 501) * mm});
            skLineSegment(sketch, "E1580", {"start": v(-310.72, 456.78) * mm, "end": v(-311.62, 456.33) * mm});
            skLineSegment(sketch, "E1581", {"start": v(-311.62, 456.33) * mm, "end": v(-321.55, 452.32) * mm});
            skLineSegment(sketch, "E1582", {"start": v(-321.55, 452.32) * mm, "end": v(-322.53, 452.06) * mm});
            skLineSegment(sketch, "E1583", {"start": v(-322.53, 452.06) * mm, "end": v(-323.6, 451.97) * mm});
            skLineSegment(sketch, "E1584", {"start": v(-323.6, 451.97) * mm, "end": v(-334.23, 452.45) * mm});
            skLineSegment(sketch, "E1585", {"start": v(-334.23, 452.45) * mm, "end": v(-335.3, 452.57) * mm});
            skLineSegment(sketch, "E1586", {"start": v(-335.3, 452.57) * mm, "end": v(-336.46, 452.86) * mm});
            skLineSegment(sketch, "E1587", {"start": v(-336.46, 452.86) * mm, "end": v(-337.71, 453.33) * mm});
            skLineSegment(sketch, "E1588", {"start": v(-337.71, 453.33) * mm, "end": v(-339.05, 453.99) * mm});
            skLineSegment(sketch, "E1589", {"start": v(-339.05, 453.99) * mm, "end": v(-346.87, 458.22) * mm});
            skLineSegment(sketch, "E1590", {"start": v(-346.87, 458.22) * mm, "end": v(-348.03, 458.88) * mm});
            skLineSegment(sketch, "E1591", {"start": v(-348.03, 458.88) * mm, "end": v(-349.27, 459.71) * mm});
            skLineSegment(sketch, "E1592", {"start": v(-349.27, 459.71) * mm, "end": v(-350.58, 460.73) * mm});
            skLineSegment(sketch, "E1593", {"start": v(-350.58, 460.73) * mm, "end": v(-351.96, 461.94) * mm});
            skLineSegment(sketch, "E1594", {"start": v(-351.96, 461.94) * mm, "end": v(-352.16, 462.12) * mm});
            skLineSegment(sketch, "E1595", {"start": v(-352.16, 462.12) * mm, "end": v(-353.31, 463.18) * mm});
            skLineSegment(sketch, "E1596", {"start": v(-353.31, 463.18) * mm, "end": v(-354.59, 464.32) * mm});
            skLineSegment(sketch, "E1597", {"start": v(-354.59, 464.32) * mm, "end": v(-355.98, 465.53) * mm});
            skLineSegment(sketch, "E1598", {"start": v(-355.98, 465.53) * mm, "end": v(-357.5, 466.8) * mm});
            skLineSegment(sketch, "E1599", {"start": v(-357.5, 466.8) * mm, "end": v(-359.15, 468.13) * mm});
            skLineSegment(sketch, "E1600", {"start": v(-359.15, 468.13) * mm, "end": v(-360.92, 469.53) * mm});
            skLineSegment(sketch, "E1601", {"start": v(-360.92, 469.53) * mm, "end": v(-362.82, 470.98) * mm});
            skLineSegment(sketch, "E1602", {"start": v(-362.82, 470.98) * mm, "end": v(-364.86, 472.48) * mm});
            skLineSegment(sketch, "E1603", {"start": v(-364.86, 472.48) * mm, "end": v(-367.03, 474.03) * mm});
            skLineSegment(sketch, "E1604", {"start": v(-367.03, 474.03) * mm, "end": v(-369.33, 475.62) * mm});
            skLineSegment(sketch, "E1605", {"start": v(-369.33, 475.62) * mm, "end": v(-371.78, 477.26) * mm});
            skLineSegment(sketch, "E1606", {"start": v(-371.78, 477.26) * mm, "end": v(-374.36, 478.93) * mm});
            skLineSegment(sketch, "E1607", {"start": v(-374.36, 478.93) * mm, "end": v(-377.09, 480.63) * mm});
            skLineSegment(sketch, "E1608", {"start": v(-377.09, 480.63) * mm, "end": v(-379.95, 482.36) * mm});
            skLineSegment(sketch, "E1609", {"start": v(-379.95, 482.36) * mm, "end": v(-382.97, 484.12) * mm});
            skLineSegment(sketch, "E1610", {"start": v(-382.97, 484.12) * mm, "end": v(-386.13, 485.9) * mm});
            skLineSegment(sketch, "E1611", {"start": v(-386.13, 485.9) * mm, "end": v(-389.44, 487.69) * mm});
            skLineSegment(sketch, "E1612", {"start": v(-389.44, 487.69) * mm, "end": v(-392.9, 489.49) * mm});
            skLineSegment(sketch, "E1613", {"start": v(-392.9, 489.49) * mm, "end": v(-396.5, 491.3) * mm});
            skLineSegment(sketch, "E1614", {"start": v(-396.5, 491.3) * mm, "end": v(-400.26, 493.12) * mm});
            skLineSegment(sketch, "E1615", {"start": v(-400.26, 493.12) * mm, "end": v(-404.17, 494.93) * mm});
            skLineSegment(sketch, "E1616", {"start": v(-404.17, 494.93) * mm, "end": v(-408.23, 496.74) * mm});
            skLineSegment(sketch, "E1617", {"start": v(-408.23, 496.74) * mm, "end": v(-412.44, 498.54) * mm});
            skLineSegment(sketch, "E1618", {"start": v(-412.44, 498.54) * mm, "end": v(-416.81, 500.33) * mm});
            skLineSegment(sketch, "E1619", {"start": v(-416.81, 500.33) * mm, "end": v(-421.34, 502.1) * mm});
            skLineSegment(sketch, "E1620", {"start": v(-421.34, 502.1) * mm, "end": v(-426.02, 503.85) * mm});
            skLineSegment(sketch, "E1621", {"start": v(-426.02, 503.85) * mm, "end": v(-430.85, 505.57) * mm});
            skLineSegment(sketch, "E1622", {"start": v(-430.85, 505.57) * mm, "end": v(-435.84, 507.26) * mm});
            skLineSegment(sketch, "E1623", {"start": v(-435.84, 507.26) * mm, "end": v(-440.99, 508.9) * mm});
            skLineSegment(sketch, "E1624", {"start": v(-440.99, 508.9) * mm, "end": v(-446.3, 510.52) * mm});
            skLineSegment(sketch, "E1625", {"start": v(-446.3, 510.52) * mm, "end": v(-451.75, 512.1) * mm});
            skLineSegment(sketch, "E1626", {"start": v(-451.75, 512.1) * mm, "end": v(-457.37, 513.61) * mm});
            skLineSegment(sketch, "E1627", {"start": v(-457.37, 513.61) * mm, "end": v(-463.14, 515.08) * mm});
            skLineSegment(sketch, "E1628", {"start": v(-463.14, 515.08) * mm, "end": v(-469.06, 516.5) * mm});
            skLineSegment(sketch, "E1629", {"start": v(-469.06, 516.5) * mm, "end": v(-475.14, 517.84) * mm});
            skLineSegment(sketch, "E1630", {"start": v(-475.14, 517.84) * mm, "end": v(-481.38, 519.12) * mm});
            skLineSegment(sketch, "E1631", {"start": v(-481.38, 519.12) * mm, "end": v(-487.76, 520.33) * mm});
            skLineSegment(sketch, "E1632", {"start": v(-487.76, 520.33) * mm, "end": v(-494.3, 521.47) * mm});
            skLineSegment(sketch, "E1633", {"start": v(-494.3, 521.47) * mm, "end": v(-501, 522.52) * mm});
            skArc(sketch, "E1634", {"start": v(-501, 522.52) * mm, "mid": v(-511.87, 511.87) * mm, "end": v(-522.52, 501) * mm});
            skLineSegment(sketch, "E1635", {"start": v(-303.1, 461.87) * mm, "end": v(-302.34, 462.53) * mm});
            skLineSegment(sketch, "E1636", {"start": v(-302.34, 462.53) * mm, "end": v(-294.84, 470.17) * mm});
            skLineSegment(sketch, "E1637", {"start": v(-294.84, 470.17) * mm, "end": v(-294.22, 470.97) * mm});
            skLineSegment(sketch, "E1638", {"start": v(-294.22, 470.97) * mm, "end": v(-293.73, 471.93) * mm});
            skLineSegment(sketch, "E1639", {"start": v(-293.73, 471.93) * mm, "end": v(-290.1, 481.93) * mm});
            skLineSegment(sketch, "E1640", {"start": v(-290.1, 481.93) * mm, "end": v(-289.8, 482.97) * mm});
            skLineSegment(sketch, "E1641", {"start": v(-289.8, 482.97) * mm, "end": v(-289.63, 484.15) * mm});
            skLineSegment(sketch, "E1642", {"start": v(-289.63, 484.15) * mm, "end": v(-289.59, 485.49) * mm});
            skLineSegment(sketch, "E1643", {"start": v(-289.59, 485.49) * mm, "end": v(-289.68, 486.97) * mm});
            skLineSegment(sketch, "E1644", {"start": v(-289.68, 486.97) * mm, "end": v(-290.6, 495.82) * mm});
            skLineSegment(sketch, "E1645", {"start": v(-290.6, 495.82) * mm, "end": v(-290.76, 497.14) * mm});
            skLineSegment(sketch, "E1646", {"start": v(-290.76, 497.14) * mm, "end": v(-291.06, 498.6) * mm});
            skLineSegment(sketch, "E1647", {"start": v(-291.06, 498.6) * mm, "end": v(-291.5, 500.2) * mm});
            skLineSegment(sketch, "E1648", {"start": v(-291.5, 500.2) * mm, "end": v(-292.08, 501.94) * mm});
            skLineSegment(sketch, "E1649", {"start": v(-292.08, 501.94) * mm, "end": v(-292.18, 502.2) * mm});
            skLineSegment(sketch, "E1650", {"start": v(-292.18, 502.2) * mm, "end": v(-292.72, 503.67) * mm});
            skLineSegment(sketch, "E1651", {"start": v(-292.72, 503.67) * mm, "end": v(-293.28, 505.28) * mm});
            skLineSegment(sketch, "E1652", {"start": v(-293.28, 505.28) * mm, "end": v(-293.86, 507.03) * mm});
            skLineSegment(sketch, "E1653", {"start": v(-293.86, 507.03) * mm, "end": v(-294.46, 508.92) * mm});
            skLineSegment(sketch, "E1654", {"start": v(-294.46, 508.92) * mm, "end": v(-295.06, 510.95) * mm});
            skLineSegment(sketch, "E1655", {"start": v(-295.06, 510.95) * mm, "end": v(-295.67, 513.13) * mm});
            skLineSegment(sketch, "E1656", {"start": v(-295.67, 513.13) * mm, "end": v(-296.28, 515.44) * mm});
            skLineSegment(sketch, "E1657", {"start": v(-296.28, 515.44) * mm, "end": v(-296.9, 517.9) * mm});
            skLineSegment(sketch, "E1658", {"start": v(-296.9, 517.9) * mm, "end": v(-297.5, 520.5) * mm});
            skLineSegment(sketch, "E1659", {"start": v(-297.5, 520.5) * mm, "end": v(-298.08, 523.23) * mm});
            skLineSegment(sketch, "E1660", {"start": v(-298.08, 523.23) * mm, "end": v(-298.66, 526.11) * mm});
            skLineSegment(sketch, "E1661", {"start": v(-298.66, 526.11) * mm, "end": v(-299.21, 529.14) * mm});
            skLineSegment(sketch, "E1662", {"start": v(-299.21, 529.14) * mm, "end": v(-299.74, 532.31) * mm});
            skLineSegment(sketch, "E1663", {"start": v(-299.74, 532.31) * mm, "end": v(-300.24, 535.62) * mm});
            skLineSegment(sketch, "E1664", {"start": v(-300.24, 535.62) * mm, "end": v(-300.71, 539.08) * mm});
            skLineSegment(sketch, "E1665", {"start": v(-300.71, 539.08) * mm, "end": v(-301.14, 542.68) * mm});
            skLineSegment(sketch, "E1666", {"start": v(-301.14, 542.68) * mm, "end": v(-301.53, 546.42) * mm});
            skLineSegment(sketch, "E1667", {"start": v(-301.53, 546.42) * mm, "end": v(-301.88, 550.3) * mm});
            skLineSegment(sketch, "E1668", {"start": v(-301.88, 550.3) * mm, "end": v(-302.17, 554.33) * mm});
            skLineSegment(sketch, "E1669", {"start": v(-302.17, 554.33) * mm, "end": v(-302.4, 558.5) * mm});
            skLineSegment(sketch, "E1670", {"start": v(-302.4, 558.5) * mm, "end": v(-302.59, 562.8) * mm});
            skLineSegment(sketch, "E1671", {"start": v(-302.59, 562.8) * mm, "end": v(-302.7, 567.25) * mm});
            skLineSegment(sketch, "E1672", {"start": v(-302.7, 567.25) * mm, "end": v(-302.76, 571.83) * mm});
            skLineSegment(sketch, "E1673", {"start": v(-302.76, 571.83) * mm, "end": v(-302.74, 576.55) * mm});
            skLineSegment(sketch, "E1674", {"start": v(-302.74, 576.55) * mm, "end": v(-302.64, 581.41) * mm});
            skLineSegment(sketch, "E1675", {"start": v(-302.64, 581.41) * mm, "end": v(-302.46, 586.4) * mm});
            skLineSegment(sketch, "E1676", {"start": v(-302.46, 586.4) * mm, "end": v(-302.2, 591.53) * mm});
            skLineSegment(sketch, "E1677", {"start": v(-302.2, 591.53) * mm, "end": v(-301.85, 596.78) * mm});
            skLineSegment(sketch, "E1678", {"start": v(-301.85, 596.78) * mm, "end": v(-301.41, 602.17) * mm});
            skLineSegment(sketch, "E1679", {"start": v(-301.41, 602.17) * mm, "end": v(-300.87, 607.69) * mm});
            skLineSegment(sketch, "E1680", {"start": v(-300.87, 607.69) * mm, "end": v(-300.24, 613.33) * mm});
            skLineSegment(sketch, "E1681", {"start": v(-300.24, 613.33) * mm, "end": v(-299.5, 619.1) * mm});
            skLineSegment(sketch, "E1682", {"start": v(-299.5, 619.1) * mm, "end": v(-298.64, 625) * mm});
            skLineSegment(sketch, "E1683", {"start": v(-298.64, 625) * mm, "end": v(-297.67, 631) * mm});
            skLineSegment(sketch, "E1684", {"start": v(-297.67, 631) * mm, "end": v(-296.6, 637.14) * mm});
            skLineSegment(sketch, "E1685", {"start": v(-296.6, 637.14) * mm, "end": v(-295.4, 643.4) * mm});
            skLineSegment(sketch, "E1686", {"start": v(-295.4, 643.4) * mm, "end": v(-294.06, 649.76) * mm});
            skLineSegment(sketch, "E1687", {"start": v(-294.06, 649.76) * mm, "end": v(-292.6, 656.23) * mm});
            skLineSegment(sketch, "E1688", {"start": v(-292.6, 656.23) * mm, "end": v(-291.02, 662.82) * mm});
            skLineSegment(sketch, "E1689", {"start": v(-112.27, 540.92) * mm, "end": v(-113.27, 540.85) * mm});
            skLineSegment(sketch, "E1690", {"start": v(-113.27, 540.85) * mm, "end": v(-123.98, 540.94) * mm});
            skLineSegment(sketch, "E1691", {"start": v(-123.98, 540.94) * mm, "end": v(-124.98, 541.07) * mm});
            skLineSegment(sketch, "E1692", {"start": v(-124.98, 541.07) * mm, "end": v(-126, 541.4) * mm});
            skLineSegment(sketch, "E1693", {"start": v(-126, 541.4) * mm, "end": v(-135.64, 545.92) * mm});
            skLineSegment(sketch, "E1694", {"start": v(-135.64, 545.92) * mm, "end": v(-136.59, 546.43) * mm});
            skLineSegment(sketch, "E1695", {"start": v(-136.59, 546.43) * mm, "end": v(-137.55, 547.15) * mm});
            skLineSegment(sketch, "E1696", {"start": v(-137.55, 547.15) * mm, "end": v(-138.53, 548.06) * mm});
            skLineSegment(sketch, "E1697", {"start": v(-138.53, 548.06) * mm, "end": v(-139.5, 549.18) * mm});
            skLineSegment(sketch, "E1698", {"start": v(-139.5, 549.18) * mm, "end": v(-145.11, 556.09) * mm});
            skLineSegment(sketch, "E1699", {"start": v(-145.11, 556.09) * mm, "end": v(-145.93, 557.13) * mm});
            skLineSegment(sketch, "E1700", {"start": v(-145.93, 557.13) * mm, "end": v(-146.76, 558.38) * mm});
            skLineSegment(sketch, "E1701", {"start": v(-146.76, 558.38) * mm, "end": v(-147.58, 559.82) * mm});
            skLineSegment(sketch, "E1702", {"start": v(-147.58, 559.82) * mm, "end": v(-148.4, 561.46) * mm});
            skLineSegment(sketch, "E1703", {"start": v(-148.4, 561.46) * mm, "end": v(-148.5, 561.7) * mm});
            skLineSegment(sketch, "E1704", {"start": v(-148.5, 561.7) * mm, "end": v(-149.17, 563.13) * mm});
            skLineSegment(sketch, "E1705", {"start": v(-149.17, 563.13) * mm, "end": v(-149.9, 564.67) * mm});
            skLineSegment(sketch, "E1706", {"start": v(-149.9, 564.67) * mm, "end": v(-150.74, 566.32) * mm});
            skLineSegment(sketch, "E1707", {"start": v(-150.74, 566.32) * mm, "end": v(-151.65, 568.08) * mm});
            skLineSegment(sketch, "E1708", {"start": v(-151.65, 568.08) * mm, "end": v(-152.66, 569.94) * mm});
            skLineSegment(sketch, "E1709", {"start": v(-152.66, 569.94) * mm, "end": v(-153.76, 571.9) * mm});
            skLineSegment(sketch, "E1710", {"start": v(-153.76, 571.9) * mm, "end": v(-154.97, 573.97) * mm});
            skLineSegment(sketch, "E1711", {"start": v(-154.97, 573.97) * mm, "end": v(-156.27, 576.14) * mm});
            skLineSegment(sketch, "E1712", {"start": v(-156.27, 576.14) * mm, "end": v(-157.68, 578.4) * mm});
            skLineSegment(sketch, "E1713", {"start": v(-157.68, 578.4) * mm, "end": v(-159.2, 580.76) * mm});
            skLineSegment(sketch, "E1714", {"start": v(-159.2, 580.76) * mm, "end": v(-160.84, 583.2) * mm});
            skLineSegment(sketch, "E1715", {"start": v(-160.84, 583.2) * mm, "end": v(-162.59, 585.73) * mm});
            skLineSegment(sketch, "E1716", {"start": v(-162.59, 585.73) * mm, "end": v(-164.45, 588.35) * mm});
            skLineSegment(sketch, "E1717", {"start": v(-164.45, 588.35) * mm, "end": v(-166.44, 591.05) * mm});
            skLineSegment(sketch, "E1718", {"start": v(-166.44, 591.05) * mm, "end": v(-168.55, 593.82) * mm});
            skLineSegment(sketch, "E1719", {"start": v(-168.55, 593.82) * mm, "end": v(-170.8, 596.67) * mm});
            skLineSegment(sketch, "E1720", {"start": v(-170.8, 596.67) * mm, "end": v(-173.16, 599.6) * mm});
            skLineSegment(sketch, "E1721", {"start": v(-173.16, 599.6) * mm, "end": v(-175.67, 602.58) * mm});
            skLineSegment(sketch, "E1722", {"start": v(-175.67, 602.58) * mm, "end": v(-178.3, 605.64) * mm});
            skLineSegment(sketch, "E1723", {"start": v(-178.3, 605.64) * mm, "end": v(-181.08, 608.75) * mm});
            skLineSegment(sketch, "E1724", {"start": v(-181.08, 608.75) * mm, "end": v(-184, 611.92) * mm});
            skLineSegment(sketch, "E1725", {"start": v(-184, 611.92) * mm, "end": v(-187.06, 615.15) * mm});
            skLineSegment(sketch, "E1726", {"start": v(-187.06, 615.15) * mm, "end": v(-190.26, 618.43) * mm});
            skLineSegment(sketch, "E1727", {"start": v(-190.26, 618.43) * mm, "end": v(-193.62, 621.75) * mm});
            skLineSegment(sketch, "E1728", {"start": v(-193.62, 621.75) * mm, "end": v(-197.12, 625.12) * mm});
            skLineSegment(sketch, "E1729", {"start": v(-197.12, 625.12) * mm, "end": v(-200.77, 628.52) * mm});
            skLineSegment(sketch, "E1730", {"start": v(-200.77, 628.52) * mm, "end": v(-204.58, 631.96) * mm});
            skLineSegment(sketch, "E1731", {"start": v(-204.58, 631.96) * mm, "end": v(-208.55, 635.43) * mm});
            skLineSegment(sketch, "E1732", {"start": v(-208.55, 635.43) * mm, "end": v(-212.67, 638.93) * mm});
            skLineSegment(sketch, "E1733", {"start": v(-212.67, 638.93) * mm, "end": v(-216.95, 642.45) * mm});
            skLineSegment(sketch, "E1734", {"start": v(-216.95, 642.45) * mm, "end": v(-221.4, 646) * mm});
            skLineSegment(sketch, "E1735", {"start": v(-221.4, 646) * mm, "end": v(-226, 649.54) * mm});
            skLineSegment(sketch, "E1736", {"start": v(-226, 649.54) * mm, "end": v(-230.77, 653.1) * mm});
            skLineSegment(sketch, "E1737", {"start": v(-230.77, 653.1) * mm, "end": v(-235.7, 656.68) * mm});
            skLineSegment(sketch, "E1738", {"start": v(-235.7, 656.68) * mm, "end": v(-240.8, 660.25) * mm});
            skLineSegment(sketch, "E1739", {"start": v(-240.8, 660.25) * mm, "end": v(-246.07, 663.82) * mm});
            skLineSegment(sketch, "E1740", {"start": v(-246.07, 663.82) * mm, "end": v(-251.51, 667.38) * mm});
            skLineSegment(sketch, "E1741", {"start": v(-251.51, 667.38) * mm, "end": v(-257.12, 670.93) * mm});
            skLineSegment(sketch, "E1742", {"start": v(-257.12, 670.93) * mm, "end": v(-262.9, 674.47) * mm});
            skArc(sketch, "E1743", {"start": v(-262.9, 674.47) * mm, "mid": v(-277.02, 668.8) * mm, "end": v(-291.02, 662.82) * mm});
            skArc(sketch, "E1744", {"start": v(112.27, 540.92) * mm, "mid": v(107.78, 541.83) * mm, "end": v(103.28, 542.7) * mm});
            skArc(sketch, "E1745", {"start": v(310.72, 456.78) * mm, "mid": v(306.92, 459.35) * mm, "end": v(303.1, 461.87) * mm});
            skArc(sketch, "E1746", {"start": v(461.87, 303.1) * mm, "mid": v(459.35, 306.92) * mm, "end": v(456.78, 310.72) * mm});
            skArc(sketch, "E1747", {"start": v(542.7, 103.28) * mm, "mid": v(541.83, 107.78) * mm, "end": v(540.92, 112.27) * mm});
            skArc(sketch, "E1748", {"start": v(540.92, -112.27) * mm, "mid": v(541.83, -107.78) * mm, "end": v(542.7, -103.28) * mm});
            skArc(sketch, "E1749", {"start": v(456.78, -310.72) * mm, "mid": v(459.35, -306.92) * mm, "end": v(461.87, -303.1) * mm});
            skArc(sketch, "E1750", {"start": v(303.1, -461.87) * mm, "mid": v(306.92, -459.35) * mm, "end": v(310.72, -456.78) * mm});
            skArc(sketch, "E1751", {"start": v(103.28, -542.7) * mm, "mid": v(107.78, -541.83) * mm, "end": v(112.27, -540.92) * mm});
            skArc(sketch, "E1752", {"start": v(-112.27, -540.92) * mm, "mid": v(-107.78, -541.83) * mm, "end": v(-103.28, -542.7) * mm});
            skArc(sketch, "E1753", {"start": v(-310.72, -456.78) * mm, "mid": v(-306.92, -459.35) * mm, "end": v(-303.1, -461.87) * mm});
            skArc(sketch, "E1754", {"start": v(-461.87, -303.1) * mm, "mid": v(-459.35, -306.92) * mm, "end": v(-456.78, -310.72) * mm});
            skArc(sketch, "E1755", {"start": v(-542.7, -103.28) * mm, "mid": v(-541.83, -107.78) * mm, "end": v(-540.92, -112.27) * mm});
            skArc(sketch, "E1756", {"start": v(-540.92, 112.27) * mm, "mid": v(-541.83, 107.78) * mm, "end": v(-542.7, 103.28) * mm});
            skArc(sketch, "E1757", {"start": v(-456.78, 310.72) * mm, "mid": v(-459.35, 306.92) * mm, "end": v(-461.87, 303.1) * mm});
            skArc(sketch, "E1758", {"start": v(-303.1, 461.87) * mm, "mid": v(-306.92, 459.35) * mm, "end": v(-310.72, 456.78) * mm});
            skArc(sketch, "E1759", {"start": v(-103.28, 542.7) * mm, "mid": v(-107.78, 541.83) * mm, "end": v(-112.27, 540.92) * mm});
            skSolve(sketch);
        }
        {
            var Q0;
            Q0=makeQuery(id+"F0.imprint","IMPRINT",FACE,{"disambiguationData":[TD([[makeQuery(id+"F0.imprint","IMPRINT",EDGE,{"derivedFrom":sQuery(id+"F0.wireOp",EDGE,"E0")}),-1.0]])]});
            extrude(context, id + "F1", {"entities" : qUnion([Q0]), "depth" : 25.4 * mm});
        }
    });
